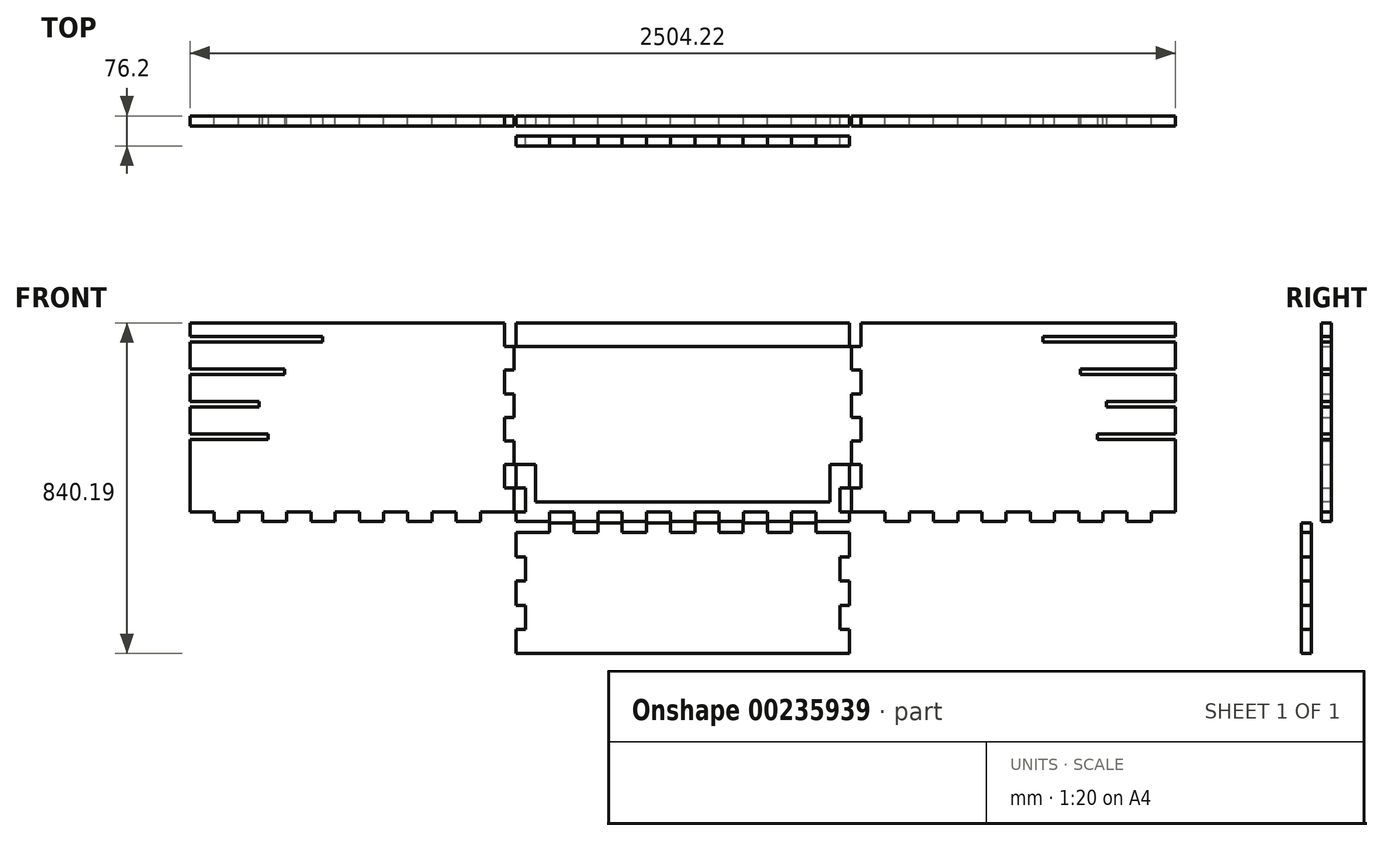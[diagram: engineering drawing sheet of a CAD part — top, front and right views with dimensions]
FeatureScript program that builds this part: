
annotation { "Feature Type Name" : "Feature", "Feature Type Description" : "" }
export const myFeature = defineFeature(function(context is Context, id is Id, definition is map)
    precondition{}
    {
        {
            var Q0;
            Q0=qCreatedBy(makeId("Front.planeOp"),FACE);
            var sketch = newSketch(context, id + "F0", { "sketchPlane" : qUnion([Q0])});
            skLineSegment(sketch, "E0", {"start": v(-454.2, -1273) * mm, "end": v(-454.2, -1334.62) * mm});
            skLineSegment(sketch, "E1", {"start": v(-430.22, -1273) * mm, "end": v(-454.2, -1273) * mm});
            skLineSegment(sketch, "E2", {"start": v(-454.2, -1150.02) * mm, "end": v(-454.2, -1211.63) * mm});
            skLineSegment(sketch, "E3", {"start": v(-454.2, -1211.63) * mm, "end": v(-430.22, -1211.63) * mm});
            skLineSegment(sketch, "E4", {"start": v(-430.22, -1150.02) * mm, "end": v(-454.2, -1150.02) * mm});
            skLineSegment(sketch, "E5", {"start": v(-454.2, -1027.04) * mm, "end": v(-454.2, -1088.65) * mm});
            skLineSegment(sketch, "E6", {"start": v(-454.2, -1088.65) * mm, "end": v(-430.22, -1088.65) * mm});
            skLineSegment(sketch, "E7", {"start": v(-430.22, -1027.04) * mm, "end": v(-454.2, -1027.04) * mm});
            skLineSegment(sketch, "E8", {"start": v(-454.2, -904.06) * mm, "end": v(-454.2, -965.67) * mm});
            skLineSegment(sketch, "E9", {"start": v(-454.2, -965.67) * mm, "end": v(-430.22, -965.67) * mm});
            skLineSegment(sketch, "E10", {"start": v(-430.22, -904.06) * mm, "end": v(-454.2, -904.06) * mm});
            skLineSegment(sketch, "E11", {"start": v(-454.2, -781.07) * mm, "end": v(-454.2, -842.69) * mm});
            skLineSegment(sketch, "E12", {"start": v(-454.2, -842.69) * mm, "end": v(-430.22, -842.69) * mm});
            skLineSegment(sketch, "E13", {"start": v(-430.22, -781.07) * mm, "end": v(-454.2, -781.07) * mm});
            skLineSegment(sketch, "E14", {"start": v(-454.2, -658.1) * mm, "end": v(-454.2, -719.7) * mm});
            skLineSegment(sketch, "E15", {"start": v(-454.2, -719.7) * mm, "end": v(-430.22, -719.7) * mm});
            skLineSegment(sketch, "E16", {"start": v(-430.22, -658.1) * mm, "end": v(-454.2, -658.1) * mm});
            skLineSegment(sketch, "E17", {"start": v(-454.2, -535.1) * mm, "end": v(-454.2, -596.71) * mm});
            skLineSegment(sketch, "E18", {"start": v(-454.2, -596.71) * mm, "end": v(-430.22, -596.71) * mm});
            skLineSegment(sketch, "E19", {"start": v(-454.2, -535.1) * mm, "end": v(-430.22, -535.1) * mm});
            skLineSegment(sketch, "E20", {"start": v(-430.22, -1211.63) * mm, "end": v(-430.22, -1273) * mm});
            skLineSegment(sketch, "E21", {"start": v(-430.22, -1088.65) * mm, "end": v(-430.22, -1150.02) * mm});
            skLineSegment(sketch, "E22", {"start": v(-430.22, -965.67) * mm, "end": v(-430.22, -1027.04) * mm});
            skLineSegment(sketch, "E23", {"start": v(-430.22, -842.69) * mm, "end": v(-430.22, -904.06) * mm});
            skLineSegment(sketch, "E24", {"start": v(-430.22, -719.7) * mm, "end": v(-430.22, -781.07) * mm});
            skLineSegment(sketch, "E25", {"start": v(-430.22, -596.71) * mm, "end": v(-430.22, -658.1) * mm});
            skLineSegment(sketch, "E26", {"start": v(-430.22, -535.1) * mm, "end": v(-368.73, -535.1) * mm});
            skLineSegment(sketch, "E27", {"start": v(-368.73, -511.12) * mm, "end": v(-368.73, -535.1) * mm});
            skLineSegment(sketch, "E28", {"start": v(-307.11, -511.12) * mm, "end": v(-368.73, -511.12) * mm});
            skLineSegment(sketch, "E29", {"start": v(-307.11, -535.1) * mm, "end": v(-307.11, -511.12) * mm});
            skLineSegment(sketch, "E30", {"start": v(-245.74, -535.1) * mm, "end": v(-307.11, -535.1) * mm});
            skLineSegment(sketch, "E31", {"start": v(-245.74, -511.12) * mm, "end": v(-245.74, -535.1) * mm});
            skLineSegment(sketch, "E32", {"start": v(-184.13, -511.12) * mm, "end": v(-245.74, -511.12) * mm});
            skLineSegment(sketch, "E33", {"start": v(-184.13, -535.1) * mm, "end": v(-184.13, -511.12) * mm});
            skLineSegment(sketch, "E34", {"start": v(-122.76, -535.1) * mm, "end": v(-184.13, -535.1) * mm});
            skLineSegment(sketch, "E35", {"start": v(-122.76, -511.12) * mm, "end": v(-122.76, -535.1) * mm});
            skLineSegment(sketch, "E36", {"start": v(-61.15, -511.12) * mm, "end": v(-122.76, -511.12) * mm});
            skLineSegment(sketch, "E37", {"start": v(-61.15, -535.1) * mm, "end": v(-61.15, -511.12) * mm});
            skLineSegment(sketch, "E38", {"start": v(0.22, -535.1) * mm, "end": v(-61.15, -535.1) * mm});
            skLineSegment(sketch, "E39", {"start": v(0.22, -511.12) * mm, "end": v(0.22, -535.1) * mm});
            skLineSegment(sketch, "E40", {"start": v(61.84, -511.12) * mm, "end": v(0.22, -511.12) * mm});
            skLineSegment(sketch, "E41", {"start": v(61.84, -535.1) * mm, "end": v(61.84, -511.12) * mm});
            skLineSegment(sketch, "E42", {"start": v(123.2, -535.1) * mm, "end": v(61.84, -535.1) * mm});
            skLineSegment(sketch, "E43", {"start": v(123.2, -511.12) * mm, "end": v(123.2, -535.1) * mm});
            skLineSegment(sketch, "E44", {"start": v(184.82, -511.12) * mm, "end": v(123.2, -511.12) * mm});
            skLineSegment(sketch, "E45", {"start": v(184.82, -535.1) * mm, "end": v(184.82, -511.12) * mm});
            skLineSegment(sketch, "E46", {"start": v(246.19, -535.1) * mm, "end": v(184.82, -535.1) * mm});
            skLineSegment(sketch, "E47", {"start": v(246.19, -511.12) * mm, "end": v(246.19, -535.1) * mm});
            skLineSegment(sketch, "E48", {"start": v(307.8, -511.12) * mm, "end": v(246.19, -511.12) * mm});
            skLineSegment(sketch, "E49", {"start": v(307.8, -535.1) * mm, "end": v(307.8, -511.12) * mm});
            skLineSegment(sketch, "E50", {"start": v(307.8, -535.1) * mm, "end": v(369.29, -535.1) * mm});
            skLineSegment(sketch, "E51", {"start": v(369.29, -1273) * mm, "end": v(369.29, -1211.63) * mm});
            skLineSegment(sketch, "E52", {"start": v(393.28, -1273) * mm, "end": v(369.29, -1273) * mm});
            skLineSegment(sketch, "E53", {"start": v(369.29, -1211.63) * mm, "end": v(393.28, -1211.63) * mm});
            skLineSegment(sketch, "E54", {"start": v(369.29, -1150.02) * mm, "end": v(369.29, -1088.65) * mm});
            skLineSegment(sketch, "E55", {"start": v(393.28, -1150.02) * mm, "end": v(369.29, -1150.02) * mm});
            skLineSegment(sketch, "E56", {"start": v(369.29, -1088.65) * mm, "end": v(393.28, -1088.65) * mm});
            skLineSegment(sketch, "E57", {"start": v(369.29, -1027.04) * mm, "end": v(369.29, -965.67) * mm});
            skLineSegment(sketch, "E58", {"start": v(393.28, -1027.04) * mm, "end": v(369.29, -1027.04) * mm});
            skLineSegment(sketch, "E59", {"start": v(369.29, -965.67) * mm, "end": v(393.28, -965.67) * mm});
            skLineSegment(sketch, "E60", {"start": v(369.29, -904.06) * mm, "end": v(369.29, -842.69) * mm});
            skLineSegment(sketch, "E61", {"start": v(393.28, -904.06) * mm, "end": v(369.29, -904.06) * mm});
            skLineSegment(sketch, "E62", {"start": v(369.29, -842.69) * mm, "end": v(393.28, -842.69) * mm});
            skLineSegment(sketch, "E63", {"start": v(369.29, -781.07) * mm, "end": v(369.29, -719.7) * mm});
            skLineSegment(sketch, "E64", {"start": v(393.28, -781.07) * mm, "end": v(369.29, -781.07) * mm});
            skLineSegment(sketch, "E65", {"start": v(369.29, -719.7) * mm, "end": v(393.28, -719.7) * mm});
            skLineSegment(sketch, "E66", {"start": v(369.29, -658.1) * mm, "end": v(369.29, -596.71) * mm});
            skLineSegment(sketch, "E67", {"start": v(393.28, -658.1) * mm, "end": v(369.29, -658.1) * mm});
            skLineSegment(sketch, "E68", {"start": v(369.29, -596.71) * mm, "end": v(393.28, -596.71) * mm});
            skLineSegment(sketch, "E69", {"start": v(369.29, -535.1) * mm, "end": v(393.28, -535.1) * mm});
            skLineSegment(sketch, "E70", {"start": v(393.28, -1334.62) * mm, "end": v(393.28, -1273) * mm});
            skLineSegment(sketch, "E71", {"start": v(393.28, -1211.63) * mm, "end": v(393.28, -1150.02) * mm});
            skLineSegment(sketch, "E72", {"start": v(393.28, -1088.65) * mm, "end": v(393.28, -1027.04) * mm});
            skLineSegment(sketch, "E73", {"start": v(393.28, -965.67) * mm, "end": v(393.28, -904.06) * mm});
            skLineSegment(sketch, "E74", {"start": v(393.28, -842.69) * mm, "end": v(393.28, -781.07) * mm});
            skLineSegment(sketch, "E75", {"start": v(393.28, -719.7) * mm, "end": v(393.28, -658.1) * mm});
            skLineSegment(sketch, "E76", {"start": v(393.28, -596.71) * mm, "end": v(393.28, -535.1) * mm});
            skLineSegment(sketch, "E77", {"start": v(-454.2, -506.25) * mm, "end": v(-454.2, -482.26) * mm});
            skLineSegment(sketch, "E78", {"start": v(-454.2, -482.26) * mm, "end": v(-454.2, -482.15) * mm});
            skLineSegment(sketch, "E79", {"start": v(-430.22, -482.15) * mm, "end": v(-454.2, -482.15) * mm});
            skLineSegment(sketch, "E80", {"start": v(-454.2, -362.23) * mm, "end": v(-454.2, -422.3) * mm});
            skLineSegment(sketch, "E81", {"start": v(-454.2, -422.3) * mm, "end": v(-430.22, -422.3) * mm});
            skLineSegment(sketch, "E82", {"start": v(-430.22, -362.23) * mm, "end": v(-454.2, -362.23) * mm});
            skLineSegment(sketch, "E83", {"start": v(-454.2, -242.33) * mm, "end": v(-454.2, -302.4) * mm});
            skLineSegment(sketch, "E84", {"start": v(-454.2, -302.4) * mm, "end": v(-430.22, -302.4) * mm});
            skLineSegment(sketch, "E85", {"start": v(-430.22, -242.33) * mm, "end": v(-454.2, -242.33) * mm});
            skLineSegment(sketch, "E86", {"start": v(-454.2, -122.41) * mm, "end": v(-454.2, -182.5) * mm});
            skLineSegment(sketch, "E87", {"start": v(-454.2, -182.5) * mm, "end": v(-430.22, -182.5) * mm});
            skLineSegment(sketch, "E88", {"start": v(-430.22, -122.41) * mm, "end": v(-454.2, -122.41) * mm});
            skLineSegment(sketch, "E89", {"start": v(-454.2, -2.5) * mm, "end": v(-454.2, -62.59) * mm});
            skLineSegment(sketch, "E90", {"start": v(-454.2, -62.59) * mm, "end": v(-430.22, -62.59) * mm});
            skLineSegment(sketch, "E91", {"start": v(-430.22, -2.5) * mm, "end": v(-454.2, -2.5) * mm});
            skLineSegment(sketch, "E92", {"start": v(-454.2, 117.4) * mm, "end": v(-454.2, 57.32) * mm});
            skLineSegment(sketch, "E93", {"start": v(-454.2, 57.32) * mm, "end": v(-430.22, 57.32) * mm});
            skLineSegment(sketch, "E94", {"start": v(-430.22, 117.4) * mm, "end": v(-454.2, 117.4) * mm});
            skLineSegment(sketch, "E95", {"start": v(-454.2, 237.31) * mm, "end": v(-454.2, 177.24) * mm});
            skLineSegment(sketch, "E96", {"start": v(-454.2, 177.24) * mm, "end": v(-430.22, 177.24) * mm});
            skLineSegment(sketch, "E97", {"start": v(-430.22, 237.31) * mm, "end": v(-454.2, 237.31) * mm});
            skLineSegment(sketch, "E98", {"start": v(-454.2, 357.22) * mm, "end": v(-454.2, 297.14) * mm});
            skLineSegment(sketch, "E99", {"start": v(-454.2, 297.14) * mm, "end": v(-430.22, 297.14) * mm});
            skLineSegment(sketch, "E100", {"start": v(-430.22, 357.22) * mm, "end": v(-454.2, 357.22) * mm});
            skLineSegment(sketch, "E101", {"start": v(-454.2, 417.05) * mm, "end": v(-454.2, 417.17) * mm});
            skLineSegment(sketch, "E102", {"start": v(-430.22, -422.3) * mm, "end": v(-430.22, -482.15) * mm});
            skLineSegment(sketch, "E103", {"start": v(-430.22, -302.4) * mm, "end": v(-430.22, -362.23) * mm});
            skLineSegment(sketch, "E104", {"start": v(-430.22, -182.5) * mm, "end": v(-430.22, -242.33) * mm});
            skLineSegment(sketch, "E105", {"start": v(-430.22, -62.59) * mm, "end": v(-430.22, -122.41) * mm});
            skLineSegment(sketch, "E106", {"start": v(-430.22, 57.32) * mm, "end": v(-430.22, -2.5) * mm});
            skLineSegment(sketch, "E107", {"start": v(-430.22, 177.24) * mm, "end": v(-430.22, 117.4) * mm});
            skLineSegment(sketch, "E108", {"start": v(-430.22, 297.14) * mm, "end": v(-430.22, 237.31) * mm});
            skLineSegment(sketch, "E109", {"start": v(-430.22, 417.05) * mm, "end": v(-430.22, 357.22) * mm});
            skLineSegment(sketch, "E110", {"start": v(-368.61, -506.25) * mm, "end": v(-368.61, -482.26) * mm});
            skLineSegment(sketch, "E111", {"start": v(-307.24, -482.26) * mm, "end": v(-307.24, -506.25) * mm});
            skLineSegment(sketch, "E112", {"start": v(-307.24, -506.25) * mm, "end": v(-245.62, -506.25) * mm});
            skLineSegment(sketch, "E113", {"start": v(-245.62, -506.25) * mm, "end": v(-245.62, -482.26) * mm});
            skLineSegment(sketch, "E114", {"start": v(-245.62, -482.26) * mm, "end": v(-184.26, -482.26) * mm});
            skLineSegment(sketch, "E115", {"start": v(-184.26, -482.26) * mm, "end": v(-184.26, -506.25) * mm});
            skLineSegment(sketch, "E116", {"start": v(-184.26, -506.25) * mm, "end": v(-122.64, -506.25) * mm});
            skLineSegment(sketch, "E117", {"start": v(-122.64, -506.25) * mm, "end": v(-122.64, -482.26) * mm});
            skLineSegment(sketch, "E118", {"start": v(-122.64, -482.26) * mm, "end": v(-61.27, -482.26) * mm});
            skLineSegment(sketch, "E119", {"start": v(-61.27, -482.26) * mm, "end": v(-61.27, -506.25) * mm});
            skLineSegment(sketch, "E120", {"start": v(-61.27, -506.25) * mm, "end": v(0.34, -506.25) * mm});
            skLineSegment(sketch, "E121", {"start": v(0.34, -506.25) * mm, "end": v(0.34, -482.26) * mm});
            skLineSegment(sketch, "E122", {"start": v(0.34, -482.26) * mm, "end": v(61.71, -482.26) * mm});
            skLineSegment(sketch, "E123", {"start": v(61.71, -482.26) * mm, "end": v(61.71, -506.25) * mm});
            skLineSegment(sketch, "E124", {"start": v(61.71, -506.25) * mm, "end": v(123.33, -506.25) * mm});
            skLineSegment(sketch, "E125", {"start": v(123.33, -506.25) * mm, "end": v(123.33, -482.26) * mm});
            skLineSegment(sketch, "E126", {"start": v(123.33, -482.26) * mm, "end": v(184.7, -482.26) * mm});
            skLineSegment(sketch, "E127", {"start": v(184.7, -482.26) * mm, "end": v(184.7, -506.25) * mm});
            skLineSegment(sketch, "E128", {"start": v(184.7, -506.25) * mm, "end": v(246.3, -506.25) * mm});
            skLineSegment(sketch, "E129", {"start": v(246.3, -506.25) * mm, "end": v(246.3, -482.26) * mm});
            skLineSegment(sketch, "E130", {"start": v(246.3, -482.26) * mm, "end": v(307.69, -482.26) * mm});
            skLineSegment(sketch, "E131", {"start": v(307.69, -482.26) * mm, "end": v(307.69, -506.25) * mm});
            skLineSegment(sketch, "E132", {"start": v(307.69, -506.25) * mm, "end": v(369.29, -506.25) * mm});
            skLineSegment(sketch, "E133", {"start": v(369.29, -482.15) * mm, "end": v(369.29, -422.3) * mm});
            skLineSegment(sketch, "E134", {"start": v(369.29, -482.15) * mm, "end": v(393.28, -482.15) * mm});
            skLineSegment(sketch, "E135", {"start": v(369.29, -422.3) * mm, "end": v(393.28, -422.3) * mm});
            skLineSegment(sketch, "E136", {"start": v(369.29, -362.23) * mm, "end": v(369.29, -302.4) * mm});
            skLineSegment(sketch, "E137", {"start": v(393.28, -362.23) * mm, "end": v(369.29, -362.23) * mm});
            skLineSegment(sketch, "E138", {"start": v(369.29, -302.4) * mm, "end": v(393.28, -302.4) * mm});
            skLineSegment(sketch, "E139", {"start": v(369.29, -242.33) * mm, "end": v(369.29, -182.5) * mm});
            skLineSegment(sketch, "E140", {"start": v(393.28, -242.33) * mm, "end": v(369.29, -242.33) * mm});
            skLineSegment(sketch, "E141", {"start": v(369.29, -182.5) * mm, "end": v(393.28, -182.5) * mm});
            skLineSegment(sketch, "E142", {"start": v(369.29, -122.41) * mm, "end": v(369.29, -62.59) * mm});
            skLineSegment(sketch, "E143", {"start": v(393.28, -122.41) * mm, "end": v(369.29, -122.41) * mm});
            skLineSegment(sketch, "E144", {"start": v(369.29, -62.59) * mm, "end": v(393.28, -62.59) * mm});
            skLineSegment(sketch, "E145", {"start": v(369.29, -2.5) * mm, "end": v(369.29, 57.32) * mm});
            skLineSegment(sketch, "E146", {"start": v(393.28, -2.5) * mm, "end": v(369.29, -2.5) * mm});
            skLineSegment(sketch, "E147", {"start": v(369.29, 57.32) * mm, "end": v(393.28, 57.32) * mm});
            skLineSegment(sketch, "E148", {"start": v(369.29, 117.4) * mm, "end": v(369.29, 177.24) * mm});
            skLineSegment(sketch, "E149", {"start": v(393.28, 117.4) * mm, "end": v(369.29, 117.4) * mm});
            skLineSegment(sketch, "E150", {"start": v(369.29, 177.24) * mm, "end": v(393.28, 177.24) * mm});
            skLineSegment(sketch, "E151", {"start": v(369.29, 237.31) * mm, "end": v(369.29, 297.14) * mm});
            skLineSegment(sketch, "E152", {"start": v(393.28, 237.31) * mm, "end": v(369.29, 237.31) * mm});
            skLineSegment(sketch, "E153", {"start": v(369.29, 297.14) * mm, "end": v(393.28, 297.14) * mm});
            skLineSegment(sketch, "E154", {"start": v(369.29, 357.22) * mm, "end": v(369.29, 417.05) * mm});
            skLineSegment(sketch, "E155", {"start": v(393.28, 357.22) * mm, "end": v(369.29, 357.22) * mm});
            skLineSegment(sketch, "E156", {"start": v(369.29, -506.25) * mm, "end": v(393.28, -506.25) * mm});
            skLineSegment(sketch, "E157", {"start": v(393.28, -506.25) * mm, "end": v(393.28, -482.26) * mm});
            skLineSegment(sketch, "E158", {"start": v(393.28, -482.26) * mm, "end": v(393.28, -482.15) * mm});
            skLineSegment(sketch, "E159", {"start": v(393.28, -422.3) * mm, "end": v(393.28, -362.23) * mm});
            skLineSegment(sketch, "E160", {"start": v(393.28, -302.4) * mm, "end": v(393.28, -242.33) * mm});
            skLineSegment(sketch, "E161", {"start": v(393.28, -182.5) * mm, "end": v(393.28, -122.41) * mm});
            skLineSegment(sketch, "E162", {"start": v(393.28, -62.59) * mm, "end": v(393.28, -2.5) * mm});
            skLineSegment(sketch, "E163", {"start": v(393.28, 57.32) * mm, "end": v(393.28, 117.4) * mm});
            skLineSegment(sketch, "E164", {"start": v(393.28, 177.24) * mm, "end": v(393.28, 237.31) * mm});
            skLineSegment(sketch, "E165", {"start": v(393.28, 297.14) * mm, "end": v(393.28, 357.22) * mm});
            skLineSegment(sketch, "E166", {"start": v(393.28, 417.05) * mm, "end": v(393.28, 417.17) * mm});
            skLineSegment(sketch, "E167", {"start": v(-1282.57, -482.26) * mm, "end": v(-1221.08, -482.26) * mm});
            skLineSegment(sketch, "E168", {"start": v(-1221.08, -482.26) * mm, "end": v(-1221.08, -506.25) * mm});
            skLineSegment(sketch, "E169", {"start": v(-1221.08, -506.25) * mm, "end": v(-1159.47, -506.25) * mm});
            skLineSegment(sketch, "E170", {"start": v(-1159.47, -506.25) * mm, "end": v(-1159.47, -482.26) * mm});
            skLineSegment(sketch, "E171", {"start": v(-1159.47, -482.26) * mm, "end": v(-1098.1, -482.26) * mm});
            skLineSegment(sketch, "E172", {"start": v(-1098.1, -482.26) * mm, "end": v(-1098.1, -506.25) * mm});
            skLineSegment(sketch, "E173", {"start": v(-1098.1, -506.25) * mm, "end": v(-1036.48, -506.25) * mm});
            skLineSegment(sketch, "E174", {"start": v(-1036.48, -506.25) * mm, "end": v(-1036.48, -482.26) * mm});
            skLineSegment(sketch, "E175", {"start": v(-1036.48, -482.26) * mm, "end": v(-975.11, -482.26) * mm});
            skLineSegment(sketch, "E176", {"start": v(-975.11, -482.26) * mm, "end": v(-975.11, -506.25) * mm});
            skLineSegment(sketch, "E177", {"start": v(-975.11, -506.25) * mm, "end": v(-913.5, -506.25) * mm});
            skLineSegment(sketch, "E178", {"start": v(-913.5, -506.25) * mm, "end": v(-913.5, -482.26) * mm});
            skLineSegment(sketch, "E179", {"start": v(-913.5, -482.26) * mm, "end": v(-852.13, -482.26) * mm});
            skLineSegment(sketch, "E180", {"start": v(-852.13, -482.26) * mm, "end": v(-852.13, -506.25) * mm});
            skLineSegment(sketch, "E181", {"start": v(-852.13, -506.25) * mm, "end": v(-790.52, -506.25) * mm});
            skLineSegment(sketch, "E182", {"start": v(-790.52, -506.25) * mm, "end": v(-790.52, -482.26) * mm});
            skLineSegment(sketch, "E183", {"start": v(-790.52, -482.26) * mm, "end": v(-729.15, -482.26) * mm});
            skLineSegment(sketch, "E184", {"start": v(-729.15, -482.26) * mm, "end": v(-729.15, -506.25) * mm});
            skLineSegment(sketch, "E185", {"start": v(-729.15, -506.25) * mm, "end": v(-667.53, -506.25) * mm});
            skLineSegment(sketch, "E186", {"start": v(-667.53, -506.25) * mm, "end": v(-667.53, -482.26) * mm});
            skLineSegment(sketch, "E187", {"start": v(-667.53, -482.26) * mm, "end": v(-606.17, -482.26) * mm});
            skLineSegment(sketch, "E188", {"start": v(-606.17, -482.26) * mm, "end": v(-606.17, -506.25) * mm});
            skLineSegment(sketch, "E189", {"start": v(-606.17, -506.25) * mm, "end": v(-544.55, -506.25) * mm});
            skLineSegment(sketch, "E190", {"start": v(-544.55, -506.25) * mm, "end": v(-544.55, -482.26) * mm});
            skLineSegment(sketch, "E191", {"start": v(-544.55, -482.26) * mm, "end": v(-483.06, -482.26) * mm});
            skLineSegment(sketch, "E192", {"start": v(-483.06, -482.26) * mm, "end": v(-459.08, -482.26) * mm});
            skLineSegment(sketch, "E193", {"start": v(-483.06, -422.19) * mm, "end": v(-483.06, -362.36) * mm});
            skLineSegment(sketch, "E194", {"start": v(-459.08, -422.19) * mm, "end": v(-483.06, -422.19) * mm});
            skLineSegment(sketch, "E195", {"start": v(-483.06, -362.36) * mm, "end": v(-459.08, -362.36) * mm});
            skLineSegment(sketch, "E196", {"start": v(-483.06, -302.28) * mm, "end": v(-483.06, -242.45) * mm});
            skLineSegment(sketch, "E197", {"start": v(-459.08, -302.28) * mm, "end": v(-483.06, -302.28) * mm});
            skLineSegment(sketch, "E198", {"start": v(-483.06, -242.45) * mm, "end": v(-459.08, -242.45) * mm});
            skLineSegment(sketch, "E199", {"start": v(-483.06, -182.38) * mm, "end": v(-483.06, -122.53) * mm});
            skLineSegment(sketch, "E200", {"start": v(-459.08, -182.38) * mm, "end": v(-483.06, -182.38) * mm});
            skLineSegment(sketch, "E201", {"start": v(-483.06, -122.53) * mm, "end": v(-459.08, -122.53) * mm});
            skLineSegment(sketch, "E202", {"start": v(-483.06, -62.46) * mm, "end": v(-483.06, -2.63) * mm});
            skLineSegment(sketch, "E203", {"start": v(-459.08, -62.46) * mm, "end": v(-483.06, -62.46) * mm});
            skLineSegment(sketch, "E204", {"start": v(-483.06, -2.63) * mm, "end": v(-459.08, -2.63) * mm});
            skLineSegment(sketch, "E205", {"start": v(-483.06, 57.45) * mm, "end": v(-483.06, 117.28) * mm});
            skLineSegment(sketch, "E206", {"start": v(-459.08, 57.45) * mm, "end": v(-483.06, 57.45) * mm});
            skLineSegment(sketch, "E207", {"start": v(-483.06, 117.28) * mm, "end": v(-459.08, 117.28) * mm});
            skLineSegment(sketch, "E208", {"start": v(-483.06, 177.36) * mm, "end": v(-483.06, 237.19) * mm});
            skLineSegment(sketch, "E209", {"start": v(-459.08, 177.36) * mm, "end": v(-483.06, 177.36) * mm});
            skLineSegment(sketch, "E210", {"start": v(-483.06, 237.19) * mm, "end": v(-459.08, 237.19) * mm});
            skLineSegment(sketch, "E211", {"start": v(-483.06, 297.26) * mm, "end": v(-483.06, 357.1) * mm});
            skLineSegment(sketch, "E212", {"start": v(-459.08, 297.26) * mm, "end": v(-483.06, 297.26) * mm});
            skLineSegment(sketch, "E213", {"start": v(-483.06, 357.1) * mm, "end": v(-459.08, 357.1) * mm});
            skLineSegment(sketch, "E214", {"start": v(-459.08, -482.26) * mm, "end": v(-459.08, -422.19) * mm});
            skLineSegment(sketch, "E215", {"start": v(-459.08, -362.36) * mm, "end": v(-459.08, -302.28) * mm});
            skLineSegment(sketch, "E216", {"start": v(-459.08, -242.45) * mm, "end": v(-459.08, -182.38) * mm});
            skLineSegment(sketch, "E217", {"start": v(-459.08, -122.53) * mm, "end": v(-459.08, -62.46) * mm});
            skLineSegment(sketch, "E218", {"start": v(-459.08, -2.63) * mm, "end": v(-459.08, 57.45) * mm});
            skLineSegment(sketch, "E219", {"start": v(-459.08, 117.28) * mm, "end": v(-459.08, 177.36) * mm});
            skLineSegment(sketch, "E220", {"start": v(-459.08, 237.19) * mm, "end": v(-459.08, 297.26) * mm});
            skLineSegment(sketch, "E221", {"start": v(-459.08, 357.1) * mm, "end": v(-459.08, 417.17) * mm});
            skLineSegment(sketch, "E222", {"start": v(398.15, -422.19) * mm, "end": v(398.15, -482.26) * mm});
            skLineSegment(sketch, "E223", {"start": v(398.15, -482.26) * mm, "end": v(422.13, -482.26) * mm});
            skLineSegment(sketch, "E224", {"start": v(422.13, -422.19) * mm, "end": v(398.15, -422.19) * mm});
            skLineSegment(sketch, "E225", {"start": v(398.15, -302.28) * mm, "end": v(398.15, -362.36) * mm});
            skLineSegment(sketch, "E226", {"start": v(398.15, -362.36) * mm, "end": v(422.13, -362.36) * mm});
            skLineSegment(sketch, "E227", {"start": v(422.13, -302.28) * mm, "end": v(398.15, -302.28) * mm});
            skLineSegment(sketch, "E228", {"start": v(398.15, -182.38) * mm, "end": v(398.15, -242.45) * mm});
            skLineSegment(sketch, "E229", {"start": v(398.15, -242.45) * mm, "end": v(422.13, -242.45) * mm});
            skLineSegment(sketch, "E230", {"start": v(422.13, -182.38) * mm, "end": v(398.15, -182.38) * mm});
            skLineSegment(sketch, "E231", {"start": v(398.15, -62.46) * mm, "end": v(398.15, -122.53) * mm});
            skLineSegment(sketch, "E232", {"start": v(398.15, -122.53) * mm, "end": v(422.13, -122.53) * mm});
            skLineSegment(sketch, "E233", {"start": v(422.13, -62.46) * mm, "end": v(398.15, -62.46) * mm});
            skLineSegment(sketch, "E234", {"start": v(398.15, 57.45) * mm, "end": v(398.15, -2.63) * mm});
            skLineSegment(sketch, "E235", {"start": v(398.15, -2.63) * mm, "end": v(422.13, -2.63) * mm});
            skLineSegment(sketch, "E236", {"start": v(422.13, 57.45) * mm, "end": v(398.15, 57.45) * mm});
            skLineSegment(sketch, "E237", {"start": v(398.15, 177.36) * mm, "end": v(398.15, 117.28) * mm});
            skLineSegment(sketch, "E238", {"start": v(398.15, 117.28) * mm, "end": v(422.13, 117.28) * mm});
            skLineSegment(sketch, "E239", {"start": v(422.13, 177.36) * mm, "end": v(398.15, 177.36) * mm});
            skLineSegment(sketch, "E240", {"start": v(398.15, 297.26) * mm, "end": v(398.15, 237.19) * mm});
            skLineSegment(sketch, "E241", {"start": v(398.15, 237.19) * mm, "end": v(422.13, 237.19) * mm});
            skLineSegment(sketch, "E242", {"start": v(422.13, 297.26) * mm, "end": v(398.15, 297.26) * mm});
            skLineSegment(sketch, "E243", {"start": v(398.15, 417.17) * mm, "end": v(398.15, 357.1) * mm});
            skLineSegment(sketch, "E244", {"start": v(398.15, 357.1) * mm, "end": v(422.13, 357.1) * mm});
            skLineSegment(sketch, "E245", {"start": v(422.13, -482.26) * mm, "end": v(483.63, -482.26) * mm});
            skLineSegment(sketch, "E246", {"start": v(422.13, -362.36) * mm, "end": v(422.13, -422.19) * mm});
            skLineSegment(sketch, "E247", {"start": v(422.13, -242.45) * mm, "end": v(422.13, -302.28) * mm});
            skLineSegment(sketch, "E248", {"start": v(422.13, -122.53) * mm, "end": v(422.13, -182.38) * mm});
            skLineSegment(sketch, "E249", {"start": v(422.13, -2.63) * mm, "end": v(422.13, -62.46) * mm});
            skLineSegment(sketch, "E250", {"start": v(422.13, 117.28) * mm, "end": v(422.13, 57.45) * mm});
            skLineSegment(sketch, "E251", {"start": v(422.13, 237.19) * mm, "end": v(422.13, 177.36) * mm});
            skLineSegment(sketch, "E252", {"start": v(422.13, 357.1) * mm, "end": v(422.13, 297.26) * mm});
            skLineSegment(sketch, "E253", {"start": v(483.63, -482.26) * mm, "end": v(483.63, -506.25) * mm});
            skLineSegment(sketch, "E254", {"start": v(483.63, -506.25) * mm, "end": v(545.24, -506.25) * mm});
            skLineSegment(sketch, "E255", {"start": v(545.24, -506.25) * mm, "end": v(545.24, -482.26) * mm});
            skLineSegment(sketch, "E256", {"start": v(545.24, -482.26) * mm, "end": v(606.6, -482.26) * mm});
            skLineSegment(sketch, "E257", {"start": v(606.6, -482.26) * mm, "end": v(606.6, -506.25) * mm});
            skLineSegment(sketch, "E258", {"start": v(606.6, -506.25) * mm, "end": v(668.22, -506.25) * mm});
            skLineSegment(sketch, "E259", {"start": v(668.22, -506.25) * mm, "end": v(668.22, -482.26) * mm});
            skLineSegment(sketch, "E260", {"start": v(668.22, -482.26) * mm, "end": v(729.59, -482.26) * mm});
            skLineSegment(sketch, "E261", {"start": v(729.59, -482.26) * mm, "end": v(729.59, -506.25) * mm});
            skLineSegment(sketch, "E262", {"start": v(729.59, -506.25) * mm, "end": v(791.2, -506.25) * mm});
            skLineSegment(sketch, "E263", {"start": v(791.2, -506.25) * mm, "end": v(791.2, -482.26) * mm});
            skLineSegment(sketch, "E264", {"start": v(791.2, -482.26) * mm, "end": v(852.58, -482.26) * mm});
            skLineSegment(sketch, "E265", {"start": v(852.58, -482.26) * mm, "end": v(852.58, -506.25) * mm});
            skLineSegment(sketch, "E266", {"start": v(852.58, -506.25) * mm, "end": v(914.19, -506.25) * mm});
            skLineSegment(sketch, "E267", {"start": v(914.19, -506.25) * mm, "end": v(914.19, -482.26) * mm});
            skLineSegment(sketch, "E268", {"start": v(914.19, -482.26) * mm, "end": v(975.56, -482.26) * mm});
            skLineSegment(sketch, "E269", {"start": v(975.56, -482.26) * mm, "end": v(975.56, -506.25) * mm});
            skLineSegment(sketch, "E270", {"start": v(975.56, -506.25) * mm, "end": v(1037.17, -506.25) * mm});
            skLineSegment(sketch, "E271", {"start": v(1037.17, -506.25) * mm, "end": v(1037.17, -482.26) * mm});
            skLineSegment(sketch, "E272", {"start": v(1037.17, -482.26) * mm, "end": v(1098.54, -482.26) * mm});
            skLineSegment(sketch, "E273", {"start": v(1098.54, -482.26) * mm, "end": v(1098.54, -506.25) * mm});
            skLineSegment(sketch, "E274", {"start": v(1098.54, -506.25) * mm, "end": v(1160.15, -506.25) * mm});
            skLineSegment(sketch, "E275", {"start": v(1160.15, -506.25) * mm, "end": v(1160.15, -482.26) * mm});
            skLineSegment(sketch, "E276", {"start": v(1160.15, -482.26) * mm, "end": v(1221.65, -482.26) * mm});
            skLineSegment(sketch, "E277", {"start": v(-1549.7, -928.38) * mm, "end": v(1612.7, -928.38) * mm, "construction": true});
            skLineSegment(sketch, "E278", {"start": v(-1282.57, -482.26) * mm, "end": v(-1282.57, 417.17) * mm});
            skLineSegment(sketch, "E279", {"start": v(-1282.57, 417.17) * mm, "end": v(-454.2, 417.17) * mm});
            skLineSegment(sketch, "E280", {"start": v(-430.22, 417.05) * mm, "end": v(369.29, 417.05) * mm});
            skLineSegment(sketch, "E281", {"start": v(1221.65, -482.26) * mm, "end": v(1221.65, 417.17) * mm});
            skLineSegment(sketch, "E282", {"start": v(1221.65, 417.17) * mm, "end": v(398.15, 417.17) * mm});
            skLineSegment(sketch, "E283", {"start": v(-454.2, -1334.62) * mm, "end": v(393.28, -1334.62) * mm});
            skPoint(sketch, "E284", {"position": v(-404.82, 391.65) * mm});
            skPoint(sketch, "E285", {"position": v(343.89, 391.65) * mm});
            skLineSegment(sketch, "E286", {"start": v(-368.61, -482.26) * mm, "end": v(-307.24, -482.26) * mm});
            skLineSegment(sketch, "E287", {"start": v(-454.2, -506.25) * mm, "end": v(-368.61, -506.25) * mm});
            skSolve(sketch);
        }
        {
            var Q0;
            Q0=makeQuery(id+"F0.imprint","IMPRINT",FACE,{"disambiguationData":[TD([[makeQuery(id+"F0.imprint","IMPRINT",EDGE,{"derivedFrom":sQuery(id+"F0.wireOp",EDGE,"E167")}),1.0]])]});
            var Q1;
            Q1=makeQuery(id+"F0.imprint","IMPRINT",FACE,{"disambiguationData":[TD([[makeQuery(id+"F0.imprint","IMPRINT",EDGE,{"derivedFrom":sQuery(id+"F0.wireOp",EDGE,"E77")}),-1.0]])]});
            var Q2;
            Q2=makeQuery(id+"F0.imprint","IMPRINT",FACE,{"disambiguationData":[TD([[makeQuery(id+"F0.imprint","IMPRINT",EDGE,{"derivedFrom":sQuery(id+"F0.wireOp",EDGE,"E222")}),1.0]])]});
            var Q3;
            Q3=makeQuery(id+"F0.imprint","IMPRINT",FACE,{"disambiguationData":[TD([[makeQuery(id+"F0.imprint","IMPRINT",EDGE,{"derivedFrom":sQuery(id+"F0.wireOp",EDGE,"E0")}),1.0]])]});
            extrude(context, id + "F1", {"entities" : qUnion([Q0, Q1, Q2, Q3]), "depth" : 25.4 * mm});
        }
        {
            var Q0;
            Q0=makeQuery(id+"F1.opExtrude","CAP_FACE",FACE,{"disambiguationData":[OSD([sQuery(id+"F0.wireOp",EDGE,"E77"),sQuery(id+"F0.wireOp",EDGE,"E78"),sQuery(id+"F0.wireOp",EDGE,"E79"),sQuery(id+"F0.wireOp",EDGE,"E80"),sQuery(id+"F0.wireOp",EDGE,"E81"),sQuery(id+"F0.wireOp",EDGE,"E82"),sQuery(id+"F0.wireOp",EDGE,"E83"),sQuery(id+"F0.wireOp",EDGE,"E84"),sQuery(id+"F0.wireOp",EDGE,"E85"),sQuery(id+"F0.wireOp",EDGE,"E86"),sQuery(id+"F0.wireOp",EDGE,"E87"),sQuery(id+"F0.wireOp",EDGE,"E88"),sQuery(id+"F0.wireOp",EDGE,"E89"),sQuery(id+"F0.wireOp",EDGE,"E90"),sQuery(id+"F0.wireOp",EDGE,"E91"),sQuery(id+"F0.wireOp",EDGE,"E92"),sQuery(id+"F0.wireOp",EDGE,"E93"),sQuery(id+"F0.wireOp",EDGE,"E94"),sQuery(id+"F0.wireOp",EDGE,"E95"),sQuery(id+"F0.wireOp",EDGE,"E96"),sQuery(id+"F0.wireOp",EDGE,"E97"),sQuery(id+"F0.wireOp",EDGE,"E98"),sQuery(id+"F0.wireOp",EDGE,"E99"),sQuery(id+"F0.wireOp",EDGE,"E100"),sQuery(id+"F0.wireOp",EDGE,"E102"),sQuery(id+"F0.wireOp",EDGE,"E103"),sQuery(id+"F0.wireOp",EDGE,"E104"),sQuery(id+"F0.wireOp",EDGE,"E105"),sQuery(id+"F0.wireOp",EDGE,"E106"),sQuery(id+"F0.wireOp",EDGE,"E107"),sQuery(id+"F0.wireOp",EDGE,"E108"),sQuery(id+"F0.wireOp",EDGE,"E109"),sQuery(id+"F0.wireOp",EDGE,"E110"),sQuery(id+"F0.wireOp",EDGE,"E111"),sQuery(id+"F0.wireOp",EDGE,"E112"),sQuery(id+"F0.wireOp",EDGE,"E113"),sQuery(id+"F0.wireOp",EDGE,"E114"),sQuery(id+"F0.wireOp",EDGE,"E115"),sQuery(id+"F0.wireOp",EDGE,"E116"),sQuery(id+"F0.wireOp",EDGE,"E117"),sQuery(id+"F0.wireOp",EDGE,"E118"),sQuery(id+"F0.wireOp",EDGE,"E119"),sQuery(id+"F0.wireOp",EDGE,"E120"),sQuery(id+"F0.wireOp",EDGE,"E121"),sQuery(id+"F0.wireOp",EDGE,"E122"),sQuery(id+"F0.wireOp",EDGE,"E123"),sQuery(id+"F0.wireOp",EDGE,"E124"),sQuery(id+"F0.wireOp",EDGE,"E125"),sQuery(id+"F0.wireOp",EDGE,"E126"),sQuery(id+"F0.wireOp",EDGE,"E127"),sQuery(id+"F0.wireOp",EDGE,"E128"),sQuery(id+"F0.wireOp",EDGE,"E129"),sQuery(id+"F0.wireOp",EDGE,"E130"),sQuery(id+"F0.wireOp",EDGE,"E131"),sQuery(id+"F0.wireOp",EDGE,"E132"),sQuery(id+"F0.wireOp",EDGE,"E133"),sQuery(id+"F0.wireOp",EDGE,"E134"),sQuery(id+"F0.wireOp",EDGE,"E135"),sQuery(id+"F0.wireOp",EDGE,"E136"),sQuery(id+"F0.wireOp",EDGE,"E137"),sQuery(id+"F0.wireOp",EDGE,"E138"),sQuery(id+"F0.wireOp",EDGE,"E139"),sQuery(id+"F0.wireOp",EDGE,"E140"),sQuery(id+"F0.wireOp",EDGE,"E141"),sQuery(id+"F0.wireOp",EDGE,"E142"),sQuery(id+"F0.wireOp",EDGE,"E143"),sQuery(id+"F0.wireOp",EDGE,"E144"),sQuery(id+"F0.wireOp",EDGE,"E145"),sQuery(id+"F0.wireOp",EDGE,"E146"),sQuery(id+"F0.wireOp",EDGE,"E147"),sQuery(id+"F0.wireOp",EDGE,"E148"),sQuery(id+"F0.wireOp",EDGE,"E149"),sQuery(id+"F0.wireOp",EDGE,"E150"),sQuery(id+"F0.wireOp",EDGE,"E151"),sQuery(id+"F0.wireOp",EDGE,"E152"),sQuery(id+"F0.wireOp",EDGE,"E153"),sQuery(id+"F0.wireOp",EDGE,"E154"),sQuery(id+"F0.wireOp",EDGE,"E155"),sQuery(id+"F0.wireOp",EDGE,"E156"),sQuery(id+"F0.wireOp",EDGE,"E157"),sQuery(id+"F0.wireOp",EDGE,"E158"),sQuery(id+"F0.wireOp",EDGE,"E159"),sQuery(id+"F0.wireOp",EDGE,"E160"),sQuery(id+"F0.wireOp",EDGE,"E161"),sQuery(id+"F0.wireOp",EDGE,"E162"),sQuery(id+"F0.wireOp",EDGE,"E163"),sQuery(id+"F0.wireOp",EDGE,"E164"),sQuery(id+"F0.wireOp",EDGE,"E165"),sQuery(id+"F0.wireOp",EDGE,"E280"),sQuery(id+"F0.wireOp",EDGE,"E286"),sQuery(id+"F0.wireOp",EDGE,"E287")])],"isStart":false});
            var sketch = newSketch(context, id + "F2", { "sketchPlane" : qUnion([Q0])});
            skLineSegment(sketch, "E288.bottom", {"start": v(-404.82, 391.65) * mm, "end": v(343.89, 391.65) * mm});
            skLineSegment(sketch, "E288.top", {"start": v(-404.82, -456.86) * mm, "end": v(343.89, -456.86) * mm});
            skLineSegment(sketch, "E288.left", {"start": v(-404.82, 391.65) * mm, "end": v(-404.82, -456.86) * mm});
            skLineSegment(sketch, "E288.right", {"start": v(343.89, 391.65) * mm, "end": v(343.89, -456.86) * mm});
            skSolve(sketch);
        }
        {
            var Q0;
            Q0=makeQuery(id+"F2.imprint","IMPRINT",FACE,{"disambiguationData":[TD([[makeQuery(id+"F2.imprint","IMPRINT",EDGE,{"derivedFrom":sQuery(id+"F2.wireOp",EDGE,"E288.bottom")}),-1.0]])]});
            extrude(context, id + "F3", {"entities" : qUnion([Q0]), "operationType" : NewBodyOperationType.REMOVE, "oppositeDirection" : true, "depth" : 25.4 * mm});
        }
        {
            var Q0;
            Q0=makeQuery(id+"F1.opExtrude","CAP_FACE",FACE,{"disambiguationData":[OSD([sQuery(id+"F0.wireOp",EDGE,"E0"),sQuery(id+"F0.wireOp",EDGE,"E1"),sQuery(id+"F0.wireOp",EDGE,"E2"),sQuery(id+"F0.wireOp",EDGE,"E3"),sQuery(id+"F0.wireOp",EDGE,"E4"),sQuery(id+"F0.wireOp",EDGE,"E5"),sQuery(id+"F0.wireOp",EDGE,"E6"),sQuery(id+"F0.wireOp",EDGE,"E7"),sQuery(id+"F0.wireOp",EDGE,"E8"),sQuery(id+"F0.wireOp",EDGE,"E9"),sQuery(id+"F0.wireOp",EDGE,"E10"),sQuery(id+"F0.wireOp",EDGE,"E11"),sQuery(id+"F0.wireOp",EDGE,"E12"),sQuery(id+"F0.wireOp",EDGE,"E13"),sQuery(id+"F0.wireOp",EDGE,"E14"),sQuery(id+"F0.wireOp",EDGE,"E15"),sQuery(id+"F0.wireOp",EDGE,"E16"),sQuery(id+"F0.wireOp",EDGE,"E17"),sQuery(id+"F0.wireOp",EDGE,"E18"),sQuery(id+"F0.wireOp",EDGE,"E19"),sQuery(id+"F0.wireOp",EDGE,"E20"),sQuery(id+"F0.wireOp",EDGE,"E21"),sQuery(id+"F0.wireOp",EDGE,"E22"),sQuery(id+"F0.wireOp",EDGE,"E23"),sQuery(id+"F0.wireOp",EDGE,"E24"),sQuery(id+"F0.wireOp",EDGE,"E25"),sQuery(id+"F0.wireOp",EDGE,"E26"),sQuery(id+"F0.wireOp",EDGE,"E27"),sQuery(id+"F0.wireOp",EDGE,"E28"),sQuery(id+"F0.wireOp",EDGE,"E29"),sQuery(id+"F0.wireOp",EDGE,"E30"),sQuery(id+"F0.wireOp",EDGE,"E31"),sQuery(id+"F0.wireOp",EDGE,"E32"),sQuery(id+"F0.wireOp",EDGE,"E33"),sQuery(id+"F0.wireOp",EDGE,"E34"),sQuery(id+"F0.wireOp",EDGE,"E35"),sQuery(id+"F0.wireOp",EDGE,"E36"),sQuery(id+"F0.wireOp",EDGE,"E37"),sQuery(id+"F0.wireOp",EDGE,"E38"),sQuery(id+"F0.wireOp",EDGE,"E39"),sQuery(id+"F0.wireOp",EDGE,"E40"),sQuery(id+"F0.wireOp",EDGE,"E41"),sQuery(id+"F0.wireOp",EDGE,"E42"),sQuery(id+"F0.wireOp",EDGE,"E43"),sQuery(id+"F0.wireOp",EDGE,"E44"),sQuery(id+"F0.wireOp",EDGE,"E45"),sQuery(id+"F0.wireOp",EDGE,"E46"),sQuery(id+"F0.wireOp",EDGE,"E47"),sQuery(id+"F0.wireOp",EDGE,"E48"),sQuery(id+"F0.wireOp",EDGE,"E49"),sQuery(id+"F0.wireOp",EDGE,"E50"),sQuery(id+"F0.wireOp",EDGE,"E51"),sQuery(id+"F0.wireOp",EDGE,"E52"),sQuery(id+"F0.wireOp",EDGE,"E53"),sQuery(id+"F0.wireOp",EDGE,"E54"),sQuery(id+"F0.wireOp",EDGE,"E55"),sQuery(id+"F0.wireOp",EDGE,"E56"),sQuery(id+"F0.wireOp",EDGE,"E57"),sQuery(id+"F0.wireOp",EDGE,"E58"),sQuery(id+"F0.wireOp",EDGE,"E59"),sQuery(id+"F0.wireOp",EDGE,"E60"),sQuery(id+"F0.wireOp",EDGE,"E61"),sQuery(id+"F0.wireOp",EDGE,"E62"),sQuery(id+"F0.wireOp",EDGE,"E63"),sQuery(id+"F0.wireOp",EDGE,"E64"),sQuery(id+"F0.wireOp",EDGE,"E65"),sQuery(id+"F0.wireOp",EDGE,"E66"),sQuery(id+"F0.wireOp",EDGE,"E67"),sQuery(id+"F0.wireOp",EDGE,"E68"),sQuery(id+"F0.wireOp",EDGE,"E69"),sQuery(id+"F0.wireOp",EDGE,"E70"),sQuery(id+"F0.wireOp",EDGE,"E71"),sQuery(id+"F0.wireOp",EDGE,"E72"),sQuery(id+"F0.wireOp",EDGE,"E73"),sQuery(id+"F0.wireOp",EDGE,"E74"),sQuery(id+"F0.wireOp",EDGE,"E75"),sQuery(id+"F0.wireOp",EDGE,"E76"),sQuery(id+"F0.wireOp",EDGE,"E283")])],"isStart":false});
            extrude(context, id + "F4", {"entities" : qUnion([Q0]), "operationType" : NewBodyOperationType.ADD, "depth" : 50.8 * mm});
        }
        {
            var Q0;
            Q0=makeQuery(id+"F1.opExtrude","CAP_FACE",FACE,{"disambiguationData":[OSD([sQuery(id+"F0.wireOp",EDGE,"E0"),sQuery(id+"F0.wireOp",EDGE,"E1"),sQuery(id+"F0.wireOp",EDGE,"E2"),sQuery(id+"F0.wireOp",EDGE,"E3"),sQuery(id+"F0.wireOp",EDGE,"E4"),sQuery(id+"F0.wireOp",EDGE,"E5"),sQuery(id+"F0.wireOp",EDGE,"E6"),sQuery(id+"F0.wireOp",EDGE,"E7"),sQuery(id+"F0.wireOp",EDGE,"E8"),sQuery(id+"F0.wireOp",EDGE,"E9"),sQuery(id+"F0.wireOp",EDGE,"E10"),sQuery(id+"F0.wireOp",EDGE,"E11"),sQuery(id+"F0.wireOp",EDGE,"E12"),sQuery(id+"F0.wireOp",EDGE,"E13"),sQuery(id+"F0.wireOp",EDGE,"E14"),sQuery(id+"F0.wireOp",EDGE,"E15"),sQuery(id+"F0.wireOp",EDGE,"E16"),sQuery(id+"F0.wireOp",EDGE,"E17"),sQuery(id+"F0.wireOp",EDGE,"E18"),sQuery(id+"F0.wireOp",EDGE,"E19"),sQuery(id+"F0.wireOp",EDGE,"E20"),sQuery(id+"F0.wireOp",EDGE,"E21"),sQuery(id+"F0.wireOp",EDGE,"E22"),sQuery(id+"F0.wireOp",EDGE,"E23"),sQuery(id+"F0.wireOp",EDGE,"E24"),sQuery(id+"F0.wireOp",EDGE,"E25"),sQuery(id+"F0.wireOp",EDGE,"E26"),sQuery(id+"F0.wireOp",EDGE,"E27"),sQuery(id+"F0.wireOp",EDGE,"E28"),sQuery(id+"F0.wireOp",EDGE,"E29"),sQuery(id+"F0.wireOp",EDGE,"E30"),sQuery(id+"F0.wireOp",EDGE,"E31"),sQuery(id+"F0.wireOp",EDGE,"E32"),sQuery(id+"F0.wireOp",EDGE,"E33"),sQuery(id+"F0.wireOp",EDGE,"E34"),sQuery(id+"F0.wireOp",EDGE,"E35"),sQuery(id+"F0.wireOp",EDGE,"E36"),sQuery(id+"F0.wireOp",EDGE,"E37"),sQuery(id+"F0.wireOp",EDGE,"E38"),sQuery(id+"F0.wireOp",EDGE,"E39"),sQuery(id+"F0.wireOp",EDGE,"E40"),sQuery(id+"F0.wireOp",EDGE,"E41"),sQuery(id+"F0.wireOp",EDGE,"E42"),sQuery(id+"F0.wireOp",EDGE,"E43"),sQuery(id+"F0.wireOp",EDGE,"E44"),sQuery(id+"F0.wireOp",EDGE,"E45"),sQuery(id+"F0.wireOp",EDGE,"E46"),sQuery(id+"F0.wireOp",EDGE,"E47"),sQuery(id+"F0.wireOp",EDGE,"E48"),sQuery(id+"F0.wireOp",EDGE,"E49"),sQuery(id+"F0.wireOp",EDGE,"E50"),sQuery(id+"F0.wireOp",EDGE,"E51"),sQuery(id+"F0.wireOp",EDGE,"E52"),sQuery(id+"F0.wireOp",EDGE,"E53"),sQuery(id+"F0.wireOp",EDGE,"E54"),sQuery(id+"F0.wireOp",EDGE,"E55"),sQuery(id+"F0.wireOp",EDGE,"E56"),sQuery(id+"F0.wireOp",EDGE,"E57"),sQuery(id+"F0.wireOp",EDGE,"E58"),sQuery(id+"F0.wireOp",EDGE,"E59"),sQuery(id+"F0.wireOp",EDGE,"E60"),sQuery(id+"F0.wireOp",EDGE,"E61"),sQuery(id+"F0.wireOp",EDGE,"E62"),sQuery(id+"F0.wireOp",EDGE,"E63"),sQuery(id+"F0.wireOp",EDGE,"E64"),sQuery(id+"F0.wireOp",EDGE,"E65"),sQuery(id+"F0.wireOp",EDGE,"E66"),sQuery(id+"F0.wireOp",EDGE,"E67"),sQuery(id+"F0.wireOp",EDGE,"E68"),sQuery(id+"F0.wireOp",EDGE,"E69"),sQuery(id+"F0.wireOp",EDGE,"E70"),sQuery(id+"F0.wireOp",EDGE,"E71"),sQuery(id+"F0.wireOp",EDGE,"E72"),sQuery(id+"F0.wireOp",EDGE,"E73"),sQuery(id+"F0.wireOp",EDGE,"E74"),sQuery(id+"F0.wireOp",EDGE,"E75"),sQuery(id+"F0.wireOp",EDGE,"E76"),sQuery(id+"F0.wireOp",EDGE,"E283")])],"isStart":true});
            extrude(context, id + "F5", {"entities" : qUnion([Q0]), "operationType" : NewBodyOperationType.REMOVE, "oppositeDirection" : true, "depth" : 50.8 * mm});
        }
        {
            var Q0;
            Q0=makeQuery(id+"F1.opExtrude","CAP_FACE",FACE,{"disambiguationData":[OSD([sQuery(id+"F0.wireOp",EDGE,"E77"),sQuery(id+"F0.wireOp",EDGE,"E78"),sQuery(id+"F0.wireOp",EDGE,"E79"),sQuery(id+"F0.wireOp",EDGE,"E80"),sQuery(id+"F0.wireOp",EDGE,"E81"),sQuery(id+"F0.wireOp",EDGE,"E82"),sQuery(id+"F0.wireOp",EDGE,"E83"),sQuery(id+"F0.wireOp",EDGE,"E84"),sQuery(id+"F0.wireOp",EDGE,"E85"),sQuery(id+"F0.wireOp",EDGE,"E86"),sQuery(id+"F0.wireOp",EDGE,"E87"),sQuery(id+"F0.wireOp",EDGE,"E88"),sQuery(id+"F0.wireOp",EDGE,"E89"),sQuery(id+"F0.wireOp",EDGE,"E90"),sQuery(id+"F0.wireOp",EDGE,"E91"),sQuery(id+"F0.wireOp",EDGE,"E92"),sQuery(id+"F0.wireOp",EDGE,"E93"),sQuery(id+"F0.wireOp",EDGE,"E94"),sQuery(id+"F0.wireOp",EDGE,"E95"),sQuery(id+"F0.wireOp",EDGE,"E96"),sQuery(id+"F0.wireOp",EDGE,"E97"),sQuery(id+"F0.wireOp",EDGE,"E98"),sQuery(id+"F0.wireOp",EDGE,"E99"),sQuery(id+"F0.wireOp",EDGE,"E100"),sQuery(id+"F0.wireOp",EDGE,"E102"),sQuery(id+"F0.wireOp",EDGE,"E103"),sQuery(id+"F0.wireOp",EDGE,"E104"),sQuery(id+"F0.wireOp",EDGE,"E105"),sQuery(id+"F0.wireOp",EDGE,"E106"),sQuery(id+"F0.wireOp",EDGE,"E107"),sQuery(id+"F0.wireOp",EDGE,"E108"),sQuery(id+"F0.wireOp",EDGE,"E109"),sQuery(id+"F0.wireOp",EDGE,"E110"),sQuery(id+"F0.wireOp",EDGE,"E111"),sQuery(id+"F0.wireOp",EDGE,"E112"),sQuery(id+"F0.wireOp",EDGE,"E113"),sQuery(id+"F0.wireOp",EDGE,"E114"),sQuery(id+"F0.wireOp",EDGE,"E115"),sQuery(id+"F0.wireOp",EDGE,"E116"),sQuery(id+"F0.wireOp",EDGE,"E117"),sQuery(id+"F0.wireOp",EDGE,"E118"),sQuery(id+"F0.wireOp",EDGE,"E119"),sQuery(id+"F0.wireOp",EDGE,"E120"),sQuery(id+"F0.wireOp",EDGE,"E121"),sQuery(id+"F0.wireOp",EDGE,"E122"),sQuery(id+"F0.wireOp",EDGE,"E123"),sQuery(id+"F0.wireOp",EDGE,"E124"),sQuery(id+"F0.wireOp",EDGE,"E125"),sQuery(id+"F0.wireOp",EDGE,"E126"),sQuery(id+"F0.wireOp",EDGE,"E127"),sQuery(id+"F0.wireOp",EDGE,"E128"),sQuery(id+"F0.wireOp",EDGE,"E129"),sQuery(id+"F0.wireOp",EDGE,"E130"),sQuery(id+"F0.wireOp",EDGE,"E131"),sQuery(id+"F0.wireOp",EDGE,"E132"),sQuery(id+"F0.wireOp",EDGE,"E133"),sQuery(id+"F0.wireOp",EDGE,"E134"),sQuery(id+"F0.wireOp",EDGE,"E135"),sQuery(id+"F0.wireOp",EDGE,"E136"),sQuery(id+"F0.wireOp",EDGE,"E137"),sQuery(id+"F0.wireOp",EDGE,"E138"),sQuery(id+"F0.wireOp",EDGE,"E139"),sQuery(id+"F0.wireOp",EDGE,"E140"),sQuery(id+"F0.wireOp",EDGE,"E141"),sQuery(id+"F0.wireOp",EDGE,"E142"),sQuery(id+"F0.wireOp",EDGE,"E143"),sQuery(id+"F0.wireOp",EDGE,"E144"),sQuery(id+"F0.wireOp",EDGE,"E145"),sQuery(id+"F0.wireOp",EDGE,"E146"),sQuery(id+"F0.wireOp",EDGE,"E147"),sQuery(id+"F0.wireOp",EDGE,"E148"),sQuery(id+"F0.wireOp",EDGE,"E149"),sQuery(id+"F0.wireOp",EDGE,"E150"),sQuery(id+"F0.wireOp",EDGE,"E151"),sQuery(id+"F0.wireOp",EDGE,"E152"),sQuery(id+"F0.wireOp",EDGE,"E153"),sQuery(id+"F0.wireOp",EDGE,"E154"),sQuery(id+"F0.wireOp",EDGE,"E155"),sQuery(id+"F0.wireOp",EDGE,"E156"),sQuery(id+"F0.wireOp",EDGE,"E157"),sQuery(id+"F0.wireOp",EDGE,"E158"),sQuery(id+"F0.wireOp",EDGE,"E159"),sQuery(id+"F0.wireOp",EDGE,"E160"),sQuery(id+"F0.wireOp",EDGE,"E161"),sQuery(id+"F0.wireOp",EDGE,"E162"),sQuery(id+"F0.wireOp",EDGE,"E163"),sQuery(id+"F0.wireOp",EDGE,"E164"),sQuery(id+"F0.wireOp",EDGE,"E165"),sQuery(id+"F0.wireOp",EDGE,"E280"),sQuery(id+"F0.wireOp",EDGE,"E286"),sQuery(id+"F0.wireOp",EDGE,"E287")])],"isStart":false});
            var sketch = newSketch(context, id + "F6", { "sketchPlane" : qUnion([Q0])});
            skPoint(sketch, "E289.0", {"position": v(-483.06, 327.18) * mm});
            skLineSegment(sketch, "E290.0", {"start": v(-1282.57, -482.26) * mm, "end": v(-1282.57, 417.17) * mm, "construction": true});
            skLineSegment(sketch, "E291", {"start": v(258.58, 391.65) * mm, "end": v(-1432.12, 391.65) * mm, "construction": true});
            skLineSegment(sketch, "E292", {"start": v(-1432.12, 391.65) * mm, "end": v(-1432.12, -456.86) * mm, "construction": true});
            skLineSegment(sketch, "E293", {"start": v(-1741.89, -482.26) * mm, "end": v(-454.2, -482.15) * mm, "construction": true});
            skLineSegment(sketch, "E294", {"start": v(393.28, -482.15) * mm, "end": v(1315.4, -482.15) * mm, "construction": true});
            skLineSegment(sketch, "E295", {"start": v(467.25, -412.3) * mm, "end": v(1310.36, -412.3) * mm, "construction": true});
            skLineSegment(sketch, "E296", {"start": v(452.15, -284.28) * mm, "end": v(1322.95, -284.28) * mm, "construction": true});
            skLineSegment(sketch, "E297.0", {"start": v(1221.65, -482.26) * mm, "end": v(1221.65, 417.17) * mm, "construction": true});
            skLineSegment(sketch, "E298.bottom", {"start": v(1221.65, -284.28) * mm, "end": v(1023.6, -284.28) * mm});
            skLineSegment(sketch, "E298.top", {"start": v(1221.65, -298) * mm, "end": v(1023.6, -298) * mm});
            skLineSegment(sketch, "E298.left", {"start": v(1221.65, -284.28) * mm, "end": v(1221.65, -298) * mm});
            skLineSegment(sketch, "E298.right", {"start": v(1023.6, -284.28) * mm, "end": v(1023.6, -298) * mm});
            skLineSegment(sketch, "E299.0", {"start": v(422.13, -362.36) * mm, "end": v(422.13, -422.19) * mm, "construction": true});
            skLineSegment(sketch, "E300", {"start": v(422.13, -543.81) * mm, "end": v(422.13, 940.41) * mm, "construction": true});
            skLineSegment(sketch, "E301", {"start": v(442.93, -201.73) * mm, "end": v(1364.84, -201.73) * mm, "construction": true});
            skLineSegment(sketch, "E302.bottom", {"start": v(1221.65, -201.73) * mm, "end": v(1046.47, -201.73) * mm});
            skLineSegment(sketch, "E302.top", {"start": v(1221.65, -215.45) * mm, "end": v(1046.47, -215.45) * mm});
            skLineSegment(sketch, "E302.left", {"start": v(1221.65, -201.73) * mm, "end": v(1221.65, -215.45) * mm});
            skLineSegment(sketch, "E302.right", {"start": v(1046.47, -201.73) * mm, "end": v(1046.47, -215.45) * mm});
            skLineSegment(sketch, "E303", {"start": v(477.58, -119.18) * mm, "end": v(1255.92, -119.18) * mm, "construction": true});
            skLineSegment(sketch, "E304", {"start": v(468.8, -36.63) * mm, "end": v(1435.65, -36.63) * mm, "construction": true});
            skLineSegment(sketch, "E305", {"start": v(462.03, 45.92) * mm, "end": v(1395.08, 45.92) * mm, "construction": true});
            skLineSegment(sketch, "E306", {"start": v(455.27, 128.47) * mm, "end": v(1408.6, 128.47) * mm, "construction": true});
            skLineSegment(sketch, "E307.bottom", {"start": v(1221.65, -119.18) * mm, "end": v(980.43, -119.18) * mm});
            skLineSegment(sketch, "E307.top", {"start": v(1221.65, -132.9) * mm, "end": v(980.43, -132.9) * mm});
            skLineSegment(sketch, "E307.left", {"start": v(1221.65, -119.18) * mm, "end": v(1221.65, -132.9) * mm});
            skLineSegment(sketch, "E307.right", {"start": v(980.43, -119.18) * mm, "end": v(980.43, -132.9) * mm});
            skLineSegment(sketch, "E308.bottom", {"start": v(1221.65, -36.63) * mm, "end": v(884.67, -36.63) * mm});
            skLineSegment(sketch, "E308.top", {"start": v(1221.65, -50.35) * mm, "end": v(884.67, -50.35) * mm});
            skLineSegment(sketch, "E308.left", {"start": v(1221.65, -36.63) * mm, "end": v(1221.65, -50.35) * mm});
            skLineSegment(sketch, "E308.right", {"start": v(884.67, -36.63) * mm, "end": v(884.67, -50.35) * mm});
            skLineSegment(sketch, "E309.bottom", {"start": v(1221.65, 45.92) * mm, "end": v(809.48, 45.92) * mm});
            skLineSegment(sketch, "E309.top", {"start": v(1221.65, 32.2) * mm, "end": v(809.48, 32.2) * mm});
            skLineSegment(sketch, "E309.left", {"start": v(1221.65, 45.92) * mm, "end": v(1221.65, 32.2) * mm});
            skLineSegment(sketch, "E309.right", {"start": v(809.48, 45.92) * mm, "end": v(809.48, 32.2) * mm});
            skLineSegment(sketch, "E310.bottom", {"start": v(1221.65, 128.47) * mm, "end": v(737.6, 128.47) * mm});
            skLineSegment(sketch, "E310.top", {"start": v(1221.65, 114.75) * mm, "end": v(737.6, 114.75) * mm});
            skLineSegment(sketch, "E310.left", {"start": v(1221.65, 128.47) * mm, "end": v(1221.65, 114.75) * mm});
            skLineSegment(sketch, "E310.right", {"start": v(737.6, 128.47) * mm, "end": v(737.6, 114.75) * mm});
            skSolve(sketch);
        }
        {
            var Q0;
            Q0=makeQuery(id+"F6.imprint","IMPRINT",FACE,{"disambiguationData":[TD([[makeQuery(id+"F6.imprint","IMPRINT",EDGE,{"derivedFrom":sQuery(id+"F6.wireOp",EDGE,"E310.bottom")}),1.0]])]});
            var Q1;
            Q1=makeQuery(id+"F6.imprint","IMPRINT",FACE,{"disambiguationData":[TD([[makeQuery(id+"F6.imprint","IMPRINT",EDGE,{"derivedFrom":sQuery(id+"F6.wireOp",EDGE,"E309.bottom")}),1.0]])]});
            var Q2;
            Q2=makeQuery(id+"F6.imprint","IMPRINT",FACE,{"disambiguationData":[TD([[makeQuery(id+"F6.imprint","IMPRINT",EDGE,{"derivedFrom":sQuery(id+"F6.wireOp",EDGE,"E308.bottom")}),1.0]])]});
            var Q3;
            Q3=makeQuery(id+"F6.imprint","IMPRINT",FACE,{"disambiguationData":[TD([[makeQuery(id+"F6.imprint","IMPRINT",EDGE,{"derivedFrom":sQuery(id+"F6.wireOp",EDGE,"E307.bottom")}),1.0]])]});
            var Q4;
            Q4=makeQuery(id+"F6.imprint","IMPRINT",FACE,{"disambiguationData":[TD([[makeQuery(id+"F6.imprint","IMPRINT",EDGE,{"derivedFrom":sQuery(id+"F6.wireOp",EDGE,"E302.bottom")}),1.0]])]});
            var Q5;
            Q5=makeQuery(id+"F6.imprint","IMPRINT",FACE,{"disambiguationData":[TD([[makeQuery(id+"F6.imprint","IMPRINT",EDGE,{"derivedFrom":sQuery(id+"F6.wireOp",EDGE,"E298.bottom")}),1.0]])]});
            extrude(context, id + "F7", {"entities" : qUnion([Q0, Q1, Q2, Q3, Q4, Q5]), "operationType" : NewBodyOperationType.REMOVE, "oppositeDirection" : true, "depth" : 25.4 * mm});
        }
        {
            var Q0;
            Q0=makeQuery(id+"F1.opExtrude","CAP_FACE",FACE,{"disambiguationData":[OSD([sQuery(id+"F0.wireOp",EDGE,"E167"),sQuery(id+"F0.wireOp",EDGE,"E168"),sQuery(id+"F0.wireOp",EDGE,"E169"),sQuery(id+"F0.wireOp",EDGE,"E170"),sQuery(id+"F0.wireOp",EDGE,"E171"),sQuery(id+"F0.wireOp",EDGE,"E172"),sQuery(id+"F0.wireOp",EDGE,"E173"),sQuery(id+"F0.wireOp",EDGE,"E174"),sQuery(id+"F0.wireOp",EDGE,"E175"),sQuery(id+"F0.wireOp",EDGE,"E176"),sQuery(id+"F0.wireOp",EDGE,"E177"),sQuery(id+"F0.wireOp",EDGE,"E178"),sQuery(id+"F0.wireOp",EDGE,"E179"),sQuery(id+"F0.wireOp",EDGE,"E180"),sQuery(id+"F0.wireOp",EDGE,"E181"),sQuery(id+"F0.wireOp",EDGE,"E182"),sQuery(id+"F0.wireOp",EDGE,"E183"),sQuery(id+"F0.wireOp",EDGE,"E184"),sQuery(id+"F0.wireOp",EDGE,"E185"),sQuery(id+"F0.wireOp",EDGE,"E186"),sQuery(id+"F0.wireOp",EDGE,"E187"),sQuery(id+"F0.wireOp",EDGE,"E188"),sQuery(id+"F0.wireOp",EDGE,"E189"),sQuery(id+"F0.wireOp",EDGE,"E190"),sQuery(id+"F0.wireOp",EDGE,"E191"),sQuery(id+"F0.wireOp",EDGE,"E192"),sQuery(id+"F0.wireOp",EDGE,"E193"),sQuery(id+"F0.wireOp",EDGE,"E194"),sQuery(id+"F0.wireOp",EDGE,"E195"),sQuery(id+"F0.wireOp",EDGE,"E196"),sQuery(id+"F0.wireOp",EDGE,"E197"),sQuery(id+"F0.wireOp",EDGE,"E198"),sQuery(id+"F0.wireOp",EDGE,"E199"),sQuery(id+"F0.wireOp",EDGE,"E200"),sQuery(id+"F0.wireOp",EDGE,"E201"),sQuery(id+"F0.wireOp",EDGE,"E202"),sQuery(id+"F0.wireOp",EDGE,"E203"),sQuery(id+"F0.wireOp",EDGE,"E204"),sQuery(id+"F0.wireOp",EDGE,"E205"),sQuery(id+"F0.wireOp",EDGE,"E206"),sQuery(id+"F0.wireOp",EDGE,"E207"),sQuery(id+"F0.wireOp",EDGE,"E208"),sQuery(id+"F0.wireOp",EDGE,"E209"),sQuery(id+"F0.wireOp",EDGE,"E210"),sQuery(id+"F0.wireOp",EDGE,"E211"),sQuery(id+"F0.wireOp",EDGE,"E212"),sQuery(id+"F0.wireOp",EDGE,"E213"),sQuery(id+"F0.wireOp",EDGE,"E214"),sQuery(id+"F0.wireOp",EDGE,"E215"),sQuery(id+"F0.wireOp",EDGE,"E216"),sQuery(id+"F0.wireOp",EDGE,"E217"),sQuery(id+"F0.wireOp",EDGE,"E218"),sQuery(id+"F0.wireOp",EDGE,"E219"),sQuery(id+"F0.wireOp",EDGE,"E220"),sQuery(id+"F0.wireOp",EDGE,"E221"),sQuery(id+"F0.wireOp",EDGE,"E278"),sQuery(id+"F0.wireOp",EDGE,"E279")])],"isStart":false});
            var sketch = newSketch(context, id + "F8", { "sketchPlane" : qUnion([Q0])});
            skPoint(sketch, "E311.0", {"position": v(-1282.57, 417.17) * mm});
            skPoint(sketch, "E312.0", {"position": v(1221.65, 417.17) * mm});
            skLineSegment(sketch, "E313.bottom", {"start": v(-1282.57, 417.17) * mm, "end": v(1221.65, 417.17) * mm, "construction": true});
            skLineSegment(sketch, "E313.top", {"start": v(-1282.57, -1005.02) * mm, "end": v(1221.65, -1005.02) * mm, "construction": true});
            skLineSegment(sketch, "E313.left", {"start": v(-1282.57, 417.17) * mm, "end": v(-1282.57, -1005.02) * mm, "construction": true});
            skLineSegment(sketch, "E313.right", {"start": v(1221.65, 417.17) * mm, "end": v(1221.65, -1005.02) * mm, "construction": true});
            skLineSegment(sketch, "E314", {"start": v(-30.46, 417.17) * mm, "end": v(-30.46, -1507.86) * mm, "construction": true});
            skPoint(sketch, "E314.endSnap0", {"position": v(-30.46, -1005.02) * mm});
            skLineSegment(sketch, "E315.0", {"start": v(1221.65, 128.47) * mm, "end": v(737.6, 128.47) * mm});
            skLineSegment(sketch, "E316.0", {"start": v(1221.65, 114.75) * mm, "end": v(737.6, 114.75) * mm});
            skLineSegment(sketch, "E317.0", {"start": v(737.6, 128.47) * mm, "end": v(737.6, 114.75) * mm});
            skLineSegment(sketch, "E318.0", {"start": v(1221.65, 45.92) * mm, "end": v(809.48, 45.92) * mm});
            skLineSegment(sketch, "E319.0", {"start": v(809.48, 45.92) * mm, "end": v(809.48, 32.2) * mm});
            skLineSegment(sketch, "E320.0", {"start": v(1221.65, 32.2) * mm, "end": v(809.48, 32.2) * mm});
            skLineSegment(sketch, "E321.0", {"start": v(1221.65, -36.63) * mm, "end": v(884.67, -36.63) * mm});
            skLineSegment(sketch, "E322.0", {"start": v(1221.65, -50.35) * mm, "end": v(884.67, -50.35) * mm});
            skLineSegment(sketch, "E323.0", {"start": v(884.67, -36.63) * mm, "end": v(884.67, -50.35) * mm});
            skLineSegment(sketch, "E324.0", {"start": v(1221.65, -119.18) * mm, "end": v(980.43, -119.18) * mm});
            skLineSegment(sketch, "E325.0", {"start": v(1221.65, -132.9) * mm, "end": v(980.43, -132.9) * mm});
            skLineSegment(sketch, "E326.0", {"start": v(980.43, -119.18) * mm, "end": v(980.43, -132.9) * mm});
            skLineSegment(sketch, "E327.0", {"start": v(1221.65, -201.73) * mm, "end": v(1046.47, -201.73) * mm});
            skLineSegment(sketch, "E328.0", {"start": v(1046.47, -201.73) * mm, "end": v(1046.47, -215.45) * mm});
            skLineSegment(sketch, "E329.0", {"start": v(1221.65, -215.45) * mm, "end": v(1046.47, -215.45) * mm});
            skLineSegment(sketch, "E330.0", {"start": v(1221.65, -298) * mm, "end": v(1023.6, -298) * mm});
            skLineSegment(sketch, "E331.0", {"start": v(1221.65, -284.28) * mm, "end": v(1023.6, -284.28) * mm});
            skLineSegment(sketch, "E332.0", {"start": v(1023.6, -284.28) * mm, "end": v(1023.6, -298) * mm});
            skLineSegment(sketch, "E333.MirrorCS", {"start": v(-1282.57, 128.47) * mm, "end": v(-798.52, 128.47) * mm});
            skLineSegment(sketch, "E334.MirrorCS", {"start": v(-1282.57, 114.75) * mm, "end": v(-798.52, 114.75) * mm});
            skLineSegment(sketch, "E335.MirrorCS", {"start": v(-798.52, 128.47) * mm, "end": v(-798.52, 114.75) * mm});
            skLineSegment(sketch, "E336.MirrorCS", {"start": v(-1282.57, 45.92) * mm, "end": v(-870.4, 45.92) * mm});
            skLineSegment(sketch, "E337.MirrorCS", {"start": v(-870.4, 45.92) * mm, "end": v(-870.4, 32.2) * mm});
            skLineSegment(sketch, "E338.MirrorCS", {"start": v(-1282.57, 32.2) * mm, "end": v(-870.4, 32.2) * mm});
            skLineSegment(sketch, "E339.MirrorCS", {"start": v(-1282.57, -36.63) * mm, "end": v(-945.59, -36.63) * mm});
            skLineSegment(sketch, "E340.MirrorCS", {"start": v(-1282.57, -50.35) * mm, "end": v(-945.59, -50.35) * mm});
            skLineSegment(sketch, "E341.MirrorCS", {"start": v(-945.59, -36.63) * mm, "end": v(-945.59, -50.35) * mm});
            skLineSegment(sketch, "E342.MirrorCS", {"start": v(-1041.35, -119.18) * mm, "end": v(-1041.35, -132.9) * mm});
            skLineSegment(sketch, "E343.MirrorCS", {"start": v(-1282.57, -119.18) * mm, "end": v(-1041.35, -119.18) * mm});
            skLineSegment(sketch, "E344.MirrorCS", {"start": v(-1282.57, -132.9) * mm, "end": v(-1041.35, -132.9) * mm});
            skLineSegment(sketch, "E345.MirrorCS", {"start": v(-1282.57, -201.73) * mm, "end": v(-1107.39, -201.73) * mm});
            skLineSegment(sketch, "E346.MirrorCS", {"start": v(-1282.57, -215.45) * mm, "end": v(-1107.39, -215.45) * mm});
            skLineSegment(sketch, "E347.MirrorCS", {"start": v(-1107.39, -201.73) * mm, "end": v(-1107.39, -215.45) * mm});
            skLineSegment(sketch, "E348.MirrorCS", {"start": v(-1084.53, -284.28) * mm, "end": v(-1084.53, -298) * mm});
            skLineSegment(sketch, "E349.MirrorCS", {"start": v(-1282.57, -298) * mm, "end": v(-1084.53, -298) * mm});
            skLineSegment(sketch, "E350.MirrorCS", {"start": v(-1282.57, -284.28) * mm, "end": v(-1084.53, -284.28) * mm});
            skLineSegment(sketch, "E351", {"start": v(-1282.57, -284.28) * mm, "end": v(-1282.57, -298) * mm});
            skLineSegment(sketch, "E352", {"start": v(-1282.57, -201.73) * mm, "end": v(-1282.57, -215.45) * mm});
            skLineSegment(sketch, "E353", {"start": v(-1282.57, -132.9) * mm, "end": v(-1282.57, -119.18) * mm});
            skLineSegment(sketch, "E354", {"start": v(-1282.57, -50.35) * mm, "end": v(-1282.57, -36.63) * mm});
            skLineSegment(sketch, "E355", {"start": v(-1282.57, 32.2) * mm, "end": v(-1282.57, 45.92) * mm});
            skLineSegment(sketch, "E356", {"start": v(-1282.57, 128.47) * mm, "end": v(-1282.57, 114.75) * mm});
            skSolve(sketch);
        }
        {
            var Q0;
            Q0=makeQuery(id+"F8.imprint","IMPRINT",FACE,{"disambiguationData":[TD([[makeQuery(id+"F8.imprint","IMPRINT",EDGE,{"derivedFrom":sQuery(id+"F8.wireOp",EDGE,"E333.MirrorCS")}),-1.0]])]});
            var Q1;
            Q1=makeQuery(id+"F8.imprint","IMPRINT",FACE,{"disambiguationData":[TD([[makeQuery(id+"F8.imprint","IMPRINT",EDGE,{"derivedFrom":sQuery(id+"F8.wireOp",EDGE,"E336.MirrorCS")}),-1.0]])]});
            var Q2;
            Q2=makeQuery(id+"F8.imprint","IMPRINT",FACE,{"disambiguationData":[TD([[makeQuery(id+"F8.imprint","IMPRINT",EDGE,{"derivedFrom":sQuery(id+"F8.wireOp",EDGE,"E342.MirrorCS")}),-1.0]])]});
            var Q3;
            Q3=makeQuery(id+"F8.imprint","IMPRINT",FACE,{"disambiguationData":[TD([[makeQuery(id+"F8.imprint","IMPRINT",EDGE,{"derivedFrom":sQuery(id+"F8.wireOp",EDGE,"E339.MirrorCS")}),-1.0]])]});
            var Q4;
            Q4=makeQuery(id+"F8.imprint","IMPRINT",FACE,{"disambiguationData":[TD([[makeQuery(id+"F8.imprint","IMPRINT",EDGE,{"derivedFrom":sQuery(id+"F8.wireOp",EDGE,"E345.MirrorCS")}),-1.0]])]});
            var Q5;
            Q5=makeQuery(id+"F8.imprint","IMPRINT",FACE,{"disambiguationData":[TD([[makeQuery(id+"F8.imprint","IMPRINT",EDGE,{"derivedFrom":sQuery(id+"F8.wireOp",EDGE,"E348.MirrorCS")}),-1.0]])]});
            extrude(context, id + "F9", {"entities" : qUnion([Q0, Q1, Q2, Q3, Q4, Q5]), "operationType" : NewBodyOperationType.REMOVE, "oppositeDirection" : true, "depth" : 25.4 * mm});
        }
        {
            var Q0;
            Q0=makeQuery(id+"F1.opExtrude","CAP_FACE",FACE,{"disambiguationData":[OSD([sQuery(id+"F0.wireOp",EDGE,"E77"),sQuery(id+"F0.wireOp",EDGE,"E78"),sQuery(id+"F0.wireOp",EDGE,"E79"),sQuery(id+"F0.wireOp",EDGE,"E80"),sQuery(id+"F0.wireOp",EDGE,"E81"),sQuery(id+"F0.wireOp",EDGE,"E82"),sQuery(id+"F0.wireOp",EDGE,"E83"),sQuery(id+"F0.wireOp",EDGE,"E84"),sQuery(id+"F0.wireOp",EDGE,"E85"),sQuery(id+"F0.wireOp",EDGE,"E86"),sQuery(id+"F0.wireOp",EDGE,"E87"),sQuery(id+"F0.wireOp",EDGE,"E88"),sQuery(id+"F0.wireOp",EDGE,"E89"),sQuery(id+"F0.wireOp",EDGE,"E90"),sQuery(id+"F0.wireOp",EDGE,"E91"),sQuery(id+"F0.wireOp",EDGE,"E92"),sQuery(id+"F0.wireOp",EDGE,"E93"),sQuery(id+"F0.wireOp",EDGE,"E94"),sQuery(id+"F0.wireOp",EDGE,"E95"),sQuery(id+"F0.wireOp",EDGE,"E96"),sQuery(id+"F0.wireOp",EDGE,"E97"),sQuery(id+"F0.wireOp",EDGE,"E98"),sQuery(id+"F0.wireOp",EDGE,"E99"),sQuery(id+"F0.wireOp",EDGE,"E100"),sQuery(id+"F0.wireOp",EDGE,"E102"),sQuery(id+"F0.wireOp",EDGE,"E103"),sQuery(id+"F0.wireOp",EDGE,"E104"),sQuery(id+"F0.wireOp",EDGE,"E105"),sQuery(id+"F0.wireOp",EDGE,"E106"),sQuery(id+"F0.wireOp",EDGE,"E107"),sQuery(id+"F0.wireOp",EDGE,"E108"),sQuery(id+"F0.wireOp",EDGE,"E109"),sQuery(id+"F0.wireOp",EDGE,"E110"),sQuery(id+"F0.wireOp",EDGE,"E111"),sQuery(id+"F0.wireOp",EDGE,"E112"),sQuery(id+"F0.wireOp",EDGE,"E113"),sQuery(id+"F0.wireOp",EDGE,"E114"),sQuery(id+"F0.wireOp",EDGE,"E115"),sQuery(id+"F0.wireOp",EDGE,"E116"),sQuery(id+"F0.wireOp",EDGE,"E117"),sQuery(id+"F0.wireOp",EDGE,"E118"),sQuery(id+"F0.wireOp",EDGE,"E119"),sQuery(id+"F0.wireOp",EDGE,"E120"),sQuery(id+"F0.wireOp",EDGE,"E121"),sQuery(id+"F0.wireOp",EDGE,"E122"),sQuery(id+"F0.wireOp",EDGE,"E123"),sQuery(id+"F0.wireOp",EDGE,"E124"),sQuery(id+"F0.wireOp",EDGE,"E125"),sQuery(id+"F0.wireOp",EDGE,"E126"),sQuery(id+"F0.wireOp",EDGE,"E127"),sQuery(id+"F0.wireOp",EDGE,"E128"),sQuery(id+"F0.wireOp",EDGE,"E129"),sQuery(id+"F0.wireOp",EDGE,"E130"),sQuery(id+"F0.wireOp",EDGE,"E131"),sQuery(id+"F0.wireOp",EDGE,"E132"),sQuery(id+"F0.wireOp",EDGE,"E133"),sQuery(id+"F0.wireOp",EDGE,"E134"),sQuery(id+"F0.wireOp",EDGE,"E135"),sQuery(id+"F0.wireOp",EDGE,"E136"),sQuery(id+"F0.wireOp",EDGE,"E137"),sQuery(id+"F0.wireOp",EDGE,"E138"),sQuery(id+"F0.wireOp",EDGE,"E139"),sQuery(id+"F0.wireOp",EDGE,"E140"),sQuery(id+"F0.wireOp",EDGE,"E141"),sQuery(id+"F0.wireOp",EDGE,"E142"),sQuery(id+"F0.wireOp",EDGE,"E143"),sQuery(id+"F0.wireOp",EDGE,"E144"),sQuery(id+"F0.wireOp",EDGE,"E145"),sQuery(id+"F0.wireOp",EDGE,"E146"),sQuery(id+"F0.wireOp",EDGE,"E147"),sQuery(id+"F0.wireOp",EDGE,"E148"),sQuery(id+"F0.wireOp",EDGE,"E149"),sQuery(id+"F0.wireOp",EDGE,"E150"),sQuery(id+"F0.wireOp",EDGE,"E151"),sQuery(id+"F0.wireOp",EDGE,"E152"),sQuery(id+"F0.wireOp",EDGE,"E153"),sQuery(id+"F0.wireOp",EDGE,"E154"),sQuery(id+"F0.wireOp",EDGE,"E155"),sQuery(id+"F0.wireOp",EDGE,"E156"),sQuery(id+"F0.wireOp",EDGE,"E157"),sQuery(id+"F0.wireOp",EDGE,"E158"),sQuery(id+"F0.wireOp",EDGE,"E159"),sQuery(id+"F0.wireOp",EDGE,"E160"),sQuery(id+"F0.wireOp",EDGE,"E161"),sQuery(id+"F0.wireOp",EDGE,"E162"),sQuery(id+"F0.wireOp",EDGE,"E163"),sQuery(id+"F0.wireOp",EDGE,"E164"),sQuery(id+"F0.wireOp",EDGE,"E165"),sQuery(id+"F0.wireOp",EDGE,"E280"),sQuery(id+"F0.wireOp",EDGE,"E286"),sQuery(id+"F0.wireOp",EDGE,"E287")])],"isStart":false});
            var sketch = newSketch(context, id + "F10", { "sketchPlane" : qUnion([Q0])});
            skLineSegment(sketch, "E357", {"start": v(-357.15, 417.05) * mm, "end": v(-368.61, -482.26) * mm});
            skLineSegment(sketch, "E358", {"start": v(-454.2, 297.14) * mm, "end": v(393.28, 297.14) * mm, "construction": true});
            skLineSegment(sketch, "E359", {"start": v(372.95, -506.25) * mm, "end": v(372.95, -482.15) * mm, "construction": true});
            skLineSegment(sketch, "E360", {"start": v(369.29, -422.3) * mm, "end": v(343.89, -422.3) * mm, "construction": true});
            skSolve(sketch);
        }
        {
            var Q0;
            Q0=makeQuery(id+"F4.opExtrude","CAP_FACE",FACE,{"disambiguationData":[OSD([sQuery(id+"F0.wireOp",EDGE,"E0"),sQuery(id+"F0.wireOp",EDGE,"E1"),sQuery(id+"F0.wireOp",EDGE,"E2"),sQuery(id+"F0.wireOp",EDGE,"E3"),sQuery(id+"F0.wireOp",EDGE,"E4"),sQuery(id+"F0.wireOp",EDGE,"E5"),sQuery(id+"F0.wireOp",EDGE,"E6"),sQuery(id+"F0.wireOp",EDGE,"E7"),sQuery(id+"F0.wireOp",EDGE,"E8"),sQuery(id+"F0.wireOp",EDGE,"E9"),sQuery(id+"F0.wireOp",EDGE,"E10"),sQuery(id+"F0.wireOp",EDGE,"E11"),sQuery(id+"F0.wireOp",EDGE,"E12"),sQuery(id+"F0.wireOp",EDGE,"E13"),sQuery(id+"F0.wireOp",EDGE,"E14"),sQuery(id+"F0.wireOp",EDGE,"E15"),sQuery(id+"F0.wireOp",EDGE,"E16"),sQuery(id+"F0.wireOp",EDGE,"E17"),sQuery(id+"F0.wireOp",EDGE,"E18"),sQuery(id+"F0.wireOp",EDGE,"E19"),sQuery(id+"F0.wireOp",EDGE,"E20"),sQuery(id+"F0.wireOp",EDGE,"E21"),sQuery(id+"F0.wireOp",EDGE,"E22"),sQuery(id+"F0.wireOp",EDGE,"E23"),sQuery(id+"F0.wireOp",EDGE,"E24"),sQuery(id+"F0.wireOp",EDGE,"E25"),sQuery(id+"F0.wireOp",EDGE,"E26"),sQuery(id+"F0.wireOp",EDGE,"E27"),sQuery(id+"F0.wireOp",EDGE,"E28"),sQuery(id+"F0.wireOp",EDGE,"E29"),sQuery(id+"F0.wireOp",EDGE,"E30"),sQuery(id+"F0.wireOp",EDGE,"E31"),sQuery(id+"F0.wireOp",EDGE,"E32"),sQuery(id+"F0.wireOp",EDGE,"E33"),sQuery(id+"F0.wireOp",EDGE,"E34"),sQuery(id+"F0.wireOp",EDGE,"E35"),sQuery(id+"F0.wireOp",EDGE,"E36"),sQuery(id+"F0.wireOp",EDGE,"E37"),sQuery(id+"F0.wireOp",EDGE,"E38"),sQuery(id+"F0.wireOp",EDGE,"E39"),sQuery(id+"F0.wireOp",EDGE,"E40"),sQuery(id+"F0.wireOp",EDGE,"E41"),sQuery(id+"F0.wireOp",EDGE,"E42"),sQuery(id+"F0.wireOp",EDGE,"E43"),sQuery(id+"F0.wireOp",EDGE,"E44"),sQuery(id+"F0.wireOp",EDGE,"E45"),sQuery(id+"F0.wireOp",EDGE,"E46"),sQuery(id+"F0.wireOp",EDGE,"E47"),sQuery(id+"F0.wireOp",EDGE,"E48"),sQuery(id+"F0.wireOp",EDGE,"E49"),sQuery(id+"F0.wireOp",EDGE,"E50"),sQuery(id+"F0.wireOp",EDGE,"E51"),sQuery(id+"F0.wireOp",EDGE,"E52"),sQuery(id+"F0.wireOp",EDGE,"E53"),sQuery(id+"F0.wireOp",EDGE,"E54"),sQuery(id+"F0.wireOp",EDGE,"E55"),sQuery(id+"F0.wireOp",EDGE,"E56"),sQuery(id+"F0.wireOp",EDGE,"E57"),sQuery(id+"F0.wireOp",EDGE,"E58"),sQuery(id+"F0.wireOp",EDGE,"E59"),sQuery(id+"F0.wireOp",EDGE,"E60"),sQuery(id+"F0.wireOp",EDGE,"E61"),sQuery(id+"F0.wireOp",EDGE,"E62"),sQuery(id+"F0.wireOp",EDGE,"E63"),sQuery(id+"F0.wireOp",EDGE,"E64"),sQuery(id+"F0.wireOp",EDGE,"E65"),sQuery(id+"F0.wireOp",EDGE,"E66"),sQuery(id+"F0.wireOp",EDGE,"E67"),sQuery(id+"F0.wireOp",EDGE,"E68"),sQuery(id+"F0.wireOp",EDGE,"E69"),sQuery(id+"F0.wireOp",EDGE,"E70"),sQuery(id+"F0.wireOp",EDGE,"E71"),sQuery(id+"F0.wireOp",EDGE,"E72"),sQuery(id+"F0.wireOp",EDGE,"E73"),sQuery(id+"F0.wireOp",EDGE,"E74"),sQuery(id+"F0.wireOp",EDGE,"E75"),sQuery(id+"F0.wireOp",EDGE,"E76"),sQuery(id+"F0.wireOp",EDGE,"E283")])],"isStart":false});
            var sketch = newSketch(context, id + "F11", { "sketchPlane" : qUnion([Q0])});
            skLineSegment(sketch, "E361", {"start": v(-430.22, -1027.04) * mm, "end": v(369.29, -1027.04) * mm});
            skLineSegment(sketch, "E362.0.0", {"start": v(369.29, -658.1) * mm, "end": v(369.29, -596.71) * mm});
            skLineSegment(sketch, "E362.0.1", {"start": v(369.29, -596.71) * mm, "end": v(393.28, -596.71) * mm});
            skLineSegment(sketch, "E362.0.2", {"start": v(393.28, -596.71) * mm, "end": v(393.28, -535.1) * mm});
            skLineSegment(sketch, "E362.0.3", {"start": v(393.28, -535.1) * mm, "end": v(307.8, -535.1) * mm});
            skLineSegment(sketch, "E362.0.4", {"start": v(307.8, -535.1) * mm, "end": v(307.8, -511.12) * mm});
            skLineSegment(sketch, "E362.0.5", {"start": v(307.8, -511.12) * mm, "end": v(246.19, -511.12) * mm});
            skLineSegment(sketch, "E362.0.6", {"start": v(246.19, -511.12) * mm, "end": v(246.19, -535.1) * mm});
            skLineSegment(sketch, "E362.0.7", {"start": v(246.19, -535.1) * mm, "end": v(184.82, -535.1) * mm});
            skLineSegment(sketch, "E362.0.8", {"start": v(184.82, -535.1) * mm, "end": v(184.82, -511.12) * mm});
            skLineSegment(sketch, "E362.0.9", {"start": v(184.82, -511.12) * mm, "end": v(123.2, -511.12) * mm});
            skLineSegment(sketch, "E362.0.10", {"start": v(123.2, -511.12) * mm, "end": v(123.2, -535.1) * mm});
            skLineSegment(sketch, "E362.0.11", {"start": v(123.2, -535.1) * mm, "end": v(61.84, -535.1) * mm});
            skLineSegment(sketch, "E362.0.12", {"start": v(61.84, -535.1) * mm, "end": v(61.84, -511.12) * mm});
            skLineSegment(sketch, "E362.0.13", {"start": v(61.84, -511.12) * mm, "end": v(0.22, -511.12) * mm});
            skLineSegment(sketch, "E362.0.14", {"start": v(0.22, -511.12) * mm, "end": v(0.22, -535.1) * mm});
            skLineSegment(sketch, "E362.0.15", {"start": v(0.22, -535.1) * mm, "end": v(-61.15, -535.1) * mm});
            skLineSegment(sketch, "E362.0.16", {"start": v(-61.15, -535.1) * mm, "end": v(-61.15, -511.12) * mm});
            skLineSegment(sketch, "E362.0.17", {"start": v(-61.15, -511.12) * mm, "end": v(-122.76, -511.12) * mm});
            skLineSegment(sketch, "E362.0.18", {"start": v(-122.76, -511.12) * mm, "end": v(-122.76, -535.1) * mm});
            skLineSegment(sketch, "E362.0.19", {"start": v(-122.76, -535.1) * mm, "end": v(-184.13, -535.1) * mm});
            skLineSegment(sketch, "E362.0.20", {"start": v(-184.13, -535.1) * mm, "end": v(-184.13, -511.12) * mm});
            skLineSegment(sketch, "E362.0.21", {"start": v(-184.13, -511.12) * mm, "end": v(-245.74, -511.12) * mm});
            skLineSegment(sketch, "E362.0.22", {"start": v(-245.74, -511.12) * mm, "end": v(-245.74, -535.1) * mm});
            skLineSegment(sketch, "E362.0.23", {"start": v(-245.74, -535.1) * mm, "end": v(-307.11, -535.1) * mm});
            skLineSegment(sketch, "E362.0.24", {"start": v(-307.11, -535.1) * mm, "end": v(-307.11, -511.12) * mm});
            skLineSegment(sketch, "E362.0.25", {"start": v(-307.11, -511.12) * mm, "end": v(-368.73, -511.12) * mm});
            skLineSegment(sketch, "E362.0.26", {"start": v(-368.73, -511.12) * mm, "end": v(-368.73, -535.1) * mm});
            skLineSegment(sketch, "E362.0.27", {"start": v(-368.73, -535.1) * mm, "end": v(-454.2, -535.1) * mm});
            skLineSegment(sketch, "E362.0.28", {"start": v(-454.2, -535.1) * mm, "end": v(-454.2, -596.71) * mm});
            skLineSegment(sketch, "E362.0.29", {"start": v(-454.2, -596.71) * mm, "end": v(-430.22, -596.71) * mm});
            skLineSegment(sketch, "E362.0.30", {"start": v(-430.22, -596.71) * mm, "end": v(-430.22, -658.1) * mm});
            skLineSegment(sketch, "E362.0.31", {"start": v(-430.22, -658.1) * mm, "end": v(-454.2, -658.1) * mm});
            skLineSegment(sketch, "E362.0.32", {"start": v(-454.2, -658.1) * mm, "end": v(-454.2, -719.7) * mm});
            skLineSegment(sketch, "E362.0.33", {"start": v(-454.2, -719.7) * mm, "end": v(-430.22, -719.7) * mm});
            skLineSegment(sketch, "E362.0.34", {"start": v(-430.22, -719.7) * mm, "end": v(-430.22, -781.07) * mm});
            skLineSegment(sketch, "E362.0.35", {"start": v(-430.22, -781.07) * mm, "end": v(-454.2, -781.07) * mm});
            skLineSegment(sketch, "E362.0.36", {"start": v(-454.2, -781.07) * mm, "end": v(-454.2, -842.69) * mm});
            skLineSegment(sketch, "E362.0.37", {"start": v(-454.2, -842.69) * mm, "end": v(-430.22, -842.69) * mm});
            skLineSegment(sketch, "E362.0.38", {"start": v(-430.22, -842.69) * mm, "end": v(-430.22, -904.06) * mm});
            skLineSegment(sketch, "E362.0.39", {"start": v(-430.22, -904.06) * mm, "end": v(-454.2, -904.06) * mm});
            skLineSegment(sketch, "E362.0.40", {"start": v(-454.2, -904.06) * mm, "end": v(-454.2, -965.67) * mm});
            skLineSegment(sketch, "E362.0.41", {"start": v(-454.2, -965.67) * mm, "end": v(-430.22, -965.67) * mm});
            skLineSegment(sketch, "E362.0.42", {"start": v(-430.22, -965.67) * mm, "end": v(-430.22, -1027.04) * mm});
            skLineSegment(sketch, "E362.0.43", {"start": v(-430.22, -1027.04) * mm, "end": v(-454.2, -1027.04) * mm});
            skLineSegment(sketch, "E362.0.44", {"start": v(-454.2, -1027.04) * mm, "end": v(-454.2, -1088.65) * mm});
            skLineSegment(sketch, "E362.0.45", {"start": v(-454.2, -1088.65) * mm, "end": v(-430.22, -1088.65) * mm});
            skLineSegment(sketch, "E362.0.46", {"start": v(-430.22, -1088.65) * mm, "end": v(-430.22, -1150.02) * mm});
            skLineSegment(sketch, "E362.0.47", {"start": v(-430.22, -1150.02) * mm, "end": v(-454.2, -1150.02) * mm});
            skLineSegment(sketch, "E362.0.48", {"start": v(-454.2, -1150.02) * mm, "end": v(-454.2, -1211.63) * mm});
            skLineSegment(sketch, "E362.0.49", {"start": v(-454.2, -1211.63) * mm, "end": v(-430.22, -1211.63) * mm});
            skLineSegment(sketch, "E362.0.50", {"start": v(-430.22, -1211.63) * mm, "end": v(-430.22, -1273) * mm});
            skLineSegment(sketch, "E362.0.51", {"start": v(-430.22, -1273) * mm, "end": v(-454.2, -1273) * mm});
            skLineSegment(sketch, "E362.0.52", {"start": v(-454.2, -1273) * mm, "end": v(-454.2, -1334.62) * mm});
            skLineSegment(sketch, "E362.0.53", {"start": v(-454.2, -1334.62) * mm, "end": v(393.28, -1334.62) * mm});
            skLineSegment(sketch, "E362.0.54", {"start": v(393.28, -1334.62) * mm, "end": v(393.28, -1273) * mm});
            skLineSegment(sketch, "E362.0.55", {"start": v(393.28, -1273) * mm, "end": v(369.29, -1273) * mm});
            skLineSegment(sketch, "E362.0.56", {"start": v(369.29, -1273) * mm, "end": v(369.29, -1211.63) * mm});
            skLineSegment(sketch, "E362.0.57", {"start": v(369.29, -1211.63) * mm, "end": v(393.28, -1211.63) * mm});
            skLineSegment(sketch, "E362.0.58", {"start": v(393.28, -1211.63) * mm, "end": v(393.28, -1150.02) * mm});
            skLineSegment(sketch, "E362.0.59", {"start": v(393.28, -1150.02) * mm, "end": v(369.29, -1150.02) * mm});
            skLineSegment(sketch, "E362.0.60", {"start": v(369.29, -1150.02) * mm, "end": v(369.29, -1088.65) * mm});
            skLineSegment(sketch, "E362.0.61", {"start": v(369.29, -1088.65) * mm, "end": v(393.28, -1088.65) * mm});
            skLineSegment(sketch, "E362.0.62", {"start": v(393.28, -1088.65) * mm, "end": v(393.28, -1027.04) * mm});
            skLineSegment(sketch, "E362.0.63", {"start": v(393.28, -1027.04) * mm, "end": v(369.29, -1027.04) * mm});
            skLineSegment(sketch, "E362.0.64", {"start": v(369.29, -1027.04) * mm, "end": v(369.29, -965.67) * mm});
            skLineSegment(sketch, "E362.0.65", {"start": v(369.29, -965.67) * mm, "end": v(393.28, -965.67) * mm});
            skLineSegment(sketch, "E362.0.66", {"start": v(393.28, -965.67) * mm, "end": v(393.28, -904.06) * mm});
            skLineSegment(sketch, "E362.0.67", {"start": v(393.28, -904.06) * mm, "end": v(369.29, -904.06) * mm});
            skLineSegment(sketch, "E362.0.68", {"start": v(369.29, -904.06) * mm, "end": v(369.29, -842.69) * mm});
            skLineSegment(sketch, "E362.0.69", {"start": v(369.29, -842.69) * mm, "end": v(393.28, -842.69) * mm});
            skLineSegment(sketch, "E362.0.70", {"start": v(393.28, -842.69) * mm, "end": v(393.28, -781.07) * mm});
            skLineSegment(sketch, "E362.0.71", {"start": v(393.28, -781.07) * mm, "end": v(369.29, -781.07) * mm});
            skLineSegment(sketch, "E362.0.72", {"start": v(369.29, -781.07) * mm, "end": v(369.29, -719.7) * mm});
            skLineSegment(sketch, "E362.0.73", {"start": v(369.29, -719.7) * mm, "end": v(393.28, -719.7) * mm});
            skLineSegment(sketch, "E362.0.74", {"start": v(393.28, -719.7) * mm, "end": v(393.28, -658.1) * mm});
            skLineSegment(sketch, "E362.0.75", {"start": v(393.28, -658.1) * mm, "end": v(369.29, -658.1) * mm});
            skSolve(sketch);
        }
        {
            var Q0;
            Q0=makeQuery(id+"F11.imprint","IMPRINT",FACE,{"disambiguationData":[TD([[makeQuery(id+"F11.imprint","IMPRINT",EDGE,{"derivedFrom":sQuery(id+"F11.wireOp",EDGE,"E361")}),-1.0]])]});
            extrude(context, id + "F12", {"entities" : qUnion([Q0]), "operationType" : NewBodyOperationType.REMOVE, "oppositeDirection" : true, "depth" : 25.4 * mm});
        }
        {
            var Q0;
            Q0=makeQuery(id+"F4.opExtrude","CAP_FACE",FACE,{"disambiguationData":[OSD([sQuery(id+"F0.wireOp",EDGE,"E0"),sQuery(id+"F0.wireOp",EDGE,"E1"),sQuery(id+"F0.wireOp",EDGE,"E2"),sQuery(id+"F0.wireOp",EDGE,"E3"),sQuery(id+"F0.wireOp",EDGE,"E4"),sQuery(id+"F0.wireOp",EDGE,"E5"),sQuery(id+"F0.wireOp",EDGE,"E6"),sQuery(id+"F0.wireOp",EDGE,"E7"),sQuery(id+"F0.wireOp",EDGE,"E8"),sQuery(id+"F0.wireOp",EDGE,"E9"),sQuery(id+"F0.wireOp",EDGE,"E10"),sQuery(id+"F0.wireOp",EDGE,"E11"),sQuery(id+"F0.wireOp",EDGE,"E12"),sQuery(id+"F0.wireOp",EDGE,"E13"),sQuery(id+"F0.wireOp",EDGE,"E14"),sQuery(id+"F0.wireOp",EDGE,"E15"),sQuery(id+"F0.wireOp",EDGE,"E16"),sQuery(id+"F0.wireOp",EDGE,"E17"),sQuery(id+"F0.wireOp",EDGE,"E18"),sQuery(id+"F0.wireOp",EDGE,"E19"),sQuery(id+"F0.wireOp",EDGE,"E20"),sQuery(id+"F0.wireOp",EDGE,"E21"),sQuery(id+"F0.wireOp",EDGE,"E22"),sQuery(id+"F0.wireOp",EDGE,"E23"),sQuery(id+"F0.wireOp",EDGE,"E24"),sQuery(id+"F0.wireOp",EDGE,"E25"),sQuery(id+"F0.wireOp",EDGE,"E26"),sQuery(id+"F0.wireOp",EDGE,"E27"),sQuery(id+"F0.wireOp",EDGE,"E28"),sQuery(id+"F0.wireOp",EDGE,"E29"),sQuery(id+"F0.wireOp",EDGE,"E30"),sQuery(id+"F0.wireOp",EDGE,"E31"),sQuery(id+"F0.wireOp",EDGE,"E32"),sQuery(id+"F0.wireOp",EDGE,"E33"),sQuery(id+"F0.wireOp",EDGE,"E34"),sQuery(id+"F0.wireOp",EDGE,"E35"),sQuery(id+"F0.wireOp",EDGE,"E36"),sQuery(id+"F0.wireOp",EDGE,"E37"),sQuery(id+"F0.wireOp",EDGE,"E38"),sQuery(id+"F0.wireOp",EDGE,"E39"),sQuery(id+"F0.wireOp",EDGE,"E40"),sQuery(id+"F0.wireOp",EDGE,"E41"),sQuery(id+"F0.wireOp",EDGE,"E42"),sQuery(id+"F0.wireOp",EDGE,"E43"),sQuery(id+"F0.wireOp",EDGE,"E44"),sQuery(id+"F0.wireOp",EDGE,"E45"),sQuery(id+"F0.wireOp",EDGE,"E46"),sQuery(id+"F0.wireOp",EDGE,"E47"),sQuery(id+"F0.wireOp",EDGE,"E48"),sQuery(id+"F0.wireOp",EDGE,"E49"),sQuery(id+"F0.wireOp",EDGE,"E50"),sQuery(id+"F0.wireOp",EDGE,"E51"),sQuery(id+"F0.wireOp",EDGE,"E52"),sQuery(id+"F0.wireOp",EDGE,"E53"),sQuery(id+"F0.wireOp",EDGE,"E54"),sQuery(id+"F0.wireOp",EDGE,"E55"),sQuery(id+"F0.wireOp",EDGE,"E56"),sQuery(id+"F0.wireOp",EDGE,"E57"),sQuery(id+"F0.wireOp",EDGE,"E58"),sQuery(id+"F0.wireOp",EDGE,"E59"),sQuery(id+"F0.wireOp",EDGE,"E60"),sQuery(id+"F0.wireOp",EDGE,"E61"),sQuery(id+"F0.wireOp",EDGE,"E62"),sQuery(id+"F0.wireOp",EDGE,"E63"),sQuery(id+"F0.wireOp",EDGE,"E64"),sQuery(id+"F0.wireOp",EDGE,"E65"),sQuery(id+"F0.wireOp",EDGE,"E66"),sQuery(id+"F0.wireOp",EDGE,"E67"),sQuery(id+"F0.wireOp",EDGE,"E68"),sQuery(id+"F0.wireOp",EDGE,"E69"),sQuery(id+"F0.wireOp",EDGE,"E70"),sQuery(id+"F0.wireOp",EDGE,"E71"),sQuery(id+"F0.wireOp",EDGE,"E72"),sQuery(id+"F0.wireOp",EDGE,"E73"),sQuery(id+"F0.wireOp",EDGE,"E74"),sQuery(id+"F0.wireOp",EDGE,"E75"),sQuery(id+"F0.wireOp",EDGE,"E76"),sQuery(id+"F0.wireOp",EDGE,"E283")])],"isStart":false});
            var sketch = newSketch(context, id + "F13", { "sketchPlane" : qUnion([Q0])});
            skLineSegment(sketch, "E363", {"start": v(-430.22, -842.69) * mm, "end": v(369.29, -842.69) * mm});
            skLineSegment(sketch, "E364.0.0", {"start": v(-430.22, -965.67) * mm, "end": v(-430.22, -1027.04) * mm});
            skLineSegment(sketch, "E364.0.1", {"start": v(-430.22, -1027.04) * mm, "end": v(369.29, -1027.04) * mm});
            skLineSegment(sketch, "E364.0.2", {"start": v(369.29, -1027.04) * mm, "end": v(369.29, -965.67) * mm});
            skLineSegment(sketch, "E364.0.3", {"start": v(369.29, -965.67) * mm, "end": v(393.28, -965.67) * mm});
            skLineSegment(sketch, "E364.0.4", {"start": v(393.28, -965.67) * mm, "end": v(393.28, -904.06) * mm});
            skLineSegment(sketch, "E364.0.5", {"start": v(393.28, -904.06) * mm, "end": v(369.29, -904.06) * mm});
            skLineSegment(sketch, "E364.0.6", {"start": v(369.29, -904.06) * mm, "end": v(369.29, -842.69) * mm});
            skLineSegment(sketch, "E364.0.7", {"start": v(369.29, -842.69) * mm, "end": v(393.28, -842.69) * mm});
            skLineSegment(sketch, "E364.0.8", {"start": v(393.28, -842.69) * mm, "end": v(393.28, -781.07) * mm});
            skLineSegment(sketch, "E364.0.9", {"start": v(393.28, -781.07) * mm, "end": v(369.29, -781.07) * mm});
            skLineSegment(sketch, "E364.0.10", {"start": v(369.29, -781.07) * mm, "end": v(369.29, -719.7) * mm});
            skLineSegment(sketch, "E364.0.11", {"start": v(369.29, -719.7) * mm, "end": v(393.28, -719.7) * mm});
            skLineSegment(sketch, "E364.0.12", {"start": v(393.28, -719.7) * mm, "end": v(393.28, -658.1) * mm});
            skLineSegment(sketch, "E364.0.13", {"start": v(393.28, -658.1) * mm, "end": v(369.29, -658.1) * mm});
            skLineSegment(sketch, "E364.0.14", {"start": v(369.29, -658.1) * mm, "end": v(369.29, -596.71) * mm});
            skLineSegment(sketch, "E364.0.15", {"start": v(369.29, -596.71) * mm, "end": v(393.28, -596.71) * mm});
            skLineSegment(sketch, "E364.0.16", {"start": v(393.28, -596.71) * mm, "end": v(393.28, -535.1) * mm});
            skLineSegment(sketch, "E364.0.17", {"start": v(393.28, -535.1) * mm, "end": v(307.8, -535.1) * mm});
            skLineSegment(sketch, "E364.0.18", {"start": v(307.8, -535.1) * mm, "end": v(307.8, -511.12) * mm});
            skLineSegment(sketch, "E364.0.19", {"start": v(307.8, -511.12) * mm, "end": v(246.19, -511.12) * mm});
            skLineSegment(sketch, "E364.0.20", {"start": v(246.19, -511.12) * mm, "end": v(246.19, -535.1) * mm});
            skLineSegment(sketch, "E364.0.21", {"start": v(246.19, -535.1) * mm, "end": v(184.82, -535.1) * mm});
            skLineSegment(sketch, "E364.0.22", {"start": v(184.82, -535.1) * mm, "end": v(184.82, -511.12) * mm});
            skLineSegment(sketch, "E364.0.23", {"start": v(184.82, -511.12) * mm, "end": v(123.2, -511.12) * mm});
            skLineSegment(sketch, "E364.0.24", {"start": v(123.2, -511.12) * mm, "end": v(123.2, -535.1) * mm});
            skLineSegment(sketch, "E364.0.25", {"start": v(123.2, -535.1) * mm, "end": v(61.84, -535.1) * mm});
            skLineSegment(sketch, "E364.0.26", {"start": v(61.84, -535.1) * mm, "end": v(61.84, -511.12) * mm});
            skLineSegment(sketch, "E364.0.27", {"start": v(61.84, -511.12) * mm, "end": v(0.22, -511.12) * mm});
            skLineSegment(sketch, "E364.0.28", {"start": v(0.22, -511.12) * mm, "end": v(0.22, -535.1) * mm});
            skLineSegment(sketch, "E364.0.29", {"start": v(0.22, -535.1) * mm, "end": v(-61.15, -535.1) * mm});
            skLineSegment(sketch, "E364.0.30", {"start": v(-61.15, -535.1) * mm, "end": v(-61.15, -511.12) * mm});
            skLineSegment(sketch, "E364.0.31", {"start": v(-61.15, -511.12) * mm, "end": v(-122.76, -511.12) * mm});
            skLineSegment(sketch, "E364.0.32", {"start": v(-122.76, -511.12) * mm, "end": v(-122.76, -535.1) * mm});
            skLineSegment(sketch, "E364.0.33", {"start": v(-122.76, -535.1) * mm, "end": v(-184.13, -535.1) * mm});
            skLineSegment(sketch, "E364.0.34", {"start": v(-184.13, -535.1) * mm, "end": v(-184.13, -511.12) * mm});
            skLineSegment(sketch, "E364.0.35", {"start": v(-184.13, -511.12) * mm, "end": v(-245.74, -511.12) * mm});
            skLineSegment(sketch, "E364.0.36", {"start": v(-245.74, -511.12) * mm, "end": v(-245.74, -535.1) * mm});
            skLineSegment(sketch, "E364.0.37", {"start": v(-245.74, -535.1) * mm, "end": v(-307.11, -535.1) * mm});
            skLineSegment(sketch, "E364.0.38", {"start": v(-307.11, -535.1) * mm, "end": v(-307.11, -511.12) * mm});
            skLineSegment(sketch, "E364.0.39", {"start": v(-307.11, -511.12) * mm, "end": v(-368.73, -511.12) * mm});
            skLineSegment(sketch, "E364.0.40", {"start": v(-368.73, -511.12) * mm, "end": v(-368.73, -535.1) * mm});
            skLineSegment(sketch, "E364.0.41", {"start": v(-368.73, -535.1) * mm, "end": v(-454.2, -535.1) * mm});
            skLineSegment(sketch, "E364.0.42", {"start": v(-454.2, -535.1) * mm, "end": v(-454.2, -596.71) * mm});
            skLineSegment(sketch, "E364.0.43", {"start": v(-454.2, -596.71) * mm, "end": v(-430.22, -596.71) * mm});
            skLineSegment(sketch, "E364.0.44", {"start": v(-430.22, -596.71) * mm, "end": v(-430.22, -658.1) * mm});
            skLineSegment(sketch, "E364.0.45", {"start": v(-430.22, -658.1) * mm, "end": v(-454.2, -658.1) * mm});
            skLineSegment(sketch, "E364.0.46", {"start": v(-454.2, -658.1) * mm, "end": v(-454.2, -719.7) * mm});
            skLineSegment(sketch, "E364.0.47", {"start": v(-454.2, -719.7) * mm, "end": v(-430.22, -719.7) * mm});
            skLineSegment(sketch, "E364.0.48", {"start": v(-430.22, -719.7) * mm, "end": v(-430.22, -781.07) * mm});
            skLineSegment(sketch, "E364.0.49", {"start": v(-430.22, -781.07) * mm, "end": v(-454.2, -781.07) * mm});
            skLineSegment(sketch, "E364.0.50", {"start": v(-454.2, -781.07) * mm, "end": v(-454.2, -842.69) * mm});
            skLineSegment(sketch, "E364.0.51", {"start": v(-454.2, -842.69) * mm, "end": v(-430.22, -842.69) * mm});
            skLineSegment(sketch, "E364.0.52", {"start": v(-430.22, -842.69) * mm, "end": v(-430.22, -904.06) * mm});
            skLineSegment(sketch, "E364.0.53", {"start": v(-430.22, -904.06) * mm, "end": v(-454.2, -904.06) * mm});
            skLineSegment(sketch, "E364.0.54", {"start": v(-454.2, -904.06) * mm, "end": v(-454.2, -965.67) * mm});
            skLineSegment(sketch, "E364.0.55", {"start": v(-454.2, -965.67) * mm, "end": v(-430.22, -965.67) * mm});
            skSolve(sketch);
        }
        {
            var Q0;
            Q0=makeQuery(id+"F13.imprint","IMPRINT",FACE,{"disambiguationData":[TD([[makeQuery(id+"F13.imprint","IMPRINT",EDGE,{"derivedFrom":sQuery(id+"F13.wireOp",EDGE,"E363")}),-1.0]])]});
            extrude(context, id + "F14", {"entities" : qUnion([Q0]), "operationType" : NewBodyOperationType.REMOVE, "oppositeDirection" : true, "depth" : 25.4 * mm});
        }
        {
            var Q0;
            Q0=makeQuery(id+"F1.opExtrude","CAP_FACE",FACE,{"disambiguationData":[OSD([sQuery(id+"F0.wireOp",EDGE,"E167"),sQuery(id+"F0.wireOp",EDGE,"E168"),sQuery(id+"F0.wireOp",EDGE,"E169"),sQuery(id+"F0.wireOp",EDGE,"E170"),sQuery(id+"F0.wireOp",EDGE,"E171"),sQuery(id+"F0.wireOp",EDGE,"E172"),sQuery(id+"F0.wireOp",EDGE,"E173"),sQuery(id+"F0.wireOp",EDGE,"E174"),sQuery(id+"F0.wireOp",EDGE,"E175"),sQuery(id+"F0.wireOp",EDGE,"E176"),sQuery(id+"F0.wireOp",EDGE,"E177"),sQuery(id+"F0.wireOp",EDGE,"E178"),sQuery(id+"F0.wireOp",EDGE,"E179"),sQuery(id+"F0.wireOp",EDGE,"E180"),sQuery(id+"F0.wireOp",EDGE,"E181"),sQuery(id+"F0.wireOp",EDGE,"E182"),sQuery(id+"F0.wireOp",EDGE,"E183"),sQuery(id+"F0.wireOp",EDGE,"E184"),sQuery(id+"F0.wireOp",EDGE,"E185"),sQuery(id+"F0.wireOp",EDGE,"E186"),sQuery(id+"F0.wireOp",EDGE,"E187"),sQuery(id+"F0.wireOp",EDGE,"E188"),sQuery(id+"F0.wireOp",EDGE,"E189"),sQuery(id+"F0.wireOp",EDGE,"E190"),sQuery(id+"F0.wireOp",EDGE,"E191"),sQuery(id+"F0.wireOp",EDGE,"E192"),sQuery(id+"F0.wireOp",EDGE,"E193"),sQuery(id+"F0.wireOp",EDGE,"E194"),sQuery(id+"F0.wireOp",EDGE,"E195"),sQuery(id+"F0.wireOp",EDGE,"E196"),sQuery(id+"F0.wireOp",EDGE,"E197"),sQuery(id+"F0.wireOp",EDGE,"E198"),sQuery(id+"F0.wireOp",EDGE,"E199"),sQuery(id+"F0.wireOp",EDGE,"E200"),sQuery(id+"F0.wireOp",EDGE,"E201"),sQuery(id+"F0.wireOp",EDGE,"E202"),sQuery(id+"F0.wireOp",EDGE,"E203"),sQuery(id+"F0.wireOp",EDGE,"E204"),sQuery(id+"F0.wireOp",EDGE,"E205"),sQuery(id+"F0.wireOp",EDGE,"E206"),sQuery(id+"F0.wireOp",EDGE,"E207"),sQuery(id+"F0.wireOp",EDGE,"E208"),sQuery(id+"F0.wireOp",EDGE,"E209"),sQuery(id+"F0.wireOp",EDGE,"E210"),sQuery(id+"F0.wireOp",EDGE,"E211"),sQuery(id+"F0.wireOp",EDGE,"E212"),sQuery(id+"F0.wireOp",EDGE,"E213"),sQuery(id+"F0.wireOp",EDGE,"E214"),sQuery(id+"F0.wireOp",EDGE,"E215"),sQuery(id+"F0.wireOp",EDGE,"E216"),sQuery(id+"F0.wireOp",EDGE,"E217"),sQuery(id+"F0.wireOp",EDGE,"E218"),sQuery(id+"F0.wireOp",EDGE,"E219"),sQuery(id+"F0.wireOp",EDGE,"E220"),sQuery(id+"F0.wireOp",EDGE,"E221"),sQuery(id+"F0.wireOp",EDGE,"E278"),sQuery(id+"F0.wireOp",EDGE,"E279")])],"isStart":false});
            var sketch = newSketch(context, id + "F15", { "sketchPlane" : qUnion([Q0])});
            skLineSegment(sketch, "E365", {"start": v(-483.06, 237.19) * mm, "end": v(-1282.57, 237.19) * mm});
            skLineSegment(sketch, "E366.0.0", {"start": v(-798.52, 114.75) * mm, "end": v(-1282.57, 114.75) * mm});
            skLineSegment(sketch, "E366.0.1", {"start": v(-1282.57, 114.75) * mm, "end": v(-1282.57, 45.92) * mm});
            skLineSegment(sketch, "E366.0.2", {"start": v(-1282.57, 45.92) * mm, "end": v(-870.4, 45.92) * mm});
            skLineSegment(sketch, "E366.0.3", {"start": v(-870.4, 45.92) * mm, "end": v(-870.4, 32.2) * mm});
            skLineSegment(sketch, "E366.0.4", {"start": v(-870.4, 32.2) * mm, "end": v(-1282.57, 32.2) * mm});
            skLineSegment(sketch, "E366.0.5", {"start": v(-1282.57, 32.2) * mm, "end": v(-1282.57, -36.63) * mm});
            skLineSegment(sketch, "E366.0.6", {"start": v(-1282.57, -36.63) * mm, "end": v(-945.59, -36.63) * mm});
            skLineSegment(sketch, "E366.0.7", {"start": v(-945.59, -36.63) * mm, "end": v(-945.59, -50.35) * mm});
            skLineSegment(sketch, "E366.0.8", {"start": v(-945.59, -50.35) * mm, "end": v(-1282.57, -50.35) * mm});
            skLineSegment(sketch, "E366.0.9", {"start": v(-1282.57, -50.35) * mm, "end": v(-1282.57, -119.18) * mm});
            skLineSegment(sketch, "E366.0.10", {"start": v(-1282.57, -119.18) * mm, "end": v(-1041.35, -119.18) * mm});
            skLineSegment(sketch, "E366.0.11", {"start": v(-1041.35, -119.18) * mm, "end": v(-1041.35, -132.9) * mm});
            skLineSegment(sketch, "E366.0.12", {"start": v(-1041.35, -132.9) * mm, "end": v(-1282.57, -132.9) * mm});
            skLineSegment(sketch, "E366.0.13", {"start": v(-1282.57, -132.9) * mm, "end": v(-1282.57, -201.73) * mm});
            skLineSegment(sketch, "E366.0.14", {"start": v(-1282.57, -201.73) * mm, "end": v(-1107.39, -201.73) * mm});
            skLineSegment(sketch, "E366.0.15", {"start": v(-1107.39, -201.73) * mm, "end": v(-1107.39, -215.45) * mm});
            skLineSegment(sketch, "E366.0.16", {"start": v(-1107.39, -215.45) * mm, "end": v(-1282.57, -215.45) * mm});
            skLineSegment(sketch, "E366.0.17", {"start": v(-1282.57, -215.45) * mm, "end": v(-1282.57, -284.28) * mm});
            skLineSegment(sketch, "E366.0.18", {"start": v(-1282.57, -284.28) * mm, "end": v(-1084.53, -284.28) * mm});
            skLineSegment(sketch, "E366.0.19", {"start": v(-1084.53, -284.28) * mm, "end": v(-1084.53, -298) * mm});
            skLineSegment(sketch, "E366.0.20", {"start": v(-1084.53, -298) * mm, "end": v(-1282.57, -298) * mm});
            skLineSegment(sketch, "E366.0.21", {"start": v(-1282.57, -298) * mm, "end": v(-1282.57, -482.26) * mm});
            skLineSegment(sketch, "E366.0.22", {"start": v(-1282.57, -482.26) * mm, "end": v(-1221.08, -482.26) * mm});
            skLineSegment(sketch, "E366.0.23", {"start": v(-1221.08, -482.26) * mm, "end": v(-1221.08, -506.25) * mm});
            skLineSegment(sketch, "E366.0.24", {"start": v(-1221.08, -506.25) * mm, "end": v(-1159.47, -506.25) * mm});
            skLineSegment(sketch, "E366.0.25", {"start": v(-1159.47, -506.25) * mm, "end": v(-1159.47, -482.26) * mm});
            skLineSegment(sketch, "E366.0.26", {"start": v(-1159.47, -482.26) * mm, "end": v(-1098.1, -482.26) * mm});
            skLineSegment(sketch, "E366.0.27", {"start": v(-1098.1, -482.26) * mm, "end": v(-1098.1, -506.25) * mm});
            skLineSegment(sketch, "E366.0.28", {"start": v(-1098.1, -506.25) * mm, "end": v(-1036.48, -506.25) * mm});
            skLineSegment(sketch, "E366.0.29", {"start": v(-1036.48, -506.25) * mm, "end": v(-1036.48, -482.26) * mm});
            skLineSegment(sketch, "E366.0.30", {"start": v(-1036.48, -482.26) * mm, "end": v(-975.11, -482.26) * mm});
            skLineSegment(sketch, "E366.0.31", {"start": v(-975.11, -482.26) * mm, "end": v(-975.11, -506.25) * mm});
            skLineSegment(sketch, "E366.0.32", {"start": v(-975.11, -506.25) * mm, "end": v(-913.5, -506.25) * mm});
            skLineSegment(sketch, "E366.0.33", {"start": v(-913.5, -506.25) * mm, "end": v(-913.5, -482.26) * mm});
            skLineSegment(sketch, "E366.0.34", {"start": v(-913.5, -482.26) * mm, "end": v(-852.13, -482.26) * mm});
            skLineSegment(sketch, "E366.0.35", {"start": v(-852.13, -482.26) * mm, "end": v(-852.13, -506.25) * mm});
            skLineSegment(sketch, "E366.0.36", {"start": v(-852.13, -506.25) * mm, "end": v(-790.52, -506.25) * mm});
            skLineSegment(sketch, "E366.0.37", {"start": v(-790.52, -506.25) * mm, "end": v(-790.52, -482.26) * mm});
            skLineSegment(sketch, "E366.0.38", {"start": v(-790.52, -482.26) * mm, "end": v(-729.15, -482.26) * mm});
            skLineSegment(sketch, "E366.0.39", {"start": v(-729.15, -482.26) * mm, "end": v(-729.15, -506.25) * mm});
            skLineSegment(sketch, "E366.0.40", {"start": v(-729.15, -506.25) * mm, "end": v(-667.53, -506.25) * mm});
            skLineSegment(sketch, "E366.0.41", {"start": v(-667.53, -506.25) * mm, "end": v(-667.53, -482.26) * mm});
            skLineSegment(sketch, "E366.0.42", {"start": v(-667.53, -482.26) * mm, "end": v(-606.17, -482.26) * mm});
            skLineSegment(sketch, "E366.0.43", {"start": v(-606.17, -482.26) * mm, "end": v(-606.17, -506.25) * mm});
            skLineSegment(sketch, "E366.0.44", {"start": v(-606.17, -506.25) * mm, "end": v(-544.55, -506.25) * mm});
            skLineSegment(sketch, "E366.0.45", {"start": v(-544.55, -506.25) * mm, "end": v(-544.55, -482.26) * mm});
            skLineSegment(sketch, "E366.0.46", {"start": v(-544.55, -482.26) * mm, "end": v(-459.08, -482.26) * mm});
            skLineSegment(sketch, "E366.0.47", {"start": v(-459.08, -482.26) * mm, "end": v(-459.08, -422.19) * mm});
            skLineSegment(sketch, "E366.0.48", {"start": v(-459.08, -422.19) * mm, "end": v(-483.06, -422.19) * mm});
            skLineSegment(sketch, "E366.0.49", {"start": v(-483.06, -422.19) * mm, "end": v(-483.06, -362.36) * mm});
            skLineSegment(sketch, "E366.0.50", {"start": v(-483.06, -362.36) * mm, "end": v(-459.08, -362.36) * mm});
            skLineSegment(sketch, "E366.0.51", {"start": v(-459.08, -362.36) * mm, "end": v(-459.08, -302.28) * mm});
            skLineSegment(sketch, "E366.0.52", {"start": v(-459.08, -302.28) * mm, "end": v(-483.06, -302.28) * mm});
            skLineSegment(sketch, "E366.0.53", {"start": v(-483.06, -302.28) * mm, "end": v(-483.06, -242.45) * mm});
            skLineSegment(sketch, "E366.0.54", {"start": v(-483.06, -242.45) * mm, "end": v(-459.08, -242.45) * mm});
            skLineSegment(sketch, "E366.0.55", {"start": v(-459.08, -242.45) * mm, "end": v(-459.08, -182.38) * mm});
            skLineSegment(sketch, "E366.0.56", {"start": v(-459.08, -182.38) * mm, "end": v(-483.06, -182.38) * mm});
            skLineSegment(sketch, "E366.0.57", {"start": v(-483.06, -182.38) * mm, "end": v(-483.06, -122.53) * mm});
            skLineSegment(sketch, "E366.0.58", {"start": v(-483.06, -122.53) * mm, "end": v(-459.08, -122.53) * mm});
            skLineSegment(sketch, "E366.0.59", {"start": v(-459.08, -122.53) * mm, "end": v(-459.08, -62.46) * mm});
            skLineSegment(sketch, "E366.0.60", {"start": v(-459.08, -62.46) * mm, "end": v(-483.06, -62.46) * mm});
            skLineSegment(sketch, "E366.0.61", {"start": v(-483.06, -62.46) * mm, "end": v(-483.06, -2.63) * mm});
            skLineSegment(sketch, "E366.0.62", {"start": v(-483.06, -2.63) * mm, "end": v(-459.08, -2.63) * mm});
            skLineSegment(sketch, "E366.0.63", {"start": v(-459.08, -2.63) * mm, "end": v(-459.08, 57.45) * mm});
            skLineSegment(sketch, "E366.0.64", {"start": v(-459.08, 57.45) * mm, "end": v(-483.06, 57.45) * mm});
            skLineSegment(sketch, "E366.0.65", {"start": v(-483.06, 57.45) * mm, "end": v(-483.06, 117.28) * mm});
            skLineSegment(sketch, "E366.0.66", {"start": v(-483.06, 117.28) * mm, "end": v(-459.08, 117.28) * mm});
            skLineSegment(sketch, "E366.0.67", {"start": v(-459.08, 117.28) * mm, "end": v(-459.08, 177.36) * mm});
            skLineSegment(sketch, "E366.0.68", {"start": v(-459.08, 177.36) * mm, "end": v(-483.06, 177.36) * mm});
            skLineSegment(sketch, "E366.0.69", {"start": v(-483.06, 177.36) * mm, "end": v(-483.06, 237.19) * mm});
            skLineSegment(sketch, "E366.0.70", {"start": v(-483.06, 237.19) * mm, "end": v(-459.08, 237.19) * mm});
            skLineSegment(sketch, "E366.0.71", {"start": v(-459.08, 237.19) * mm, "end": v(-459.08, 297.26) * mm});
            skLineSegment(sketch, "E366.0.72", {"start": v(-459.08, 297.26) * mm, "end": v(-483.06, 297.26) * mm});
            skLineSegment(sketch, "E366.0.73", {"start": v(-483.06, 297.26) * mm, "end": v(-483.06, 357.1) * mm});
            skLineSegment(sketch, "E366.0.74", {"start": v(-483.06, 357.1) * mm, "end": v(-459.08, 357.1) * mm});
            skLineSegment(sketch, "E366.0.75", {"start": v(-459.08, 357.1) * mm, "end": v(-459.08, 417.17) * mm});
            skLineSegment(sketch, "E366.0.76", {"start": v(-459.08, 417.17) * mm, "end": v(-1282.57, 417.17) * mm});
            skLineSegment(sketch, "E366.0.77", {"start": v(-1282.57, 417.17) * mm, "end": v(-1282.57, 128.47) * mm});
            skLineSegment(sketch, "E366.0.78", {"start": v(-1282.57, 128.47) * mm, "end": v(-798.52, 128.47) * mm});
            skLineSegment(sketch, "E366.0.79", {"start": v(-798.52, 128.47) * mm, "end": v(-798.52, 114.75) * mm});
            skLineSegment(sketch, "E367", {"start": v(-483.06, 177.36) * mm, "end": v(-1282.57, 177.36) * mm});
            skSolve(sketch);
        }
        {
            var Q0;
            {var subQ0=sQuery(id+"F15.wireOp",EDGE,"E365");Q0=makeQuery(id+"F15.imprint","IMPRINT",FACE,{"disambiguationData":[TD([[makeQuery(id+"F15.imprint","IMPRINT",EDGE,{"derivedFrom":subQ0}),-1.0]])]});}
            var Q1;
            {var subQ0=sQuery(id+"F15.wireOp",EDGE,"E365");Q1=makeQuery(id+"F15.imprint","IMPRINT",FACE,{"disambiguationData":[TD([[makeQuery(id+"F15.imprint","IMPRINT",EDGE,{"derivedFrom":subQ0}),1.0]])]});}
            extrude(context, id + "F16", {"entities" : qUnion([Q0, Q1]), "operationType" : NewBodyOperationType.REMOVE, "oppositeDirection" : true, "depth" : 25.4 * mm});
        }
        {
            var Q0;
            Q0=makeQuery(id+"F1.opExtrude","CAP_FACE",FACE,{"disambiguationData":[OSD([sQuery(id+"F0.wireOp",EDGE,"E222"),sQuery(id+"F0.wireOp",EDGE,"E223"),sQuery(id+"F0.wireOp",EDGE,"E224"),sQuery(id+"F0.wireOp",EDGE,"E225"),sQuery(id+"F0.wireOp",EDGE,"E226"),sQuery(id+"F0.wireOp",EDGE,"E227"),sQuery(id+"F0.wireOp",EDGE,"E228"),sQuery(id+"F0.wireOp",EDGE,"E229"),sQuery(id+"F0.wireOp",EDGE,"E230"),sQuery(id+"F0.wireOp",EDGE,"E231"),sQuery(id+"F0.wireOp",EDGE,"E232"),sQuery(id+"F0.wireOp",EDGE,"E233"),sQuery(id+"F0.wireOp",EDGE,"E234"),sQuery(id+"F0.wireOp",EDGE,"E235"),sQuery(id+"F0.wireOp",EDGE,"E236"),sQuery(id+"F0.wireOp",EDGE,"E237"),sQuery(id+"F0.wireOp",EDGE,"E238"),sQuery(id+"F0.wireOp",EDGE,"E239"),sQuery(id+"F0.wireOp",EDGE,"E240"),sQuery(id+"F0.wireOp",EDGE,"E241"),sQuery(id+"F0.wireOp",EDGE,"E242"),sQuery(id+"F0.wireOp",EDGE,"E243"),sQuery(id+"F0.wireOp",EDGE,"E244"),sQuery(id+"F0.wireOp",EDGE,"E245"),sQuery(id+"F0.wireOp",EDGE,"E246"),sQuery(id+"F0.wireOp",EDGE,"E247"),sQuery(id+"F0.wireOp",EDGE,"E248"),sQuery(id+"F0.wireOp",EDGE,"E249"),sQuery(id+"F0.wireOp",EDGE,"E250"),sQuery(id+"F0.wireOp",EDGE,"E251"),sQuery(id+"F0.wireOp",EDGE,"E252"),sQuery(id+"F0.wireOp",EDGE,"E253"),sQuery(id+"F0.wireOp",EDGE,"E254"),sQuery(id+"F0.wireOp",EDGE,"E255"),sQuery(id+"F0.wireOp",EDGE,"E256"),sQuery(id+"F0.wireOp",EDGE,"E257"),sQuery(id+"F0.wireOp",EDGE,"E258"),sQuery(id+"F0.wireOp",EDGE,"E259"),sQuery(id+"F0.wireOp",EDGE,"E260"),sQuery(id+"F0.wireOp",EDGE,"E261"),sQuery(id+"F0.wireOp",EDGE,"E262"),sQuery(id+"F0.wireOp",EDGE,"E263"),sQuery(id+"F0.wireOp",EDGE,"E264"),sQuery(id+"F0.wireOp",EDGE,"E265"),sQuery(id+"F0.wireOp",EDGE,"E266"),sQuery(id+"F0.wireOp",EDGE,"E267"),sQuery(id+"F0.wireOp",EDGE,"E268"),sQuery(id+"F0.wireOp",EDGE,"E269"),sQuery(id+"F0.wireOp",EDGE,"E270"),sQuery(id+"F0.wireOp",EDGE,"E271"),sQuery(id+"F0.wireOp",EDGE,"E272"),sQuery(id+"F0.wireOp",EDGE,"E273"),sQuery(id+"F0.wireOp",EDGE,"E274"),sQuery(id+"F0.wireOp",EDGE,"E275"),sQuery(id+"F0.wireOp",EDGE,"E276"),sQuery(id+"F0.wireOp",EDGE,"E281"),sQuery(id+"F0.wireOp",EDGE,"E282")])],"isStart":false});
            var sketch = newSketch(context, id + "F17", { "sketchPlane" : qUnion([Q0])});
            skLineSegment(sketch, "E368", {"start": v(422.13, 177.36) * mm, "end": v(1221.65, 177.36) * mm});
            skLineSegment(sketch, "E369.0.0", {"start": v(1221.65, 45.92) * mm, "end": v(1221.65, 114.75) * mm});
            skLineSegment(sketch, "E369.0.1", {"start": v(1221.65, 114.75) * mm, "end": v(737.6, 114.75) * mm});
            skLineSegment(sketch, "E369.0.2", {"start": v(737.6, 114.75) * mm, "end": v(737.6, 128.47) * mm});
            skLineSegment(sketch, "E369.0.3", {"start": v(737.6, 128.47) * mm, "end": v(1221.65, 128.47) * mm});
            skLineSegment(sketch, "E369.0.4", {"start": v(1221.65, 128.47) * mm, "end": v(1221.65, 417.17) * mm});
            skLineSegment(sketch, "E369.0.5", {"start": v(1221.65, 417.17) * mm, "end": v(398.15, 417.17) * mm});
            skLineSegment(sketch, "E369.0.6", {"start": v(398.15, 417.17) * mm, "end": v(398.15, 357.1) * mm});
            skLineSegment(sketch, "E369.0.7", {"start": v(398.15, 357.1) * mm, "end": v(422.13, 357.1) * mm});
            skLineSegment(sketch, "E369.0.8", {"start": v(422.13, 357.1) * mm, "end": v(422.13, 297.26) * mm});
            skLineSegment(sketch, "E369.0.9", {"start": v(422.13, 297.26) * mm, "end": v(398.15, 297.26) * mm});
            skLineSegment(sketch, "E369.0.10", {"start": v(398.15, 297.26) * mm, "end": v(398.15, 237.19) * mm});
            skLineSegment(sketch, "E369.0.11", {"start": v(398.15, 237.19) * mm, "end": v(422.13, 237.19) * mm});
            skLineSegment(sketch, "E369.0.12", {"start": v(422.13, 237.19) * mm, "end": v(422.13, 177.36) * mm});
            skLineSegment(sketch, "E369.0.13", {"start": v(422.13, 177.36) * mm, "end": v(398.15, 177.36) * mm});
            skLineSegment(sketch, "E369.0.14", {"start": v(398.15, 177.36) * mm, "end": v(398.15, 117.28) * mm});
            skLineSegment(sketch, "E369.0.15", {"start": v(398.15, 117.28) * mm, "end": v(422.13, 117.28) * mm});
            skLineSegment(sketch, "E369.0.16", {"start": v(422.13, 117.28) * mm, "end": v(422.13, 57.45) * mm});
            skLineSegment(sketch, "E369.0.17", {"start": v(422.13, 57.45) * mm, "end": v(398.15, 57.45) * mm});
            skLineSegment(sketch, "E369.0.18", {"start": v(398.15, 57.45) * mm, "end": v(398.15, -2.63) * mm});
            skLineSegment(sketch, "E369.0.19", {"start": v(398.15, -2.63) * mm, "end": v(422.13, -2.63) * mm});
            skLineSegment(sketch, "E369.0.20", {"start": v(422.13, -2.63) * mm, "end": v(422.13, -62.46) * mm});
            skLineSegment(sketch, "E369.0.21", {"start": v(422.13, -62.46) * mm, "end": v(398.15, -62.46) * mm});
            skLineSegment(sketch, "E369.0.22", {"start": v(398.15, -62.46) * mm, "end": v(398.15, -122.53) * mm});
            skLineSegment(sketch, "E369.0.23", {"start": v(398.15, -122.53) * mm, "end": v(422.13, -122.53) * mm});
            skLineSegment(sketch, "E369.0.24", {"start": v(422.13, -122.53) * mm, "end": v(422.13, -182.38) * mm});
            skLineSegment(sketch, "E369.0.25", {"start": v(422.13, -182.38) * mm, "end": v(398.15, -182.38) * mm});
            skLineSegment(sketch, "E369.0.26", {"start": v(398.15, -182.38) * mm, "end": v(398.15, -242.45) * mm});
            skLineSegment(sketch, "E369.0.27", {"start": v(398.15, -242.45) * mm, "end": v(422.13, -242.45) * mm});
            skLineSegment(sketch, "E369.0.28", {"start": v(422.13, -242.45) * mm, "end": v(422.13, -302.28) * mm});
            skLineSegment(sketch, "E369.0.29", {"start": v(422.13, -302.28) * mm, "end": v(398.15, -302.28) * mm});
            skLineSegment(sketch, "E369.0.30", {"start": v(398.15, -302.28) * mm, "end": v(398.15, -362.36) * mm});
            skLineSegment(sketch, "E369.0.31", {"start": v(398.15, -362.36) * mm, "end": v(422.13, -362.36) * mm});
            skLineSegment(sketch, "E369.0.32", {"start": v(422.13, -362.36) * mm, "end": v(422.13, -422.19) * mm});
            skLineSegment(sketch, "E369.0.33", {"start": v(422.13, -422.19) * mm, "end": v(398.15, -422.19) * mm});
            skLineSegment(sketch, "E369.0.34", {"start": v(398.15, -422.19) * mm, "end": v(398.15, -482.26) * mm});
            skLineSegment(sketch, "E369.0.35", {"start": v(398.15, -482.26) * mm, "end": v(483.63, -482.26) * mm});
            skLineSegment(sketch, "E369.0.36", {"start": v(483.63, -482.26) * mm, "end": v(483.63, -506.25) * mm});
            skLineSegment(sketch, "E369.0.37", {"start": v(483.63, -506.25) * mm, "end": v(545.24, -506.25) * mm});
            skLineSegment(sketch, "E369.0.38", {"start": v(545.24, -506.25) * mm, "end": v(545.24, -482.26) * mm});
            skLineSegment(sketch, "E369.0.39", {"start": v(545.24, -482.26) * mm, "end": v(606.6, -482.26) * mm});
            skLineSegment(sketch, "E369.0.40", {"start": v(606.6, -482.26) * mm, "end": v(606.6, -506.25) * mm});
            skLineSegment(sketch, "E369.0.41", {"start": v(606.6, -506.25) * mm, "end": v(668.22, -506.25) * mm});
            skLineSegment(sketch, "E369.0.42", {"start": v(668.22, -506.25) * mm, "end": v(668.22, -482.26) * mm});
            skLineSegment(sketch, "E369.0.43", {"start": v(668.22, -482.26) * mm, "end": v(729.59, -482.26) * mm});
            skLineSegment(sketch, "E369.0.44", {"start": v(729.59, -482.26) * mm, "end": v(729.59, -506.25) * mm});
            skLineSegment(sketch, "E369.0.45", {"start": v(729.59, -506.25) * mm, "end": v(791.2, -506.25) * mm});
            skLineSegment(sketch, "E369.0.46", {"start": v(791.2, -506.25) * mm, "end": v(791.2, -482.26) * mm});
            skLineSegment(sketch, "E369.0.47", {"start": v(791.2, -482.26) * mm, "end": v(852.58, -482.26) * mm});
            skLineSegment(sketch, "E369.0.48", {"start": v(852.58, -482.26) * mm, "end": v(852.58, -506.25) * mm});
            skLineSegment(sketch, "E369.0.49", {"start": v(852.58, -506.25) * mm, "end": v(914.19, -506.25) * mm});
            skLineSegment(sketch, "E369.0.50", {"start": v(914.19, -506.25) * mm, "end": v(914.19, -482.26) * mm});
            skLineSegment(sketch, "E369.0.51", {"start": v(914.19, -482.26) * mm, "end": v(975.56, -482.26) * mm});
            skLineSegment(sketch, "E369.0.52", {"start": v(975.56, -482.26) * mm, "end": v(975.56, -506.25) * mm});
            skLineSegment(sketch, "E369.0.53", {"start": v(975.56, -506.25) * mm, "end": v(1037.17, -506.25) * mm});
            skLineSegment(sketch, "E369.0.54", {"start": v(1037.17, -506.25) * mm, "end": v(1037.17, -482.26) * mm});
            skLineSegment(sketch, "E369.0.55", {"start": v(1037.17, -482.26) * mm, "end": v(1098.54, -482.26) * mm});
            skLineSegment(sketch, "E369.0.56", {"start": v(1098.54, -482.26) * mm, "end": v(1098.54, -506.25) * mm});
            skLineSegment(sketch, "E369.0.57", {"start": v(1098.54, -506.25) * mm, "end": v(1160.15, -506.25) * mm});
            skLineSegment(sketch, "E369.0.58", {"start": v(1160.15, -506.25) * mm, "end": v(1160.15, -482.26) * mm});
            skLineSegment(sketch, "E369.0.59", {"start": v(1160.15, -482.26) * mm, "end": v(1221.65, -482.26) * mm});
            skLineSegment(sketch, "E369.0.60", {"start": v(1221.65, -482.26) * mm, "end": v(1221.65, -298) * mm});
            skLineSegment(sketch, "E369.0.61", {"start": v(1221.65, -298) * mm, "end": v(1023.6, -298) * mm});
            skLineSegment(sketch, "E369.0.62", {"start": v(1023.6, -298) * mm, "end": v(1023.6, -284.28) * mm});
            skLineSegment(sketch, "E369.0.63", {"start": v(1023.6, -284.28) * mm, "end": v(1221.65, -284.28) * mm});
            skLineSegment(sketch, "E369.0.64", {"start": v(1221.65, -284.28) * mm, "end": v(1221.65, -215.45) * mm});
            skLineSegment(sketch, "E369.0.65", {"start": v(1221.65, -215.45) * mm, "end": v(1046.47, -215.45) * mm});
            skLineSegment(sketch, "E369.0.66", {"start": v(1046.47, -215.45) * mm, "end": v(1046.47, -201.73) * mm});
            skLineSegment(sketch, "E369.0.67", {"start": v(1046.47, -201.73) * mm, "end": v(1221.65, -201.73) * mm});
            skLineSegment(sketch, "E369.0.68", {"start": v(1221.65, -201.73) * mm, "end": v(1221.65, -132.9) * mm});
            skLineSegment(sketch, "E369.0.69", {"start": v(1221.65, -132.9) * mm, "end": v(980.43, -132.9) * mm});
            skLineSegment(sketch, "E369.0.70", {"start": v(980.43, -132.9) * mm, "end": v(980.43, -119.18) * mm});
            skLineSegment(sketch, "E369.0.71", {"start": v(980.43, -119.18) * mm, "end": v(1221.65, -119.18) * mm});
            skLineSegment(sketch, "E369.0.72", {"start": v(1221.65, -119.18) * mm, "end": v(1221.65, -50.35) * mm});
            skLineSegment(sketch, "E369.0.73", {"start": v(1221.65, -50.35) * mm, "end": v(884.67, -50.35) * mm});
            skLineSegment(sketch, "E369.0.74", {"start": v(884.67, -50.35) * mm, "end": v(884.67, -36.63) * mm});
            skLineSegment(sketch, "E369.0.75", {"start": v(884.67, -36.63) * mm, "end": v(1221.65, -36.63) * mm});
            skLineSegment(sketch, "E369.0.76", {"start": v(1221.65, -36.63) * mm, "end": v(1221.65, 32.2) * mm});
            skLineSegment(sketch, "E369.0.77", {"start": v(1221.65, 32.2) * mm, "end": v(809.48, 32.2) * mm});
            skLineSegment(sketch, "E369.0.78", {"start": v(809.48, 32.2) * mm, "end": v(809.48, 45.92) * mm});
            skLineSegment(sketch, "E369.0.79", {"start": v(809.48, 45.92) * mm, "end": v(1221.65, 45.92) * mm});
            skSolve(sketch);
        }
        {
            var Q0;
            {var subQ2=sQuery(id+"F17.wireOp",EDGE,"E368");Q0=makeQuery(id+"F17.imprint","IMPRINT",FACE,{"disambiguationData":[TD([[makeQuery(id+"F17.imprint","IMPRINT",EDGE,{"derivedFrom":subQ2}),1.0]])]});}
            var Q1;
            {var subQ2=sQuery(id+"F17.wireOp",EDGE,"E368");Q1=makeQuery(id+"F17.imprint","IMPRINT",FACE,{"disambiguationData":[TD([[makeQuery(id+"F17.imprint","IMPRINT",EDGE,{"derivedFrom":subQ2}),1.0]])]});}
            extrude(context, id + "F18", {"entities" : qUnion([Q0, Q1]), "operationType" : NewBodyOperationType.REMOVE, "oppositeDirection" : true, "depth" : 25.4 * mm});
        }
        {
            var Q0;
            Q0=makeQuery(id+"F10.imprint","IMPRINT",FACE,{"disambiguationData":[TD([[makeQuery(id+"F10.imprint","IMPRINT",EDGE,{"derivedFrom":makeQuery(id+"F1.opExtrude","CAP_EDGE",EDGE,{"disambiguationData":[OSD([sQuery(id+"F0.wireOp",EDGE,"E111")])],"isStart":false})}),1.0]])]});
            var sketch = newSketch(context, id + "F19", { "sketchPlane" : qUnion([Q0])});
            skLineSegment(sketch, "E370.0.0", {"start": v(369.29, 237.31) * mm, "end": v(369.29, 297.14) * mm});
            skLineSegment(sketch, "E370.0.1", {"start": v(369.29, 297.14) * mm, "end": v(393.28, 297.14) * mm});
            skLineSegment(sketch, "E370.0.2", {"start": v(393.28, 297.14) * mm, "end": v(393.28, 357.22) * mm});
            skLineSegment(sketch, "E370.0.3", {"start": v(393.28, 357.22) * mm, "end": v(369.29, 357.22) * mm});
            skLineSegment(sketch, "E370.0.4", {"start": v(369.29, 357.22) * mm, "end": v(369.29, 417.05) * mm});
            skLineSegment(sketch, "E370.0.5", {"start": v(369.29, 417.05) * mm, "end": v(-430.22, 417.05) * mm});
            skLineSegment(sketch, "E370.0.6", {"start": v(-430.22, 417.05) * mm, "end": v(-430.22, 357.22) * mm});
            skLineSegment(sketch, "E370.0.7", {"start": v(-430.22, 357.22) * mm, "end": v(-454.2, 357.22) * mm});
            skLineSegment(sketch, "E370.0.8", {"start": v(-454.2, 357.22) * mm, "end": v(-454.2, 297.14) * mm});
            skLineSegment(sketch, "E370.0.9", {"start": v(-454.2, 297.14) * mm, "end": v(-430.22, 297.14) * mm});
            skLineSegment(sketch, "E370.0.10", {"start": v(-430.22, 297.14) * mm, "end": v(-430.22, 237.31) * mm});
            skLineSegment(sketch, "E370.0.11", {"start": v(-430.22, 237.31) * mm, "end": v(-454.2, 237.31) * mm});
            skLineSegment(sketch, "E370.0.12", {"start": v(-454.2, 237.31) * mm, "end": v(-454.2, 177.24) * mm});
            skLineSegment(sketch, "E370.0.13", {"start": v(-454.2, 177.24) * mm, "end": v(-430.22, 177.24) * mm});
            skLineSegment(sketch, "E370.0.14", {"start": v(-430.22, 177.24) * mm, "end": v(-430.22, 117.4) * mm});
            skLineSegment(sketch, "E370.0.15", {"start": v(-430.22, 117.4) * mm, "end": v(-454.2, 117.4) * mm});
            skLineSegment(sketch, "E370.0.16", {"start": v(-454.2, 117.4) * mm, "end": v(-454.2, 57.32) * mm});
            skLineSegment(sketch, "E370.0.17", {"start": v(-454.2, 57.32) * mm, "end": v(-430.22, 57.32) * mm});
            skLineSegment(sketch, "E370.0.18", {"start": v(-430.22, 57.32) * mm, "end": v(-430.22, -2.5) * mm});
            skLineSegment(sketch, "E370.0.19", {"start": v(-430.22, -2.5) * mm, "end": v(-454.2, -2.5) * mm});
            skLineSegment(sketch, "E370.0.20", {"start": v(-454.2, -2.5) * mm, "end": v(-454.2, -62.59) * mm});
            skLineSegment(sketch, "E370.0.21", {"start": v(-454.2, -62.59) * mm, "end": v(-430.22, -62.59) * mm});
            skLineSegment(sketch, "E370.0.22", {"start": v(-430.22, -62.59) * mm, "end": v(-430.22, -122.41) * mm});
            skLineSegment(sketch, "E370.0.23", {"start": v(-430.22, -122.41) * mm, "end": v(-454.2, -122.41) * mm});
            skLineSegment(sketch, "E370.0.24", {"start": v(-454.2, -122.41) * mm, "end": v(-454.2, -182.5) * mm});
            skLineSegment(sketch, "E370.0.25", {"start": v(-454.2, -182.5) * mm, "end": v(-430.22, -182.5) * mm});
            skLineSegment(sketch, "E370.0.26", {"start": v(-430.22, -182.5) * mm, "end": v(-430.22, -242.33) * mm});
            skLineSegment(sketch, "E370.0.27", {"start": v(-430.22, -242.33) * mm, "end": v(-454.2, -242.33) * mm});
            skLineSegment(sketch, "E370.0.28", {"start": v(-454.2, -242.33) * mm, "end": v(-454.2, -302.4) * mm});
            skLineSegment(sketch, "E370.0.29", {"start": v(-454.2, -302.4) * mm, "end": v(-430.22, -302.4) * mm});
            skLineSegment(sketch, "E370.0.30", {"start": v(-430.22, -302.4) * mm, "end": v(-430.22, -362.23) * mm});
            skLineSegment(sketch, "E370.0.31", {"start": v(-430.22, -362.23) * mm, "end": v(-454.2, -362.23) * mm});
            skLineSegment(sketch, "E370.0.32", {"start": v(-454.2, -362.23) * mm, "end": v(-454.2, -422.3) * mm});
            skLineSegment(sketch, "E370.0.33", {"start": v(-454.2, -422.3) * mm, "end": v(-430.22, -422.3) * mm});
            skLineSegment(sketch, "E370.0.34", {"start": v(-430.22, -422.3) * mm, "end": v(-430.22, -482.15) * mm});
            skLineSegment(sketch, "E370.0.35", {"start": v(-430.22, -482.15) * mm, "end": v(-454.2, -482.15) * mm});
            skLineSegment(sketch, "E370.0.36", {"start": v(-454.2, -482.15) * mm, "end": v(-454.2, -506.25) * mm});
            skLineSegment(sketch, "E370.0.37", {"start": v(-454.2, -506.25) * mm, "end": v(-368.61, -506.25) * mm});
            skLineSegment(sketch, "E370.0.38", {"start": v(-368.61, -506.25) * mm, "end": v(-368.61, -482.26) * mm});
            skLineSegment(sketch, "E370.0.39", {"start": v(-368.61, -482.26) * mm, "end": v(-307.24, -482.26) * mm});
            skLineSegment(sketch, "E370.0.40", {"start": v(-307.24, -482.26) * mm, "end": v(-307.24, -506.25) * mm});
            skLineSegment(sketch, "E370.0.41", {"start": v(-307.24, -506.25) * mm, "end": v(-245.62, -506.25) * mm});
            skLineSegment(sketch, "E370.0.42", {"start": v(-245.62, -506.25) * mm, "end": v(-245.62, -482.26) * mm});
            skLineSegment(sketch, "E370.0.43", {"start": v(-245.62, -482.26) * mm, "end": v(-184.26, -482.26) * mm});
            skLineSegment(sketch, "E370.0.44", {"start": v(-184.26, -482.26) * mm, "end": v(-184.26, -506.25) * mm});
            skLineSegment(sketch, "E370.0.45", {"start": v(-184.26, -506.25) * mm, "end": v(-122.64, -506.25) * mm});
            skLineSegment(sketch, "E370.0.46", {"start": v(-122.64, -506.25) * mm, "end": v(-122.64, -482.26) * mm});
            skLineSegment(sketch, "E370.0.47", {"start": v(-122.64, -482.26) * mm, "end": v(-61.27, -482.26) * mm});
            skLineSegment(sketch, "E370.0.48", {"start": v(-61.27, -482.26) * mm, "end": v(-61.27, -506.25) * mm});
            skLineSegment(sketch, "E370.0.49", {"start": v(-61.27, -506.25) * mm, "end": v(0.34, -506.25) * mm});
            skLineSegment(sketch, "E370.0.50", {"start": v(0.34, -506.25) * mm, "end": v(0.34, -482.26) * mm});
            skLineSegment(sketch, "E370.0.51", {"start": v(0.34, -482.26) * mm, "end": v(61.71, -482.26) * mm});
            skLineSegment(sketch, "E370.0.52", {"start": v(61.71, -482.26) * mm, "end": v(61.71, -506.25) * mm});
            skLineSegment(sketch, "E370.0.53", {"start": v(61.71, -506.25) * mm, "end": v(123.33, -506.25) * mm});
            skLineSegment(sketch, "E370.0.54", {"start": v(123.33, -506.25) * mm, "end": v(123.33, -482.26) * mm});
            skLineSegment(sketch, "E370.0.55", {"start": v(123.33, -482.26) * mm, "end": v(184.7, -482.26) * mm});
            skLineSegment(sketch, "E370.0.56", {"start": v(184.7, -482.26) * mm, "end": v(184.7, -506.25) * mm});
            skLineSegment(sketch, "E370.0.57", {"start": v(184.7, -506.25) * mm, "end": v(246.3, -506.25) * mm});
            skLineSegment(sketch, "E370.0.58", {"start": v(246.3, -506.25) * mm, "end": v(246.3, -482.26) * mm});
            skLineSegment(sketch, "E370.0.59", {"start": v(246.3, -482.26) * mm, "end": v(307.69, -482.26) * mm});
            skLineSegment(sketch, "E370.0.60", {"start": v(307.69, -482.26) * mm, "end": v(307.69, -506.25) * mm});
            skLineSegment(sketch, "E370.0.61", {"start": v(307.69, -506.25) * mm, "end": v(393.28, -506.25) * mm});
            skLineSegment(sketch, "E370.0.62", {"start": v(393.28, -506.25) * mm, "end": v(393.28, -482.15) * mm});
            skLineSegment(sketch, "E370.0.63", {"start": v(393.28, -482.15) * mm, "end": v(369.29, -482.15) * mm});
            skLineSegment(sketch, "E370.0.64", {"start": v(369.29, -482.15) * mm, "end": v(369.29, -422.3) * mm});
            skLineSegment(sketch, "E370.0.65", {"start": v(369.29, -422.3) * mm, "end": v(393.28, -422.3) * mm});
            skLineSegment(sketch, "E370.0.66", {"start": v(393.28, -422.3) * mm, "end": v(393.28, -362.23) * mm});
            skLineSegment(sketch, "E370.0.67", {"start": v(393.28, -362.23) * mm, "end": v(369.29, -362.23) * mm});
            skLineSegment(sketch, "E370.0.68", {"start": v(369.29, -362.23) * mm, "end": v(369.29, -302.4) * mm});
            skLineSegment(sketch, "E370.0.69", {"start": v(369.29, -302.4) * mm, "end": v(393.28, -302.4) * mm});
            skLineSegment(sketch, "E370.0.70", {"start": v(393.28, -302.4) * mm, "end": v(393.28, -242.33) * mm});
            skLineSegment(sketch, "E370.0.71", {"start": v(393.28, -242.33) * mm, "end": v(369.29, -242.33) * mm});
            skLineSegment(sketch, "E370.0.72", {"start": v(369.29, -242.33) * mm, "end": v(369.29, -182.5) * mm});
            skLineSegment(sketch, "E370.0.73", {"start": v(369.29, -182.5) * mm, "end": v(393.28, -182.5) * mm});
            skLineSegment(sketch, "E370.0.74", {"start": v(393.28, -182.5) * mm, "end": v(393.28, -122.41) * mm});
            skLineSegment(sketch, "E370.0.75", {"start": v(393.28, -122.41) * mm, "end": v(369.29, -122.41) * mm});
            skLineSegment(sketch, "E370.0.76", {"start": v(369.29, -122.41) * mm, "end": v(369.29, -62.59) * mm});
            skLineSegment(sketch, "E370.0.77", {"start": v(369.29, -62.59) * mm, "end": v(393.28, -62.59) * mm});
            skLineSegment(sketch, "E370.0.78", {"start": v(393.28, -62.59) * mm, "end": v(393.28, -2.5) * mm});
            skLineSegment(sketch, "E370.0.79", {"start": v(393.28, -2.5) * mm, "end": v(369.29, -2.5) * mm});
            skLineSegment(sketch, "E370.0.80", {"start": v(369.29, -2.5) * mm, "end": v(369.29, 57.32) * mm});
            skLineSegment(sketch, "E370.0.81", {"start": v(369.29, 57.32) * mm, "end": v(393.28, 57.32) * mm});
            skLineSegment(sketch, "E370.0.82", {"start": v(393.28, 57.32) * mm, "end": v(393.28, 117.4) * mm});
            skLineSegment(sketch, "E370.0.83", {"start": v(393.28, 117.4) * mm, "end": v(369.29, 117.4) * mm});
            skLineSegment(sketch, "E370.0.84", {"start": v(369.29, 117.4) * mm, "end": v(369.29, 177.24) * mm});
            skLineSegment(sketch, "E370.0.85", {"start": v(369.29, 177.24) * mm, "end": v(393.28, 177.24) * mm});
            skLineSegment(sketch, "E370.0.86", {"start": v(393.28, 177.24) * mm, "end": v(393.28, 237.31) * mm});
            skLineSegment(sketch, "E370.0.87", {"start": v(393.28, 237.31) * mm, "end": v(369.29, 237.31) * mm});
            skLineSegment(sketch, "E371", {"start": v(-430.22, 177.24) * mm, "end": v(369.29, 177.24) * mm});
            skSolve(sketch);
        }
        {
            var Q0;
            {var subQ10=sQuery(id+"F19.wireOp",EDGE,"E370.0.6");Q0=makeQuery(id+"F19.imprint","IMPRINT",FACE,{"disambiguationData":[TD([[makeQuery(id+"F19.imprint","IMPRINT",EDGE,{"derivedFrom":subQ10}),1.0]])]});}
            var Q1;
            Q1=makeQuery(id+"F19.imprint","IMPRINT",FACE,{"disambiguationData":[TD([[makeQuery(id+"F19.imprint","IMPRINT",EDGE,{"derivedFrom":sQuery(id+"F19.wireOp",EDGE,"E370.0.0")}),1.0]])]});
            extrude(context, id + "F20", {"entities" : qUnion([Q0, Q1]), "operationType" : NewBodyOperationType.REMOVE, "oppositeDirection" : true, "depth" : 25.4 * mm});
        }
        {
            var Q0;
            Q0=makeQuery(id+"F1.opExtrude","CAP_FACE",FACE,{"disambiguationData":[OSD([sQuery(id+"F0.wireOp",EDGE,"E77"),sQuery(id+"F0.wireOp",EDGE,"E78"),sQuery(id+"F0.wireOp",EDGE,"E79"),sQuery(id+"F0.wireOp",EDGE,"E80"),sQuery(id+"F0.wireOp",EDGE,"E81"),sQuery(id+"F0.wireOp",EDGE,"E82"),sQuery(id+"F0.wireOp",EDGE,"E83"),sQuery(id+"F0.wireOp",EDGE,"E84"),sQuery(id+"F0.wireOp",EDGE,"E85"),sQuery(id+"F0.wireOp",EDGE,"E86"),sQuery(id+"F0.wireOp",EDGE,"E87"),sQuery(id+"F0.wireOp",EDGE,"E88"),sQuery(id+"F0.wireOp",EDGE,"E89"),sQuery(id+"F0.wireOp",EDGE,"E90"),sQuery(id+"F0.wireOp",EDGE,"E91"),sQuery(id+"F0.wireOp",EDGE,"E92"),sQuery(id+"F0.wireOp",EDGE,"E93"),sQuery(id+"F0.wireOp",EDGE,"E94"),sQuery(id+"F0.wireOp",EDGE,"E95"),sQuery(id+"F0.wireOp",EDGE,"E96"),sQuery(id+"F0.wireOp",EDGE,"E97"),sQuery(id+"F0.wireOp",EDGE,"E98"),sQuery(id+"F0.wireOp",EDGE,"E99"),sQuery(id+"F0.wireOp",EDGE,"E100"),sQuery(id+"F0.wireOp",EDGE,"E102"),sQuery(id+"F0.wireOp",EDGE,"E103"),sQuery(id+"F0.wireOp",EDGE,"E104"),sQuery(id+"F0.wireOp",EDGE,"E105"),sQuery(id+"F0.wireOp",EDGE,"E106"),sQuery(id+"F0.wireOp",EDGE,"E107"),sQuery(id+"F0.wireOp",EDGE,"E108"),sQuery(id+"F0.wireOp",EDGE,"E109"),sQuery(id+"F0.wireOp",EDGE,"E110"),sQuery(id+"F0.wireOp",EDGE,"E111"),sQuery(id+"F0.wireOp",EDGE,"E112"),sQuery(id+"F0.wireOp",EDGE,"E113"),sQuery(id+"F0.wireOp",EDGE,"E114"),sQuery(id+"F0.wireOp",EDGE,"E115"),sQuery(id+"F0.wireOp",EDGE,"E116"),sQuery(id+"F0.wireOp",EDGE,"E117"),sQuery(id+"F0.wireOp",EDGE,"E118"),sQuery(id+"F0.wireOp",EDGE,"E119"),sQuery(id+"F0.wireOp",EDGE,"E120"),sQuery(id+"F0.wireOp",EDGE,"E121"),sQuery(id+"F0.wireOp",EDGE,"E122"),sQuery(id+"F0.wireOp",EDGE,"E123"),sQuery(id+"F0.wireOp",EDGE,"E124"),sQuery(id+"F0.wireOp",EDGE,"E125"),sQuery(id+"F0.wireOp",EDGE,"E126"),sQuery(id+"F0.wireOp",EDGE,"E127"),sQuery(id+"F0.wireOp",EDGE,"E128"),sQuery(id+"F0.wireOp",EDGE,"E129"),sQuery(id+"F0.wireOp",EDGE,"E130"),sQuery(id+"F0.wireOp",EDGE,"E131"),sQuery(id+"F0.wireOp",EDGE,"E132"),sQuery(id+"F0.wireOp",EDGE,"E133"),sQuery(id+"F0.wireOp",EDGE,"E134"),sQuery(id+"F0.wireOp",EDGE,"E135"),sQuery(id+"F0.wireOp",EDGE,"E136"),sQuery(id+"F0.wireOp",EDGE,"E137"),sQuery(id+"F0.wireOp",EDGE,"E138"),sQuery(id+"F0.wireOp",EDGE,"E139"),sQuery(id+"F0.wireOp",EDGE,"E140"),sQuery(id+"F0.wireOp",EDGE,"E141"),sQuery(id+"F0.wireOp",EDGE,"E142"),sQuery(id+"F0.wireOp",EDGE,"E143"),sQuery(id+"F0.wireOp",EDGE,"E144"),sQuery(id+"F0.wireOp",EDGE,"E145"),sQuery(id+"F0.wireOp",EDGE,"E146"),sQuery(id+"F0.wireOp",EDGE,"E147"),sQuery(id+"F0.wireOp",EDGE,"E148"),sQuery(id+"F0.wireOp",EDGE,"E149"),sQuery(id+"F0.wireOp",EDGE,"E150"),sQuery(id+"F0.wireOp",EDGE,"E151"),sQuery(id+"F0.wireOp",EDGE,"E152"),sQuery(id+"F0.wireOp",EDGE,"E153"),sQuery(id+"F0.wireOp",EDGE,"E154"),sQuery(id+"F0.wireOp",EDGE,"E155"),sQuery(id+"F0.wireOp",EDGE,"E156"),sQuery(id+"F0.wireOp",EDGE,"E157"),sQuery(id+"F0.wireOp",EDGE,"E158"),sQuery(id+"F0.wireOp",EDGE,"E159"),sQuery(id+"F0.wireOp",EDGE,"E160"),sQuery(id+"F0.wireOp",EDGE,"E161"),sQuery(id+"F0.wireOp",EDGE,"E162"),sQuery(id+"F0.wireOp",EDGE,"E163"),sQuery(id+"F0.wireOp",EDGE,"E164"),sQuery(id+"F0.wireOp",EDGE,"E165"),sQuery(id+"F0.wireOp",EDGE,"E280"),sQuery(id+"F0.wireOp",EDGE,"E286"),sQuery(id+"F0.wireOp",EDGE,"E287")])],"isStart":false});
            var sketch = newSketch(context, id + "F21", { "sketchPlane" : qUnion([Q0])});
            skLineSegment(sketch, "E372", {"start": v(343.89, 177.24) * mm, "end": v(-404.82, 177.24) * mm});
            skLineSegment(sketch, "E373", {"start": v(-404.82, 117.4) * mm, "end": v(343.89, 117.4) * mm});
            skLineSegment(sketch, "E374.0", {"start": v(-404.82, 177.24) * mm, "end": v(-404.82, -456.86) * mm});
            skLineSegment(sketch, "E375.0", {"start": v(343.89, 177.24) * mm, "end": v(343.89, -456.86) * mm});
            skSolve(sketch);
        }
        {
            var Q0;
            {var subQ0=sQuery(id+"F21.wireOp",EDGE,"E372");Q0=makeQuery(id+"F21.imprint","IMPRINT",FACE,{"disambiguationData":[TD([[makeQuery(id+"F21.imprint","IMPRINT",EDGE,{"derivedFrom":subQ0}),1.0]])]});}
            extrude(context, id + "F22", {"entities" : qUnion([Q0]), "operationType" : NewBodyOperationType.ADD, "oppositeDirection" : true, "depth" : 25.4 * mm});
        }
        {
            var Q0;
            Q0=makeQuery(id+"F1.opExtrude","CAP_FACE",FACE,{"disambiguationData":[OSD([sQuery(id+"F0.wireOp",EDGE,"E167"),sQuery(id+"F0.wireOp",EDGE,"E168"),sQuery(id+"F0.wireOp",EDGE,"E169"),sQuery(id+"F0.wireOp",EDGE,"E170"),sQuery(id+"F0.wireOp",EDGE,"E171"),sQuery(id+"F0.wireOp",EDGE,"E172"),sQuery(id+"F0.wireOp",EDGE,"E173"),sQuery(id+"F0.wireOp",EDGE,"E174"),sQuery(id+"F0.wireOp",EDGE,"E175"),sQuery(id+"F0.wireOp",EDGE,"E176"),sQuery(id+"F0.wireOp",EDGE,"E177"),sQuery(id+"F0.wireOp",EDGE,"E178"),sQuery(id+"F0.wireOp",EDGE,"E179"),sQuery(id+"F0.wireOp",EDGE,"E180"),sQuery(id+"F0.wireOp",EDGE,"E181"),sQuery(id+"F0.wireOp",EDGE,"E182"),sQuery(id+"F0.wireOp",EDGE,"E183"),sQuery(id+"F0.wireOp",EDGE,"E184"),sQuery(id+"F0.wireOp",EDGE,"E185"),sQuery(id+"F0.wireOp",EDGE,"E186"),sQuery(id+"F0.wireOp",EDGE,"E187"),sQuery(id+"F0.wireOp",EDGE,"E188"),sQuery(id+"F0.wireOp",EDGE,"E189"),sQuery(id+"F0.wireOp",EDGE,"E190"),sQuery(id+"F0.wireOp",EDGE,"E191"),sQuery(id+"F0.wireOp",EDGE,"E192"),sQuery(id+"F0.wireOp",EDGE,"E193"),sQuery(id+"F0.wireOp",EDGE,"E194"),sQuery(id+"F0.wireOp",EDGE,"E195"),sQuery(id+"F0.wireOp",EDGE,"E196"),sQuery(id+"F0.wireOp",EDGE,"E197"),sQuery(id+"F0.wireOp",EDGE,"E198"),sQuery(id+"F0.wireOp",EDGE,"E199"),sQuery(id+"F0.wireOp",EDGE,"E200"),sQuery(id+"F0.wireOp",EDGE,"E201"),sQuery(id+"F0.wireOp",EDGE,"E202"),sQuery(id+"F0.wireOp",EDGE,"E203"),sQuery(id+"F0.wireOp",EDGE,"E204"),sQuery(id+"F0.wireOp",EDGE,"E205"),sQuery(id+"F0.wireOp",EDGE,"E206"),sQuery(id+"F0.wireOp",EDGE,"E207"),sQuery(id+"F0.wireOp",EDGE,"E208"),sQuery(id+"F0.wireOp",EDGE,"E209"),sQuery(id+"F0.wireOp",EDGE,"E210"),sQuery(id+"F0.wireOp",EDGE,"E211"),sQuery(id+"F0.wireOp",EDGE,"E212"),sQuery(id+"F0.wireOp",EDGE,"E213"),sQuery(id+"F0.wireOp",EDGE,"E214"),sQuery(id+"F0.wireOp",EDGE,"E215"),sQuery(id+"F0.wireOp",EDGE,"E216"),sQuery(id+"F0.wireOp",EDGE,"E217"),sQuery(id+"F0.wireOp",EDGE,"E218"),sQuery(id+"F0.wireOp",EDGE,"E219"),sQuery(id+"F0.wireOp",EDGE,"E220"),sQuery(id+"F0.wireOp",EDGE,"E221"),sQuery(id+"F0.wireOp",EDGE,"E278"),sQuery(id+"F0.wireOp",EDGE,"E279")])],"isStart":false});
            var sketch = newSketch(context, id + "F23", { "sketchPlane" : qUnion([Q0])});
            skLineSegment(sketch, "E376", {"start": v(-1282.57, 177.36) * mm, "end": v(-1282.57, 370.9) * mm, "construction": true});
            skLineSegment(sketch, "E377.0.0", {"start": v(1221.65, 128.47) * mm, "end": v(1221.65, 177.36) * mm});
            skLineSegment(sketch, "E377.0.1", {"start": v(1221.65, 177.36) * mm, "end": v(398.15, 177.36) * mm});
            skLineSegment(sketch, "E377.0.2", {"start": v(398.15, 177.36) * mm, "end": v(398.15, 117.28) * mm});
            skLineSegment(sketch, "E377.0.3", {"start": v(398.15, 117.28) * mm, "end": v(422.13, 117.28) * mm});
            skLineSegment(sketch, "E377.0.4", {"start": v(422.13, 117.28) * mm, "end": v(422.13, 57.45) * mm});
            skLineSegment(sketch, "E377.0.5", {"start": v(422.13, 57.45) * mm, "end": v(398.15, 57.45) * mm});
            skLineSegment(sketch, "E377.0.6", {"start": v(398.15, 57.45) * mm, "end": v(398.15, -2.63) * mm});
            skLineSegment(sketch, "E377.0.7", {"start": v(398.15, -2.63) * mm, "end": v(422.13, -2.63) * mm});
            skLineSegment(sketch, "E377.0.8", {"start": v(422.13, -2.63) * mm, "end": v(422.13, -62.46) * mm});
            skLineSegment(sketch, "E377.0.9", {"start": v(422.13, -62.46) * mm, "end": v(398.15, -62.46) * mm});
            skLineSegment(sketch, "E377.0.10", {"start": v(398.15, -62.46) * mm, "end": v(398.15, -122.53) * mm});
            skLineSegment(sketch, "E377.0.11", {"start": v(398.15, -122.53) * mm, "end": v(422.13, -122.53) * mm});
            skLineSegment(sketch, "E377.0.12", {"start": v(422.13, -122.53) * mm, "end": v(422.13, -182.38) * mm});
            skLineSegment(sketch, "E377.0.13", {"start": v(422.13, -182.38) * mm, "end": v(398.15, -182.38) * mm});
            skLineSegment(sketch, "E377.0.14", {"start": v(398.15, -182.38) * mm, "end": v(398.15, -242.45) * mm});
            skLineSegment(sketch, "E377.0.15", {"start": v(398.15, -242.45) * mm, "end": v(422.13, -242.45) * mm});
            skLineSegment(sketch, "E377.0.16", {"start": v(422.13, -242.45) * mm, "end": v(422.13, -302.28) * mm});
            skLineSegment(sketch, "E377.0.17", {"start": v(422.13, -302.28) * mm, "end": v(398.15, -302.28) * mm});
            skLineSegment(sketch, "E377.0.18", {"start": v(398.15, -302.28) * mm, "end": v(398.15, -362.36) * mm});
            skLineSegment(sketch, "E377.0.19", {"start": v(398.15, -362.36) * mm, "end": v(422.13, -362.36) * mm});
            skLineSegment(sketch, "E377.0.20", {"start": v(422.13, -362.36) * mm, "end": v(422.13, -422.19) * mm});
            skLineSegment(sketch, "E377.0.21", {"start": v(422.13, -422.19) * mm, "end": v(398.15, -422.19) * mm});
            skLineSegment(sketch, "E377.0.22", {"start": v(398.15, -422.19) * mm, "end": v(398.15, -482.26) * mm});
            skLineSegment(sketch, "E377.0.23", {"start": v(398.15, -482.26) * mm, "end": v(483.63, -482.26) * mm});
            skLineSegment(sketch, "E377.0.24", {"start": v(483.63, -482.26) * mm, "end": v(483.63, -506.25) * mm});
            skLineSegment(sketch, "E377.0.25", {"start": v(483.63, -506.25) * mm, "end": v(545.24, -506.25) * mm});
            skLineSegment(sketch, "E377.0.26", {"start": v(545.24, -506.25) * mm, "end": v(545.24, -482.26) * mm});
            skLineSegment(sketch, "E377.0.27", {"start": v(545.24, -482.26) * mm, "end": v(606.6, -482.26) * mm});
            skLineSegment(sketch, "E377.0.28", {"start": v(606.6, -482.26) * mm, "end": v(606.6, -506.25) * mm});
            skLineSegment(sketch, "E377.0.29", {"start": v(606.6, -506.25) * mm, "end": v(668.22, -506.25) * mm});
            skLineSegment(sketch, "E377.0.30", {"start": v(668.22, -506.25) * mm, "end": v(668.22, -482.26) * mm});
            skLineSegment(sketch, "E377.0.31", {"start": v(668.22, -482.26) * mm, "end": v(729.59, -482.26) * mm});
            skLineSegment(sketch, "E377.0.32", {"start": v(729.59, -482.26) * mm, "end": v(729.59, -506.25) * mm});
            skLineSegment(sketch, "E377.0.33", {"start": v(729.59, -506.25) * mm, "end": v(791.2, -506.25) * mm});
            skLineSegment(sketch, "E377.0.34", {"start": v(791.2, -506.25) * mm, "end": v(791.2, -482.26) * mm});
            skLineSegment(sketch, "E377.0.35", {"start": v(791.2, -482.26) * mm, "end": v(852.58, -482.26) * mm});
            skLineSegment(sketch, "E377.0.36", {"start": v(852.58, -482.26) * mm, "end": v(852.58, -506.25) * mm});
            skLineSegment(sketch, "E377.0.37", {"start": v(852.58, -506.25) * mm, "end": v(914.19, -506.25) * mm});
            skLineSegment(sketch, "E377.0.38", {"start": v(914.19, -506.25) * mm, "end": v(914.19, -482.26) * mm});
            skLineSegment(sketch, "E377.0.39", {"start": v(914.19, -482.26) * mm, "end": v(975.56, -482.26) * mm});
            skLineSegment(sketch, "E377.0.40", {"start": v(975.56, -482.26) * mm, "end": v(975.56, -506.25) * mm});
            skLineSegment(sketch, "E377.0.41", {"start": v(975.56, -506.25) * mm, "end": v(1037.17, -506.25) * mm});
            skLineSegment(sketch, "E377.0.42", {"start": v(1037.17, -506.25) * mm, "end": v(1037.17, -482.26) * mm});
            skLineSegment(sketch, "E377.0.43", {"start": v(1037.17, -482.26) * mm, "end": v(1098.54, -482.26) * mm});
            skLineSegment(sketch, "E377.0.44", {"start": v(1098.54, -482.26) * mm, "end": v(1098.54, -506.25) * mm});
            skLineSegment(sketch, "E377.0.45", {"start": v(1098.54, -506.25) * mm, "end": v(1160.15, -506.25) * mm});
            skLineSegment(sketch, "E377.0.46", {"start": v(1160.15, -506.25) * mm, "end": v(1160.15, -482.26) * mm});
            skLineSegment(sketch, "E377.0.47", {"start": v(1160.15, -482.26) * mm, "end": v(1221.65, -482.26) * mm});
            skLineSegment(sketch, "E377.0.48", {"start": v(1221.65, -482.26) * mm, "end": v(1221.65, -298) * mm});
            skLineSegment(sketch, "E377.0.49", {"start": v(1221.65, -298) * mm, "end": v(1023.6, -298) * mm});
            skLineSegment(sketch, "E377.0.50", {"start": v(1023.6, -298) * mm, "end": v(1023.6, -284.28) * mm});
            skLineSegment(sketch, "E377.0.51", {"start": v(1023.6, -284.28) * mm, "end": v(1221.65, -284.28) * mm});
            skLineSegment(sketch, "E377.0.52", {"start": v(1221.65, -284.28) * mm, "end": v(1221.65, -215.45) * mm});
            skLineSegment(sketch, "E377.0.53", {"start": v(1221.65, -215.45) * mm, "end": v(1046.47, -215.45) * mm});
            skLineSegment(sketch, "E377.0.54", {"start": v(1046.47, -215.45) * mm, "end": v(1046.47, -201.73) * mm});
            skLineSegment(sketch, "E377.0.55", {"start": v(1046.47, -201.73) * mm, "end": v(1221.65, -201.73) * mm});
            skLineSegment(sketch, "E377.0.56", {"start": v(1221.65, -201.73) * mm, "end": v(1221.65, -132.9) * mm});
            skLineSegment(sketch, "E377.0.57", {"start": v(1221.65, -132.9) * mm, "end": v(980.43, -132.9) * mm});
            skLineSegment(sketch, "E377.0.58", {"start": v(980.43, -132.9) * mm, "end": v(980.43, -119.18) * mm});
            skLineSegment(sketch, "E377.0.59", {"start": v(980.43, -119.18) * mm, "end": v(1221.65, -119.18) * mm});
            skLineSegment(sketch, "E377.0.60", {"start": v(1221.65, -119.18) * mm, "end": v(1221.65, -50.35) * mm});
            skLineSegment(sketch, "E377.0.61", {"start": v(1221.65, -50.35) * mm, "end": v(884.67, -50.35) * mm});
            skLineSegment(sketch, "E377.0.62", {"start": v(884.67, -50.35) * mm, "end": v(884.67, -36.63) * mm});
            skLineSegment(sketch, "E377.0.63", {"start": v(884.67, -36.63) * mm, "end": v(1221.65, -36.63) * mm});
            skLineSegment(sketch, "E377.0.64", {"start": v(1221.65, -36.63) * mm, "end": v(1221.65, 32.2) * mm});
            skLineSegment(sketch, "E377.0.65", {"start": v(1221.65, 32.2) * mm, "end": v(809.48, 32.2) * mm});
            skLineSegment(sketch, "E377.0.66", {"start": v(809.48, 32.2) * mm, "end": v(809.48, 45.92) * mm});
            skLineSegment(sketch, "E377.0.67", {"start": v(809.48, 45.92) * mm, "end": v(1221.65, 45.92) * mm});
            skLineSegment(sketch, "E377.0.68", {"start": v(1221.65, 45.92) * mm, "end": v(1221.65, 114.75) * mm});
            skLineSegment(sketch, "E377.0.69", {"start": v(1221.65, 114.75) * mm, "end": v(737.6, 114.75) * mm});
            skLineSegment(sketch, "E377.0.70", {"start": v(737.6, 114.75) * mm, "end": v(737.6, 128.47) * mm});
            skLineSegment(sketch, "E377.0.71", {"start": v(737.6, 128.47) * mm, "end": v(1221.65, 128.47) * mm});
            skLineSegment(sketch, "E378.0.0", {"start": v(-459.08, 177.36) * mm, "end": v(-1282.57, 177.36) * mm});
            skLineSegment(sketch, "E378.0.1", {"start": v(-1282.57, 177.36) * mm, "end": v(-1282.57, 128.47) * mm});
            skLineSegment(sketch, "E378.0.2", {"start": v(-1282.57, 128.47) * mm, "end": v(-798.52, 128.47) * mm});
            skLineSegment(sketch, "E378.0.3", {"start": v(-798.52, 128.47) * mm, "end": v(-798.52, 114.75) * mm});
            skLineSegment(sketch, "E378.0.4", {"start": v(-798.52, 114.75) * mm, "end": v(-1282.57, 114.75) * mm});
            skLineSegment(sketch, "E378.0.5", {"start": v(-1282.57, 114.75) * mm, "end": v(-1282.57, 45.92) * mm});
            skLineSegment(sketch, "E378.0.6", {"start": v(-1282.57, 45.92) * mm, "end": v(-870.4, 45.92) * mm});
            skLineSegment(sketch, "E378.0.7", {"start": v(-870.4, 45.92) * mm, "end": v(-870.4, 32.2) * mm});
            skLineSegment(sketch, "E378.0.8", {"start": v(-870.4, 32.2) * mm, "end": v(-1282.57, 32.2) * mm});
            skLineSegment(sketch, "E378.0.9", {"start": v(-1282.57, 32.2) * mm, "end": v(-1282.57, -36.63) * mm});
            skLineSegment(sketch, "E378.0.10", {"start": v(-1282.57, -36.63) * mm, "end": v(-945.59, -36.63) * mm});
            skLineSegment(sketch, "E378.0.11", {"start": v(-945.59, -36.63) * mm, "end": v(-945.59, -50.35) * mm});
            skLineSegment(sketch, "E378.0.12", {"start": v(-945.59, -50.35) * mm, "end": v(-1282.57, -50.35) * mm});
            skLineSegment(sketch, "E378.0.13", {"start": v(-1282.57, -50.35) * mm, "end": v(-1282.57, -119.18) * mm});
            skLineSegment(sketch, "E378.0.14", {"start": v(-1282.57, -119.18) * mm, "end": v(-1041.35, -119.18) * mm});
            skLineSegment(sketch, "E378.0.15", {"start": v(-1041.35, -119.18) * mm, "end": v(-1041.35, -132.9) * mm});
            skLineSegment(sketch, "E378.0.16", {"start": v(-1041.35, -132.9) * mm, "end": v(-1282.57, -132.9) * mm});
            skLineSegment(sketch, "E378.0.17", {"start": v(-1282.57, -132.9) * mm, "end": v(-1282.57, -201.73) * mm});
            skLineSegment(sketch, "E378.0.18", {"start": v(-1282.57, -201.73) * mm, "end": v(-1107.39, -201.73) * mm});
            skLineSegment(sketch, "E378.0.19", {"start": v(-1107.39, -201.73) * mm, "end": v(-1107.39, -215.45) * mm});
            skLineSegment(sketch, "E378.0.20", {"start": v(-1107.39, -215.45) * mm, "end": v(-1282.57, -215.45) * mm});
            skLineSegment(sketch, "E378.0.21", {"start": v(-1282.57, -215.45) * mm, "end": v(-1282.57, -284.28) * mm});
            skLineSegment(sketch, "E378.0.22", {"start": v(-1282.57, -284.28) * mm, "end": v(-1084.53, -284.28) * mm});
            skLineSegment(sketch, "E378.0.23", {"start": v(-1084.53, -284.28) * mm, "end": v(-1084.53, -298) * mm});
            skLineSegment(sketch, "E378.0.24", {"start": v(-1084.53, -298) * mm, "end": v(-1282.57, -298) * mm});
            skLineSegment(sketch, "E378.0.25", {"start": v(-1282.57, -298) * mm, "end": v(-1282.57, -482.26) * mm});
            skLineSegment(sketch, "E378.0.26", {"start": v(-1282.57, -482.26) * mm, "end": v(-1221.08, -482.26) * mm});
            skLineSegment(sketch, "E378.0.27", {"start": v(-1221.08, -482.26) * mm, "end": v(-1221.08, -506.25) * mm});
            skLineSegment(sketch, "E378.0.28", {"start": v(-1221.08, -506.25) * mm, "end": v(-1159.47, -506.25) * mm});
            skLineSegment(sketch, "E378.0.29", {"start": v(-1159.47, -506.25) * mm, "end": v(-1159.47, -482.26) * mm});
            skLineSegment(sketch, "E378.0.30", {"start": v(-1159.47, -482.26) * mm, "end": v(-1098.1, -482.26) * mm});
            skLineSegment(sketch, "E378.0.31", {"start": v(-1098.1, -482.26) * mm, "end": v(-1098.1, -506.25) * mm});
            skLineSegment(sketch, "E378.0.32", {"start": v(-1098.1, -506.25) * mm, "end": v(-1036.48, -506.25) * mm});
            skLineSegment(sketch, "E378.0.33", {"start": v(-1036.48, -506.25) * mm, "end": v(-1036.48, -482.26) * mm});
            skLineSegment(sketch, "E378.0.34", {"start": v(-1036.48, -482.26) * mm, "end": v(-975.11, -482.26) * mm});
            skLineSegment(sketch, "E378.0.35", {"start": v(-975.11, -482.26) * mm, "end": v(-975.11, -506.25) * mm});
            skLineSegment(sketch, "E378.0.36", {"start": v(-975.11, -506.25) * mm, "end": v(-913.5, -506.25) * mm});
            skLineSegment(sketch, "E378.0.37", {"start": v(-913.5, -506.25) * mm, "end": v(-913.5, -482.26) * mm});
            skLineSegment(sketch, "E378.0.38", {"start": v(-913.5, -482.26) * mm, "end": v(-852.13, -482.26) * mm});
            skLineSegment(sketch, "E378.0.39", {"start": v(-852.13, -482.26) * mm, "end": v(-852.13, -506.25) * mm});
            skLineSegment(sketch, "E378.0.40", {"start": v(-852.13, -506.25) * mm, "end": v(-790.52, -506.25) * mm});
            skLineSegment(sketch, "E378.0.41", {"start": v(-790.52, -506.25) * mm, "end": v(-790.52, -482.26) * mm});
            skLineSegment(sketch, "E378.0.42", {"start": v(-790.52, -482.26) * mm, "end": v(-729.15, -482.26) * mm});
            skLineSegment(sketch, "E378.0.43", {"start": v(-729.15, -482.26) * mm, "end": v(-729.15, -506.25) * mm});
            skLineSegment(sketch, "E378.0.44", {"start": v(-729.15, -506.25) * mm, "end": v(-667.53, -506.25) * mm});
            skLineSegment(sketch, "E378.0.45", {"start": v(-667.53, -506.25) * mm, "end": v(-667.53, -482.26) * mm});
            skLineSegment(sketch, "E378.0.46", {"start": v(-667.53, -482.26) * mm, "end": v(-606.17, -482.26) * mm});
            skLineSegment(sketch, "E378.0.47", {"start": v(-606.17, -482.26) * mm, "end": v(-606.17, -506.25) * mm});
            skLineSegment(sketch, "E378.0.48", {"start": v(-606.17, -506.25) * mm, "end": v(-544.55, -506.25) * mm});
            skLineSegment(sketch, "E378.0.49", {"start": v(-544.55, -506.25) * mm, "end": v(-544.55, -482.26) * mm});
            skLineSegment(sketch, "E378.0.50", {"start": v(-544.55, -482.26) * mm, "end": v(-459.08, -482.26) * mm});
            skLineSegment(sketch, "E378.0.51", {"start": v(-459.08, -482.26) * mm, "end": v(-459.08, -422.19) * mm});
            skLineSegment(sketch, "E378.0.52", {"start": v(-459.08, -422.19) * mm, "end": v(-483.06, -422.19) * mm});
            skLineSegment(sketch, "E378.0.53", {"start": v(-483.06, -422.19) * mm, "end": v(-483.06, -362.36) * mm});
            skLineSegment(sketch, "E378.0.54", {"start": v(-483.06, -362.36) * mm, "end": v(-459.08, -362.36) * mm});
            skLineSegment(sketch, "E378.0.55", {"start": v(-459.08, -362.36) * mm, "end": v(-459.08, -302.28) * mm});
            skLineSegment(sketch, "E378.0.56", {"start": v(-459.08, -302.28) * mm, "end": v(-483.06, -302.28) * mm});
            skLineSegment(sketch, "E378.0.57", {"start": v(-483.06, -302.28) * mm, "end": v(-483.06, -242.45) * mm});
            skLineSegment(sketch, "E378.0.58", {"start": v(-483.06, -242.45) * mm, "end": v(-459.08, -242.45) * mm});
            skLineSegment(sketch, "E378.0.59", {"start": v(-459.08, -242.45) * mm, "end": v(-459.08, -182.38) * mm});
            skLineSegment(sketch, "E378.0.60", {"start": v(-459.08, -182.38) * mm, "end": v(-483.06, -182.38) * mm});
            skLineSegment(sketch, "E378.0.61", {"start": v(-483.06, -182.38) * mm, "end": v(-483.06, -122.53) * mm});
            skLineSegment(sketch, "E378.0.62", {"start": v(-483.06, -122.53) * mm, "end": v(-459.08, -122.53) * mm});
            skLineSegment(sketch, "E378.0.63", {"start": v(-459.08, -122.53) * mm, "end": v(-459.08, -62.46) * mm});
            skLineSegment(sketch, "E378.0.64", {"start": v(-459.08, -62.46) * mm, "end": v(-483.06, -62.46) * mm});
            skLineSegment(sketch, "E378.0.65", {"start": v(-483.06, -62.46) * mm, "end": v(-483.06, -2.63) * mm});
            skLineSegment(sketch, "E378.0.66", {"start": v(-483.06, -2.63) * mm, "end": v(-459.08, -2.63) * mm});
            skLineSegment(sketch, "E378.0.67", {"start": v(-459.08, -2.63) * mm, "end": v(-459.08, 57.45) * mm});
            skLineSegment(sketch, "E378.0.68", {"start": v(-459.08, 57.45) * mm, "end": v(-483.06, 57.45) * mm});
            skLineSegment(sketch, "E378.0.69", {"start": v(-483.06, 57.45) * mm, "end": v(-483.06, 117.28) * mm});
            skLineSegment(sketch, "E378.0.70", {"start": v(-483.06, 117.28) * mm, "end": v(-459.08, 117.28) * mm});
            skLineSegment(sketch, "E378.0.71", {"start": v(-459.08, 117.28) * mm, "end": v(-459.08, 177.36) * mm});
            skLineSegment(sketch, "E379.0.0", {"start": v(-454.2, -842.69) * mm, "end": v(393.28, -842.69) * mm});
            skLineSegment(sketch, "E379.0.1", {"start": v(393.28, -842.69) * mm, "end": v(393.28, -781.07) * mm});
            skLineSegment(sketch, "E379.0.2", {"start": v(393.28, -781.07) * mm, "end": v(369.29, -781.07) * mm});
            skLineSegment(sketch, "E379.0.3", {"start": v(369.29, -781.07) * mm, "end": v(369.29, -719.7) * mm});
            skLineSegment(sketch, "E379.0.4", {"start": v(369.29, -719.7) * mm, "end": v(393.28, -719.7) * mm});
            skLineSegment(sketch, "E379.0.5", {"start": v(393.28, -719.7) * mm, "end": v(393.28, -658.1) * mm});
            skLineSegment(sketch, "E379.0.6", {"start": v(393.28, -658.1) * mm, "end": v(369.29, -658.1) * mm});
            skLineSegment(sketch, "E379.0.7", {"start": v(369.29, -658.1) * mm, "end": v(369.29, -596.71) * mm});
            skLineSegment(sketch, "E379.0.8", {"start": v(369.29, -596.71) * mm, "end": v(393.28, -596.71) * mm});
            skLineSegment(sketch, "E379.0.9", {"start": v(393.28, -596.71) * mm, "end": v(393.28, -535.1) * mm});
            skLineSegment(sketch, "E379.0.10", {"start": v(393.28, -535.1) * mm, "end": v(307.8, -535.1) * mm});
            skLineSegment(sketch, "E379.0.11", {"start": v(307.8, -535.1) * mm, "end": v(307.8, -511.12) * mm});
            skLineSegment(sketch, "E379.0.12", {"start": v(307.8, -511.12) * mm, "end": v(246.19, -511.12) * mm});
            skLineSegment(sketch, "E379.0.13", {"start": v(246.19, -511.12) * mm, "end": v(246.19, -535.1) * mm});
            skLineSegment(sketch, "E379.0.14", {"start": v(246.19, -535.1) * mm, "end": v(184.82, -535.1) * mm});
            skLineSegment(sketch, "E379.0.15", {"start": v(184.82, -535.1) * mm, "end": v(184.82, -511.12) * mm});
            skLineSegment(sketch, "E379.0.16", {"start": v(184.82, -511.12) * mm, "end": v(123.2, -511.12) * mm});
            skLineSegment(sketch, "E379.0.17", {"start": v(123.2, -511.12) * mm, "end": v(123.2, -535.1) * mm});
            skLineSegment(sketch, "E379.0.18", {"start": v(123.2, -535.1) * mm, "end": v(61.84, -535.1) * mm});
            skLineSegment(sketch, "E379.0.19", {"start": v(61.84, -535.1) * mm, "end": v(61.84, -511.12) * mm});
            skLineSegment(sketch, "E379.0.20", {"start": v(61.84, -511.12) * mm, "end": v(0.22, -511.12) * mm});
            skLineSegment(sketch, "E379.0.21", {"start": v(0.22, -511.12) * mm, "end": v(0.22, -535.1) * mm});
            skLineSegment(sketch, "E379.0.22", {"start": v(0.22, -535.1) * mm, "end": v(-61.15, -535.1) * mm});
            skLineSegment(sketch, "E379.0.23", {"start": v(-61.15, -535.1) * mm, "end": v(-61.15, -511.12) * mm});
            skLineSegment(sketch, "E379.0.24", {"start": v(-61.15, -511.12) * mm, "end": v(-122.76, -511.12) * mm});
            skLineSegment(sketch, "E379.0.25", {"start": v(-122.76, -511.12) * mm, "end": v(-122.76, -535.1) * mm});
            skLineSegment(sketch, "E379.0.26", {"start": v(-122.76, -535.1) * mm, "end": v(-184.13, -535.1) * mm});
            skLineSegment(sketch, "E379.0.27", {"start": v(-184.13, -535.1) * mm, "end": v(-184.13, -511.12) * mm});
            skLineSegment(sketch, "E379.0.28", {"start": v(-184.13, -511.12) * mm, "end": v(-245.74, -511.12) * mm});
            skLineSegment(sketch, "E379.0.29", {"start": v(-245.74, -511.12) * mm, "end": v(-245.74, -535.1) * mm});
            skLineSegment(sketch, "E379.0.30", {"start": v(-245.74, -535.1) * mm, "end": v(-307.11, -535.1) * mm});
            skLineSegment(sketch, "E379.0.31", {"start": v(-307.11, -535.1) * mm, "end": v(-307.11, -511.12) * mm});
            skLineSegment(sketch, "E379.0.32", {"start": v(-307.11, -511.12) * mm, "end": v(-368.73, -511.12) * mm});
            skLineSegment(sketch, "E379.0.33", {"start": v(-368.73, -511.12) * mm, "end": v(-368.73, -535.1) * mm});
            skLineSegment(sketch, "E379.0.34", {"start": v(-368.73, -535.1) * mm, "end": v(-454.2, -535.1) * mm});
            skLineSegment(sketch, "E379.0.35", {"start": v(-454.2, -535.1) * mm, "end": v(-454.2, -596.71) * mm});
            skLineSegment(sketch, "E379.0.36", {"start": v(-454.2, -596.71) * mm, "end": v(-430.22, -596.71) * mm});
            skLineSegment(sketch, "E379.0.37", {"start": v(-430.22, -596.71) * mm, "end": v(-430.22, -658.1) * mm});
            skLineSegment(sketch, "E379.0.38", {"start": v(-430.22, -658.1) * mm, "end": v(-454.2, -658.1) * mm});
            skLineSegment(sketch, "E379.0.39", {"start": v(-454.2, -658.1) * mm, "end": v(-454.2, -719.7) * mm});
            skLineSegment(sketch, "E379.0.40", {"start": v(-454.2, -719.7) * mm, "end": v(-430.22, -719.7) * mm});
            skLineSegment(sketch, "E379.0.41", {"start": v(-430.22, -719.7) * mm, "end": v(-430.22, -781.07) * mm});
            skLineSegment(sketch, "E379.0.42", {"start": v(-430.22, -781.07) * mm, "end": v(-454.2, -781.07) * mm});
            skLineSegment(sketch, "E379.0.43", {"start": v(-454.2, -781.07) * mm, "end": v(-454.2, -842.69) * mm});
            skLineSegment(sketch, "E380.bottom", {"start": v(-1687.54, 1810.9) * mm, "end": v(-773.14, 1810.9) * mm});
            skLineSegment(sketch, "E380.top", {"start": v(-1687.54, 591.7) * mm, "end": v(-773.14, 591.7) * mm});
            skLineSegment(sketch, "E380.left", {"start": v(-1687.54, 1810.9) * mm, "end": v(-1687.54, 591.7) * mm});
            skLineSegment(sketch, "E380.right", {"start": v(-773.14, 1810.9) * mm, "end": v(-773.14, 591.7) * mm});
            skSolve(sketch);
        }
        {
            var Q0;
            Q0=makeQuery(id+"F23.imprint","IMPRINT",FACE,{"disambiguationData":[TD([[makeQuery(id+"F23.imprint","IMPRINT",EDGE,{"derivedFrom":sQuery(id+"F23.wireOp",EDGE,"E377.0.0")}),1.0]])]});
            var sketch = newSketch(context, id + "F24", { "sketchPlane" : qUnion([Q0])});
            skLineSegment(sketch, "E381.0.0", {"start": v(737.6, 114.75) * mm, "end": v(737.6, 128.47) * mm});
            skLineSegment(sketch, "E381.0.1", {"start": v(737.6, 128.47) * mm, "end": v(1221.65, 128.47) * mm});
            skLineSegment(sketch, "E381.0.2", {"start": v(1221.65, 128.47) * mm, "end": v(1221.65, 177.36) * mm});
            skLineSegment(sketch, "E381.0.3", {"start": v(1221.65, 177.36) * mm, "end": v(398.15, 177.36) * mm});
            skLineSegment(sketch, "E381.0.4", {"start": v(398.15, 177.36) * mm, "end": v(398.15, 117.28) * mm});
            skLineSegment(sketch, "E381.0.5", {"start": v(398.15, 117.28) * mm, "end": v(422.13, 117.28) * mm});
            skLineSegment(sketch, "E381.0.6", {"start": v(422.13, 117.28) * mm, "end": v(422.13, 57.45) * mm});
            skLineSegment(sketch, "E381.0.7", {"start": v(422.13, 57.45) * mm, "end": v(398.15, 57.45) * mm});
            skLineSegment(sketch, "E381.0.8", {"start": v(398.15, 57.45) * mm, "end": v(398.15, -2.63) * mm});
            skLineSegment(sketch, "E381.0.9", {"start": v(398.15, -2.63) * mm, "end": v(422.13, -2.63) * mm});
            skLineSegment(sketch, "E381.0.10", {"start": v(422.13, -2.63) * mm, "end": v(422.13, -62.46) * mm});
            skLineSegment(sketch, "E381.0.11", {"start": v(422.13, -62.46) * mm, "end": v(398.15, -62.46) * mm});
            skLineSegment(sketch, "E381.0.12", {"start": v(398.15, -62.46) * mm, "end": v(398.15, -122.53) * mm});
            skLineSegment(sketch, "E381.0.13", {"start": v(398.15, -122.53) * mm, "end": v(422.13, -122.53) * mm});
            skLineSegment(sketch, "E381.0.14", {"start": v(422.13, -122.53) * mm, "end": v(422.13, -182.38) * mm});
            skLineSegment(sketch, "E381.0.15", {"start": v(422.13, -182.38) * mm, "end": v(398.15, -182.38) * mm});
            skLineSegment(sketch, "E381.0.16", {"start": v(398.15, -182.38) * mm, "end": v(398.15, -242.45) * mm});
            skLineSegment(sketch, "E381.0.17", {"start": v(398.15, -242.45) * mm, "end": v(422.13, -242.45) * mm});
            skLineSegment(sketch, "E381.0.18", {"start": v(422.13, -242.45) * mm, "end": v(422.13, -302.28) * mm});
            skLineSegment(sketch, "E381.0.19", {"start": v(422.13, -302.28) * mm, "end": v(398.15, -302.28) * mm});
            skLineSegment(sketch, "E381.0.20", {"start": v(398.15, -302.28) * mm, "end": v(398.15, -362.36) * mm});
            skLineSegment(sketch, "E381.0.21", {"start": v(398.15, -362.36) * mm, "end": v(422.13, -362.36) * mm});
            skLineSegment(sketch, "E381.0.22", {"start": v(422.13, -362.36) * mm, "end": v(422.13, -422.19) * mm});
            skLineSegment(sketch, "E381.0.23", {"start": v(422.13, -422.19) * mm, "end": v(398.15, -422.19) * mm});
            skLineSegment(sketch, "E381.0.24", {"start": v(398.15, -422.19) * mm, "end": v(398.15, -482.26) * mm});
            skLineSegment(sketch, "E381.0.25", {"start": v(398.15, -482.26) * mm, "end": v(483.63, -482.26) * mm});
            skLineSegment(sketch, "E381.0.26", {"start": v(483.63, -482.26) * mm, "end": v(483.63, -506.25) * mm});
            skLineSegment(sketch, "E381.0.27", {"start": v(483.63, -506.25) * mm, "end": v(545.24, -506.25) * mm});
            skLineSegment(sketch, "E381.0.28", {"start": v(545.24, -506.25) * mm, "end": v(545.24, -482.26) * mm});
            skLineSegment(sketch, "E381.0.29", {"start": v(545.24, -482.26) * mm, "end": v(606.6, -482.26) * mm});
            skLineSegment(sketch, "E381.0.30", {"start": v(606.6, -482.26) * mm, "end": v(606.6, -506.25) * mm});
            skLineSegment(sketch, "E381.0.31", {"start": v(606.6, -506.25) * mm, "end": v(668.22, -506.25) * mm});
            skLineSegment(sketch, "E381.0.32", {"start": v(668.22, -506.25) * mm, "end": v(668.22, -482.26) * mm});
            skLineSegment(sketch, "E381.0.33", {"start": v(668.22, -482.26) * mm, "end": v(729.59, -482.26) * mm});
            skLineSegment(sketch, "E381.0.34", {"start": v(729.59, -482.26) * mm, "end": v(729.59, -506.25) * mm});
            skLineSegment(sketch, "E381.0.35", {"start": v(729.59, -506.25) * mm, "end": v(791.2, -506.25) * mm});
            skLineSegment(sketch, "E381.0.36", {"start": v(791.2, -506.25) * mm, "end": v(791.2, -482.26) * mm});
            skLineSegment(sketch, "E381.0.37", {"start": v(791.2, -482.26) * mm, "end": v(852.58, -482.26) * mm});
            skLineSegment(sketch, "E381.0.38", {"start": v(852.58, -482.26) * mm, "end": v(852.58, -506.25) * mm});
            skLineSegment(sketch, "E381.0.39", {"start": v(852.58, -506.25) * mm, "end": v(914.19, -506.25) * mm});
            skLineSegment(sketch, "E381.0.40", {"start": v(914.19, -506.25) * mm, "end": v(914.19, -482.26) * mm});
            skLineSegment(sketch, "E381.0.41", {"start": v(914.19, -482.26) * mm, "end": v(975.56, -482.26) * mm});
            skLineSegment(sketch, "E381.0.42", {"start": v(975.56, -482.26) * mm, "end": v(975.56, -506.25) * mm});
            skLineSegment(sketch, "E381.0.43", {"start": v(975.56, -506.25) * mm, "end": v(1037.17, -506.25) * mm});
            skLineSegment(sketch, "E381.0.44", {"start": v(1037.17, -506.25) * mm, "end": v(1037.17, -482.26) * mm});
            skLineSegment(sketch, "E381.0.45", {"start": v(1037.17, -482.26) * mm, "end": v(1098.54, -482.26) * mm});
            skLineSegment(sketch, "E381.0.46", {"start": v(1098.54, -482.26) * mm, "end": v(1098.54, -506.25) * mm});
            skLineSegment(sketch, "E381.0.47", {"start": v(1098.54, -506.25) * mm, "end": v(1160.15, -506.25) * mm});
            skLineSegment(sketch, "E381.0.48", {"start": v(1160.15, -506.25) * mm, "end": v(1160.15, -482.26) * mm});
            skLineSegment(sketch, "E381.0.49", {"start": v(1160.15, -482.26) * mm, "end": v(1221.65, -482.26) * mm});
            skLineSegment(sketch, "E381.0.50", {"start": v(1221.65, -482.26) * mm, "end": v(1221.65, -298) * mm});
            skLineSegment(sketch, "E381.0.51", {"start": v(1221.65, -298) * mm, "end": v(1023.6, -298) * mm});
            skLineSegment(sketch, "E381.0.52", {"start": v(1023.6, -298) * mm, "end": v(1023.6, -284.28) * mm});
            skLineSegment(sketch, "E381.0.53", {"start": v(1023.6, -284.28) * mm, "end": v(1221.65, -284.28) * mm});
            skLineSegment(sketch, "E381.0.54", {"start": v(1221.65, -284.28) * mm, "end": v(1221.65, -215.45) * mm});
            skLineSegment(sketch, "E381.0.55", {"start": v(1221.65, -215.45) * mm, "end": v(1046.47, -215.45) * mm});
            skLineSegment(sketch, "E381.0.56", {"start": v(1046.47, -215.45) * mm, "end": v(1046.47, -201.73) * mm});
            skLineSegment(sketch, "E381.0.57", {"start": v(1046.47, -201.73) * mm, "end": v(1221.65, -201.73) * mm});
            skLineSegment(sketch, "E381.0.58", {"start": v(1221.65, -201.73) * mm, "end": v(1221.65, -132.9) * mm});
            skLineSegment(sketch, "E381.0.59", {"start": v(1221.65, -132.9) * mm, "end": v(980.43, -132.9) * mm});
            skLineSegment(sketch, "E381.0.60", {"start": v(980.43, -132.9) * mm, "end": v(980.43, -119.18) * mm});
            skLineSegment(sketch, "E381.0.61", {"start": v(980.43, -119.18) * mm, "end": v(1221.65, -119.18) * mm});
            skLineSegment(sketch, "E381.0.62", {"start": v(1221.65, -119.18) * mm, "end": v(1221.65, -50.35) * mm});
            skLineSegment(sketch, "E381.0.63", {"start": v(1221.65, -50.35) * mm, "end": v(884.67, -50.35) * mm});
            skLineSegment(sketch, "E381.0.64", {"start": v(884.67, -50.35) * mm, "end": v(884.67, -36.63) * mm});
            skLineSegment(sketch, "E381.0.65", {"start": v(884.67, -36.63) * mm, "end": v(1221.65, -36.63) * mm});
            skLineSegment(sketch, "E381.0.66", {"start": v(1221.65, -36.63) * mm, "end": v(1221.65, 32.2) * mm});
            skLineSegment(sketch, "E381.0.67", {"start": v(1221.65, 32.2) * mm, "end": v(809.48, 32.2) * mm});
            skLineSegment(sketch, "E381.0.68", {"start": v(809.48, 32.2) * mm, "end": v(809.48, 45.92) * mm});
            skLineSegment(sketch, "E381.0.69", {"start": v(809.48, 45.92) * mm, "end": v(1221.65, 45.92) * mm});
            skLineSegment(sketch, "E381.0.70", {"start": v(1221.65, 45.92) * mm, "end": v(1221.65, 114.75) * mm});
            skLineSegment(sketch, "E381.0.71", {"start": v(1221.65, 114.75) * mm, "end": v(737.6, 114.75) * mm});
            skLineSegment(sketch, "E382", {"start": v(422.13, -2.63) * mm, "end": v(1221.65, -2.63) * mm});
            skSolve(sketch);
        }
        {
            var Q0;
            Q0=makeQuery(id+"F24.imprint","IMPRINT",FACE,{"disambiguationData":[TD([[makeQuery(id+"F24.imprint","IMPRINT",EDGE,{"derivedFrom":sQuery(id+"F24.wireOp",EDGE,"E381.0.0")}),1.0]])]});
            extrude(context, id + "F25", {"entities" : qUnion([Q0]), "operationType" : NewBodyOperationType.REMOVE, "oppositeDirection" : true, "depth" : 25.4 * mm});
        }
        {
            var Q0;
            Q0=makeQuery(id+"F23.imprint","IMPRINT",FACE,{"disambiguationData":[TD([[makeQuery(id+"F23.imprint","IMPRINT",EDGE,{"derivedFrom":sQuery(id+"F23.wireOp",EDGE,"E378.0.0")}),1.0]])]});
            var sketch = newSketch(context, id + "F26", { "sketchPlane" : qUnion([Q0])});
            skLineSegment(sketch, "E383.0.0", {"start": v(-459.08, 117.28) * mm, "end": v(-459.08, 177.36) * mm});
            skLineSegment(sketch, "E383.0.1", {"start": v(-459.08, 177.36) * mm, "end": v(-1282.57, 177.36) * mm});
            skLineSegment(sketch, "E383.0.2", {"start": v(-1282.57, 177.36) * mm, "end": v(-1282.57, 128.47) * mm});
            skLineSegment(sketch, "E383.0.3", {"start": v(-1282.57, 128.47) * mm, "end": v(-798.52, 128.47) * mm});
            skLineSegment(sketch, "E383.0.4", {"start": v(-798.52, 128.47) * mm, "end": v(-798.52, 114.75) * mm});
            skLineSegment(sketch, "E383.0.5", {"start": v(-798.52, 114.75) * mm, "end": v(-1282.57, 114.75) * mm});
            skLineSegment(sketch, "E383.0.6", {"start": v(-1282.57, 114.75) * mm, "end": v(-1282.57, 45.92) * mm});
            skLineSegment(sketch, "E383.0.7", {"start": v(-1282.57, 45.92) * mm, "end": v(-870.4, 45.92) * mm});
            skLineSegment(sketch, "E383.0.8", {"start": v(-870.4, 45.92) * mm, "end": v(-870.4, 32.2) * mm});
            skLineSegment(sketch, "E383.0.9", {"start": v(-870.4, 32.2) * mm, "end": v(-1282.57, 32.2) * mm});
            skLineSegment(sketch, "E383.0.10", {"start": v(-1282.57, 32.2) * mm, "end": v(-1282.57, -36.63) * mm});
            skLineSegment(sketch, "E383.0.11", {"start": v(-1282.57, -36.63) * mm, "end": v(-945.59, -36.63) * mm});
            skLineSegment(sketch, "E383.0.12", {"start": v(-945.59, -36.63) * mm, "end": v(-945.59, -50.35) * mm});
            skLineSegment(sketch, "E383.0.13", {"start": v(-945.59, -50.35) * mm, "end": v(-1282.57, -50.35) * mm});
            skLineSegment(sketch, "E383.0.14", {"start": v(-1282.57, -50.35) * mm, "end": v(-1282.57, -119.18) * mm});
            skLineSegment(sketch, "E383.0.15", {"start": v(-1282.57, -119.18) * mm, "end": v(-1041.35, -119.18) * mm});
            skLineSegment(sketch, "E383.0.16", {"start": v(-1041.35, -119.18) * mm, "end": v(-1041.35, -132.9) * mm});
            skLineSegment(sketch, "E383.0.17", {"start": v(-1041.35, -132.9) * mm, "end": v(-1282.57, -132.9) * mm});
            skLineSegment(sketch, "E383.0.18", {"start": v(-1282.57, -132.9) * mm, "end": v(-1282.57, -201.73) * mm});
            skLineSegment(sketch, "E383.0.19", {"start": v(-1282.57, -201.73) * mm, "end": v(-1107.39, -201.73) * mm});
            skLineSegment(sketch, "E383.0.20", {"start": v(-1107.39, -201.73) * mm, "end": v(-1107.39, -215.45) * mm});
            skLineSegment(sketch, "E383.0.21", {"start": v(-1107.39, -215.45) * mm, "end": v(-1282.57, -215.45) * mm});
            skLineSegment(sketch, "E383.0.22", {"start": v(-1282.57, -215.45) * mm, "end": v(-1282.57, -284.28) * mm});
            skLineSegment(sketch, "E383.0.23", {"start": v(-1282.57, -284.28) * mm, "end": v(-1084.53, -284.28) * mm});
            skLineSegment(sketch, "E383.0.24", {"start": v(-1084.53, -284.28) * mm, "end": v(-1084.53, -298) * mm});
            skLineSegment(sketch, "E383.0.25", {"start": v(-1084.53, -298) * mm, "end": v(-1282.57, -298) * mm});
            skLineSegment(sketch, "E383.0.26", {"start": v(-1282.57, -298) * mm, "end": v(-1282.57, -482.26) * mm});
            skLineSegment(sketch, "E383.0.27", {"start": v(-1282.57, -482.26) * mm, "end": v(-1221.08, -482.26) * mm});
            skLineSegment(sketch, "E383.0.28", {"start": v(-1221.08, -482.26) * mm, "end": v(-1221.08, -506.25) * mm});
            skLineSegment(sketch, "E383.0.29", {"start": v(-1221.08, -506.25) * mm, "end": v(-1159.47, -506.25) * mm});
            skLineSegment(sketch, "E383.0.30", {"start": v(-1159.47, -506.25) * mm, "end": v(-1159.47, -482.26) * mm});
            skLineSegment(sketch, "E383.0.31", {"start": v(-1159.47, -482.26) * mm, "end": v(-1098.1, -482.26) * mm});
            skLineSegment(sketch, "E383.0.32", {"start": v(-1098.1, -482.26) * mm, "end": v(-1098.1, -506.25) * mm});
            skLineSegment(sketch, "E383.0.33", {"start": v(-1098.1, -506.25) * mm, "end": v(-1036.48, -506.25) * mm});
            skLineSegment(sketch, "E383.0.34", {"start": v(-1036.48, -506.25) * mm, "end": v(-1036.48, -482.26) * mm});
            skLineSegment(sketch, "E383.0.35", {"start": v(-1036.48, -482.26) * mm, "end": v(-975.11, -482.26) * mm});
            skLineSegment(sketch, "E383.0.36", {"start": v(-975.11, -482.26) * mm, "end": v(-975.11, -506.25) * mm});
            skLineSegment(sketch, "E383.0.37", {"start": v(-975.11, -506.25) * mm, "end": v(-913.5, -506.25) * mm});
            skLineSegment(sketch, "E383.0.38", {"start": v(-913.5, -506.25) * mm, "end": v(-913.5, -482.26) * mm});
            skLineSegment(sketch, "E383.0.39", {"start": v(-913.5, -482.26) * mm, "end": v(-852.13, -482.26) * mm});
            skLineSegment(sketch, "E383.0.40", {"start": v(-852.13, -482.26) * mm, "end": v(-852.13, -506.25) * mm});
            skLineSegment(sketch, "E383.0.41", {"start": v(-852.13, -506.25) * mm, "end": v(-790.52, -506.25) * mm});
            skLineSegment(sketch, "E383.0.42", {"start": v(-790.52, -506.25) * mm, "end": v(-790.52, -482.26) * mm});
            skLineSegment(sketch, "E383.0.43", {"start": v(-790.52, -482.26) * mm, "end": v(-729.15, -482.26) * mm});
            skLineSegment(sketch, "E383.0.44", {"start": v(-729.15, -482.26) * mm, "end": v(-729.15, -506.25) * mm});
            skLineSegment(sketch, "E383.0.45", {"start": v(-729.15, -506.25) * mm, "end": v(-667.53, -506.25) * mm});
            skLineSegment(sketch, "E383.0.46", {"start": v(-667.53, -506.25) * mm, "end": v(-667.53, -482.26) * mm});
            skLineSegment(sketch, "E383.0.47", {"start": v(-667.53, -482.26) * mm, "end": v(-606.17, -482.26) * mm});
            skLineSegment(sketch, "E383.0.48", {"start": v(-606.17, -482.26) * mm, "end": v(-606.17, -506.25) * mm});
            skLineSegment(sketch, "E383.0.49", {"start": v(-606.17, -506.25) * mm, "end": v(-544.55, -506.25) * mm});
            skLineSegment(sketch, "E383.0.50", {"start": v(-544.55, -506.25) * mm, "end": v(-544.55, -482.26) * mm});
            skLineSegment(sketch, "E383.0.51", {"start": v(-544.55, -482.26) * mm, "end": v(-459.08, -482.26) * mm});
            skLineSegment(sketch, "E383.0.52", {"start": v(-459.08, -482.26) * mm, "end": v(-459.08, -422.19) * mm});
            skLineSegment(sketch, "E383.0.53", {"start": v(-459.08, -422.19) * mm, "end": v(-483.06, -422.19) * mm});
            skLineSegment(sketch, "E383.0.54", {"start": v(-483.06, -422.19) * mm, "end": v(-483.06, -362.36) * mm});
            skLineSegment(sketch, "E383.0.55", {"start": v(-483.06, -362.36) * mm, "end": v(-459.08, -362.36) * mm});
            skLineSegment(sketch, "E383.0.56", {"start": v(-459.08, -362.36) * mm, "end": v(-459.08, -302.28) * mm});
            skLineSegment(sketch, "E383.0.57", {"start": v(-459.08, -302.28) * mm, "end": v(-483.06, -302.28) * mm});
            skLineSegment(sketch, "E383.0.58", {"start": v(-483.06, -302.28) * mm, "end": v(-483.06, -242.45) * mm});
            skLineSegment(sketch, "E383.0.59", {"start": v(-483.06, -242.45) * mm, "end": v(-459.08, -242.45) * mm});
            skLineSegment(sketch, "E383.0.60", {"start": v(-459.08, -242.45) * mm, "end": v(-459.08, -182.38) * mm});
            skLineSegment(sketch, "E383.0.61", {"start": v(-459.08, -182.38) * mm, "end": v(-483.06, -182.38) * mm});
            skLineSegment(sketch, "E383.0.62", {"start": v(-483.06, -182.38) * mm, "end": v(-483.06, -122.53) * mm});
            skLineSegment(sketch, "E383.0.63", {"start": v(-483.06, -122.53) * mm, "end": v(-459.08, -122.53) * mm});
            skLineSegment(sketch, "E383.0.64", {"start": v(-459.08, -122.53) * mm, "end": v(-459.08, -62.46) * mm});
            skLineSegment(sketch, "E383.0.65", {"start": v(-459.08, -62.46) * mm, "end": v(-483.06, -62.46) * mm});
            skLineSegment(sketch, "E383.0.66", {"start": v(-483.06, -62.46) * mm, "end": v(-483.06, -2.63) * mm});
            skLineSegment(sketch, "E383.0.67", {"start": v(-483.06, -2.63) * mm, "end": v(-459.08, -2.63) * mm});
            skLineSegment(sketch, "E383.0.68", {"start": v(-459.08, -2.63) * mm, "end": v(-459.08, 57.45) * mm});
            skLineSegment(sketch, "E383.0.69", {"start": v(-459.08, 57.45) * mm, "end": v(-483.06, 57.45) * mm});
            skLineSegment(sketch, "E383.0.70", {"start": v(-483.06, 57.45) * mm, "end": v(-483.06, 117.28) * mm});
            skLineSegment(sketch, "E383.0.71", {"start": v(-483.06, 117.28) * mm, "end": v(-459.08, 117.28) * mm});
            skLineSegment(sketch, "E384", {"start": v(-483.06, -2.63) * mm, "end": v(-1282.57, -2.63) * mm});
            skSolve(sketch);
        }
        {
            var Q0;
            Q0=makeQuery(id+"F26.imprint","IMPRINT",FACE,{"disambiguationData":[TD([[makeQuery(id+"F26.imprint","IMPRINT",EDGE,{"derivedFrom":sQuery(id+"F26.wireOp",EDGE,"E383.0.0")}),1.0]])]});
            extrude(context, id + "F27", {"entities" : qUnion([Q0]), "operationType" : NewBodyOperationType.REMOVE, "oppositeDirection" : true, "depth" : 25.4 * mm});
        }
        {
            var Q0;
            Q0=makeQuery(id+"F22.boolean.opBoolean","MERGE",FACE,{"derivedFrom":[makeQuery(id+"F1.opExtrude","CAP_FACE",FACE,{"disambiguationData":[OSD([sQuery(id+"F0.wireOp",EDGE,"E77"),sQuery(id+"F0.wireOp",EDGE,"E78"),sQuery(id+"F0.wireOp",EDGE,"E79"),sQuery(id+"F0.wireOp",EDGE,"E80"),sQuery(id+"F0.wireOp",EDGE,"E81"),sQuery(id+"F0.wireOp",EDGE,"E82"),sQuery(id+"F0.wireOp",EDGE,"E83"),sQuery(id+"F0.wireOp",EDGE,"E84"),sQuery(id+"F0.wireOp",EDGE,"E85"),sQuery(id+"F0.wireOp",EDGE,"E86"),sQuery(id+"F0.wireOp",EDGE,"E87"),sQuery(id+"F0.wireOp",EDGE,"E88"),sQuery(id+"F0.wireOp",EDGE,"E89"),sQuery(id+"F0.wireOp",EDGE,"E90"),sQuery(id+"F0.wireOp",EDGE,"E91"),sQuery(id+"F0.wireOp",EDGE,"E92"),sQuery(id+"F0.wireOp",EDGE,"E93"),sQuery(id+"F0.wireOp",EDGE,"E94"),sQuery(id+"F0.wireOp",EDGE,"E95"),sQuery(id+"F0.wireOp",EDGE,"E96"),sQuery(id+"F0.wireOp",EDGE,"E97"),sQuery(id+"F0.wireOp",EDGE,"E98"),sQuery(id+"F0.wireOp",EDGE,"E99"),sQuery(id+"F0.wireOp",EDGE,"E100"),sQuery(id+"F0.wireOp",EDGE,"E102"),sQuery(id+"F0.wireOp",EDGE,"E103"),sQuery(id+"F0.wireOp",EDGE,"E104"),sQuery(id+"F0.wireOp",EDGE,"E105"),sQuery(id+"F0.wireOp",EDGE,"E106"),sQuery(id+"F0.wireOp",EDGE,"E107"),sQuery(id+"F0.wireOp",EDGE,"E108"),sQuery(id+"F0.wireOp",EDGE,"E109"),sQuery(id+"F0.wireOp",EDGE,"E110"),sQuery(id+"F0.wireOp",EDGE,"E111"),sQuery(id+"F0.wireOp",EDGE,"E112"),sQuery(id+"F0.wireOp",EDGE,"E113"),sQuery(id+"F0.wireOp",EDGE,"E114"),sQuery(id+"F0.wireOp",EDGE,"E115"),sQuery(id+"F0.wireOp",EDGE,"E116"),sQuery(id+"F0.wireOp",EDGE,"E117"),sQuery(id+"F0.wireOp",EDGE,"E118"),sQuery(id+"F0.wireOp",EDGE,"E119"),sQuery(id+"F0.wireOp",EDGE,"E120"),sQuery(id+"F0.wireOp",EDGE,"E121"),sQuery(id+"F0.wireOp",EDGE,"E122"),sQuery(id+"F0.wireOp",EDGE,"E123"),sQuery(id+"F0.wireOp",EDGE,"E124"),sQuery(id+"F0.wireOp",EDGE,"E125"),sQuery(id+"F0.wireOp",EDGE,"E126"),sQuery(id+"F0.wireOp",EDGE,"E127"),sQuery(id+"F0.wireOp",EDGE,"E128"),sQuery(id+"F0.wireOp",EDGE,"E129"),sQuery(id+"F0.wireOp",EDGE,"E130"),sQuery(id+"F0.wireOp",EDGE,"E131"),sQuery(id+"F0.wireOp",EDGE,"E132"),sQuery(id+"F0.wireOp",EDGE,"E133"),sQuery(id+"F0.wireOp",EDGE,"E134"),sQuery(id+"F0.wireOp",EDGE,"E135"),sQuery(id+"F0.wireOp",EDGE,"E136"),sQuery(id+"F0.wireOp",EDGE,"E137"),sQuery(id+"F0.wireOp",EDGE,"E138"),sQuery(id+"F0.wireOp",EDGE,"E139"),sQuery(id+"F0.wireOp",EDGE,"E140"),sQuery(id+"F0.wireOp",EDGE,"E141"),sQuery(id+"F0.wireOp",EDGE,"E142"),sQuery(id+"F0.wireOp",EDGE,"E143"),sQuery(id+"F0.wireOp",EDGE,"E144"),sQuery(id+"F0.wireOp",EDGE,"E145"),sQuery(id+"F0.wireOp",EDGE,"E146"),sQuery(id+"F0.wireOp",EDGE,"E147"),sQuery(id+"F0.wireOp",EDGE,"E148"),sQuery(id+"F0.wireOp",EDGE,"E149"),sQuery(id+"F0.wireOp",EDGE,"E150"),sQuery(id+"F0.wireOp",EDGE,"E151"),sQuery(id+"F0.wireOp",EDGE,"E152"),sQuery(id+"F0.wireOp",EDGE,"E153"),sQuery(id+"F0.wireOp",EDGE,"E154"),sQuery(id+"F0.wireOp",EDGE,"E155"),sQuery(id+"F0.wireOp",EDGE,"E156"),sQuery(id+"F0.wireOp",EDGE,"E157"),sQuery(id+"F0.wireOp",EDGE,"E158"),sQuery(id+"F0.wireOp",EDGE,"E159"),sQuery(id+"F0.wireOp",EDGE,"E160"),sQuery(id+"F0.wireOp",EDGE,"E161"),sQuery(id+"F0.wireOp",EDGE,"E162"),sQuery(id+"F0.wireOp",EDGE,"E163"),sQuery(id+"F0.wireOp",EDGE,"E164"),sQuery(id+"F0.wireOp",EDGE,"E165"),sQuery(id+"F0.wireOp",EDGE,"E280"),sQuery(id+"F0.wireOp",EDGE,"E286"),sQuery(id+"F0.wireOp",EDGE,"E287")])],"isStart":false}),makeQuery(id+"F22.opExtrude","CAP_FACE",FACE,{"disambiguationData":[OSD([sQuery(id+"F21.wireOp",EDGE,"E372"),sQuery(id+"F21.wireOp",EDGE,"E373"),sQuery(id+"F21.wireOp",EDGE,"E374.0"),sQuery(id+"F21.wireOp",EDGE,"E375.0")])],"isStart":true})]});
            var sketch = newSketch(context, id + "F28", { "sketchPlane" : qUnion([Q0])});
            skLineSegment(sketch, "E385", {"start": v(-430.22, -2.5) * mm, "end": v(369.29, -2.5) * mm});
            skLineSegment(sketch, "E386.0.0", {"start": v(369.29, 177.24) * mm, "end": v(-430.22, 177.24) * mm});
            skLineSegment(sketch, "E386.0.1", {"start": v(-430.22, 177.24) * mm, "end": v(-430.22, 117.4) * mm});
            skLineSegment(sketch, "E386.0.2", {"start": v(-430.22, 117.4) * mm, "end": v(-454.2, 117.4) * mm});
            skLineSegment(sketch, "E386.0.3", {"start": v(-454.2, 117.4) * mm, "end": v(-454.2, 57.32) * mm});
            skLineSegment(sketch, "E386.0.4", {"start": v(-454.2, 57.32) * mm, "end": v(-430.22, 57.32) * mm});
            skLineSegment(sketch, "E386.0.5", {"start": v(-430.22, 57.32) * mm, "end": v(-430.22, -2.5) * mm});
            skLineSegment(sketch, "E386.0.6", {"start": v(-430.22, -2.5) * mm, "end": v(-454.2, -2.5) * mm});
            skLineSegment(sketch, "E386.0.7", {"start": v(-454.2, -2.5) * mm, "end": v(-454.2, -62.59) * mm});
            skLineSegment(sketch, "E386.0.8", {"start": v(-454.2, -62.59) * mm, "end": v(-430.22, -62.59) * mm});
            skLineSegment(sketch, "E386.0.9", {"start": v(-430.22, -62.59) * mm, "end": v(-430.22, -122.41) * mm});
            skLineSegment(sketch, "E386.0.10", {"start": v(-430.22, -122.41) * mm, "end": v(-454.2, -122.41) * mm});
            skLineSegment(sketch, "E386.0.11", {"start": v(-454.2, -122.41) * mm, "end": v(-454.2, -182.5) * mm});
            skLineSegment(sketch, "E386.0.12", {"start": v(-454.2, -182.5) * mm, "end": v(-430.22, -182.5) * mm});
            skLineSegment(sketch, "E386.0.13", {"start": v(-430.22, -182.5) * mm, "end": v(-430.22, -242.33) * mm});
            skLineSegment(sketch, "E386.0.14", {"start": v(-430.22, -242.33) * mm, "end": v(-454.2, -242.33) * mm});
            skLineSegment(sketch, "E386.0.15", {"start": v(-454.2, -242.33) * mm, "end": v(-454.2, -302.4) * mm});
            skLineSegment(sketch, "E386.0.16", {"start": v(-454.2, -302.4) * mm, "end": v(-430.22, -302.4) * mm});
            skLineSegment(sketch, "E386.0.17", {"start": v(-430.22, -302.4) * mm, "end": v(-430.22, -362.23) * mm});
            skLineSegment(sketch, "E386.0.18", {"start": v(-430.22, -362.23) * mm, "end": v(-454.2, -362.23) * mm});
            skLineSegment(sketch, "E386.0.19", {"start": v(-454.2, -362.23) * mm, "end": v(-454.2, -422.3) * mm});
            skLineSegment(sketch, "E386.0.20", {"start": v(-454.2, -422.3) * mm, "end": v(-430.22, -422.3) * mm});
            skLineSegment(sketch, "E386.0.21", {"start": v(-430.22, -422.3) * mm, "end": v(-430.22, -482.15) * mm});
            skLineSegment(sketch, "E386.0.22", {"start": v(-430.22, -482.15) * mm, "end": v(-454.2, -482.15) * mm});
            skLineSegment(sketch, "E386.0.23", {"start": v(-454.2, -482.15) * mm, "end": v(-454.2, -506.25) * mm});
            skLineSegment(sketch, "E386.0.24", {"start": v(-454.2, -506.25) * mm, "end": v(-368.61, -506.25) * mm});
            skLineSegment(sketch, "E386.0.25", {"start": v(-368.61, -506.25) * mm, "end": v(-368.61, -482.26) * mm});
            skLineSegment(sketch, "E386.0.26", {"start": v(-368.61, -482.26) * mm, "end": v(-307.24, -482.26) * mm});
            skLineSegment(sketch, "E386.0.27", {"start": v(-307.24, -482.26) * mm, "end": v(-307.24, -506.25) * mm});
            skLineSegment(sketch, "E386.0.28", {"start": v(-307.24, -506.25) * mm, "end": v(-245.62, -506.25) * mm});
            skLineSegment(sketch, "E386.0.29", {"start": v(-245.62, -506.25) * mm, "end": v(-245.62, -482.26) * mm});
            skLineSegment(sketch, "E386.0.30", {"start": v(-245.62, -482.26) * mm, "end": v(-184.26, -482.26) * mm});
            skLineSegment(sketch, "E386.0.31", {"start": v(-184.26, -482.26) * mm, "end": v(-184.26, -506.25) * mm});
            skLineSegment(sketch, "E386.0.32", {"start": v(-184.26, -506.25) * mm, "end": v(-122.64, -506.25) * mm});
            skLineSegment(sketch, "E386.0.33", {"start": v(-122.64, -506.25) * mm, "end": v(-122.64, -482.26) * mm});
            skLineSegment(sketch, "E386.0.34", {"start": v(-122.64, -482.26) * mm, "end": v(-61.27, -482.26) * mm});
            skLineSegment(sketch, "E386.0.35", {"start": v(-61.27, -482.26) * mm, "end": v(-61.27, -506.25) * mm});
            skLineSegment(sketch, "E386.0.36", {"start": v(-61.27, -506.25) * mm, "end": v(0.34, -506.25) * mm});
            skLineSegment(sketch, "E386.0.37", {"start": v(0.34, -506.25) * mm, "end": v(0.34, -482.26) * mm});
            skLineSegment(sketch, "E386.0.38", {"start": v(0.34, -482.26) * mm, "end": v(61.71, -482.26) * mm});
            skLineSegment(sketch, "E386.0.39", {"start": v(61.71, -482.26) * mm, "end": v(61.71, -506.25) * mm});
            skLineSegment(sketch, "E386.0.40", {"start": v(61.71, -506.25) * mm, "end": v(123.33, -506.25) * mm});
            skLineSegment(sketch, "E386.0.41", {"start": v(123.33, -506.25) * mm, "end": v(123.33, -482.26) * mm});
            skLineSegment(sketch, "E386.0.42", {"start": v(123.33, -482.26) * mm, "end": v(184.7, -482.26) * mm});
            skLineSegment(sketch, "E386.0.43", {"start": v(184.7, -482.26) * mm, "end": v(184.7, -506.25) * mm});
            skLineSegment(sketch, "E386.0.44", {"start": v(184.7, -506.25) * mm, "end": v(246.3, -506.25) * mm});
            skLineSegment(sketch, "E386.0.45", {"start": v(246.3, -506.25) * mm, "end": v(246.3, -482.26) * mm});
            skLineSegment(sketch, "E386.0.46", {"start": v(246.3, -482.26) * mm, "end": v(307.69, -482.26) * mm});
            skLineSegment(sketch, "E386.0.47", {"start": v(307.69, -482.26) * mm, "end": v(307.69, -506.25) * mm});
            skLineSegment(sketch, "E386.0.48", {"start": v(307.69, -506.25) * mm, "end": v(393.28, -506.25) * mm});
            skLineSegment(sketch, "E386.0.49", {"start": v(393.28, -506.25) * mm, "end": v(393.28, -482.15) * mm});
            skLineSegment(sketch, "E386.0.50", {"start": v(393.28, -482.15) * mm, "end": v(369.29, -482.15) * mm});
            skLineSegment(sketch, "E386.0.51", {"start": v(369.29, -482.15) * mm, "end": v(369.29, -422.3) * mm});
            skLineSegment(sketch, "E386.0.52", {"start": v(369.29, -422.3) * mm, "end": v(393.28, -422.3) * mm});
            skLineSegment(sketch, "E386.0.53", {"start": v(393.28, -422.3) * mm, "end": v(393.28, -362.23) * mm});
            skLineSegment(sketch, "E386.0.54", {"start": v(393.28, -362.23) * mm, "end": v(369.29, -362.23) * mm});
            skLineSegment(sketch, "E386.0.55", {"start": v(369.29, -362.23) * mm, "end": v(369.29, -302.4) * mm});
            skLineSegment(sketch, "E386.0.56", {"start": v(369.29, -302.4) * mm, "end": v(393.28, -302.4) * mm});
            skLineSegment(sketch, "E386.0.57", {"start": v(393.28, -302.4) * mm, "end": v(393.28, -242.33) * mm});
            skLineSegment(sketch, "E386.0.58", {"start": v(393.28, -242.33) * mm, "end": v(369.29, -242.33) * mm});
            skLineSegment(sketch, "E386.0.59", {"start": v(369.29, -242.33) * mm, "end": v(369.29, -182.5) * mm});
            skLineSegment(sketch, "E386.0.60", {"start": v(369.29, -182.5) * mm, "end": v(393.28, -182.5) * mm});
            skLineSegment(sketch, "E386.0.61", {"start": v(393.28, -182.5) * mm, "end": v(393.28, -122.41) * mm});
            skLineSegment(sketch, "E386.0.62", {"start": v(393.28, -122.41) * mm, "end": v(369.29, -122.41) * mm});
            skLineSegment(sketch, "E386.0.63", {"start": v(369.29, -122.41) * mm, "end": v(369.29, -62.59) * mm});
            skLineSegment(sketch, "E386.0.64", {"start": v(369.29, -62.59) * mm, "end": v(393.28, -62.59) * mm});
            skLineSegment(sketch, "E386.0.65", {"start": v(393.28, -62.59) * mm, "end": v(393.28, -2.5) * mm});
            skLineSegment(sketch, "E386.0.66", {"start": v(393.28, -2.5) * mm, "end": v(369.29, -2.5) * mm});
            skLineSegment(sketch, "E386.0.67", {"start": v(369.29, -2.5) * mm, "end": v(369.29, 57.32) * mm});
            skLineSegment(sketch, "E386.0.68", {"start": v(369.29, 57.32) * mm, "end": v(393.28, 57.32) * mm});
            skLineSegment(sketch, "E386.0.69", {"start": v(393.28, 57.32) * mm, "end": v(393.28, 117.4) * mm});
            skLineSegment(sketch, "E386.0.70", {"start": v(393.28, 117.4) * mm, "end": v(369.29, 117.4) * mm});
            skLineSegment(sketch, "E386.0.71", {"start": v(369.29, 117.4) * mm, "end": v(369.29, 177.24) * mm});
            skSolve(sketch);
        }
        {
            var Q0;
            Q0=makeQuery(id+"F28.imprint","IMPRINT",FACE,{"disambiguationData":[TD([[makeQuery(id+"F28.imprint","IMPRINT",EDGE,{"derivedFrom":sQuery(id+"F28.wireOp",EDGE,"E386.0.0")}),-1.0]])]});
            extrude(context, id + "F29", {"entities" : qUnion([Q0]), "operationType" : NewBodyOperationType.REMOVE, "oppositeDirection" : true, "depth" : 25.4 * mm});
        }
        {
            var Q0;
            Q0=makeQuery(id+"F22.boolean.opBoolean","MERGE",FACE,{"derivedFrom":[makeQuery(id+"F1.opExtrude","CAP_FACE",FACE,{"disambiguationData":[OSD([sQuery(id+"F0.wireOp",EDGE,"E77"),sQuery(id+"F0.wireOp",EDGE,"E78"),sQuery(id+"F0.wireOp",EDGE,"E79"),sQuery(id+"F0.wireOp",EDGE,"E80"),sQuery(id+"F0.wireOp",EDGE,"E81"),sQuery(id+"F0.wireOp",EDGE,"E82"),sQuery(id+"F0.wireOp",EDGE,"E83"),sQuery(id+"F0.wireOp",EDGE,"E84"),sQuery(id+"F0.wireOp",EDGE,"E85"),sQuery(id+"F0.wireOp",EDGE,"E86"),sQuery(id+"F0.wireOp",EDGE,"E87"),sQuery(id+"F0.wireOp",EDGE,"E88"),sQuery(id+"F0.wireOp",EDGE,"E89"),sQuery(id+"F0.wireOp",EDGE,"E90"),sQuery(id+"F0.wireOp",EDGE,"E91"),sQuery(id+"F0.wireOp",EDGE,"E92"),sQuery(id+"F0.wireOp",EDGE,"E93"),sQuery(id+"F0.wireOp",EDGE,"E94"),sQuery(id+"F0.wireOp",EDGE,"E95"),sQuery(id+"F0.wireOp",EDGE,"E96"),sQuery(id+"F0.wireOp",EDGE,"E97"),sQuery(id+"F0.wireOp",EDGE,"E98"),sQuery(id+"F0.wireOp",EDGE,"E99"),sQuery(id+"F0.wireOp",EDGE,"E100"),sQuery(id+"F0.wireOp",EDGE,"E102"),sQuery(id+"F0.wireOp",EDGE,"E103"),sQuery(id+"F0.wireOp",EDGE,"E104"),sQuery(id+"F0.wireOp",EDGE,"E105"),sQuery(id+"F0.wireOp",EDGE,"E106"),sQuery(id+"F0.wireOp",EDGE,"E107"),sQuery(id+"F0.wireOp",EDGE,"E108"),sQuery(id+"F0.wireOp",EDGE,"E109"),sQuery(id+"F0.wireOp",EDGE,"E110"),sQuery(id+"F0.wireOp",EDGE,"E111"),sQuery(id+"F0.wireOp",EDGE,"E112"),sQuery(id+"F0.wireOp",EDGE,"E113"),sQuery(id+"F0.wireOp",EDGE,"E114"),sQuery(id+"F0.wireOp",EDGE,"E115"),sQuery(id+"F0.wireOp",EDGE,"E116"),sQuery(id+"F0.wireOp",EDGE,"E117"),sQuery(id+"F0.wireOp",EDGE,"E118"),sQuery(id+"F0.wireOp",EDGE,"E119"),sQuery(id+"F0.wireOp",EDGE,"E120"),sQuery(id+"F0.wireOp",EDGE,"E121"),sQuery(id+"F0.wireOp",EDGE,"E122"),sQuery(id+"F0.wireOp",EDGE,"E123"),sQuery(id+"F0.wireOp",EDGE,"E124"),sQuery(id+"F0.wireOp",EDGE,"E125"),sQuery(id+"F0.wireOp",EDGE,"E126"),sQuery(id+"F0.wireOp",EDGE,"E127"),sQuery(id+"F0.wireOp",EDGE,"E128"),sQuery(id+"F0.wireOp",EDGE,"E129"),sQuery(id+"F0.wireOp",EDGE,"E130"),sQuery(id+"F0.wireOp",EDGE,"E131"),sQuery(id+"F0.wireOp",EDGE,"E132"),sQuery(id+"F0.wireOp",EDGE,"E133"),sQuery(id+"F0.wireOp",EDGE,"E134"),sQuery(id+"F0.wireOp",EDGE,"E135"),sQuery(id+"F0.wireOp",EDGE,"E136"),sQuery(id+"F0.wireOp",EDGE,"E137"),sQuery(id+"F0.wireOp",EDGE,"E138"),sQuery(id+"F0.wireOp",EDGE,"E139"),sQuery(id+"F0.wireOp",EDGE,"E140"),sQuery(id+"F0.wireOp",EDGE,"E141"),sQuery(id+"F0.wireOp",EDGE,"E142"),sQuery(id+"F0.wireOp",EDGE,"E143"),sQuery(id+"F0.wireOp",EDGE,"E144"),sQuery(id+"F0.wireOp",EDGE,"E145"),sQuery(id+"F0.wireOp",EDGE,"E146"),sQuery(id+"F0.wireOp",EDGE,"E147"),sQuery(id+"F0.wireOp",EDGE,"E148"),sQuery(id+"F0.wireOp",EDGE,"E149"),sQuery(id+"F0.wireOp",EDGE,"E150"),sQuery(id+"F0.wireOp",EDGE,"E151"),sQuery(id+"F0.wireOp",EDGE,"E152"),sQuery(id+"F0.wireOp",EDGE,"E153"),sQuery(id+"F0.wireOp",EDGE,"E154"),sQuery(id+"F0.wireOp",EDGE,"E155"),sQuery(id+"F0.wireOp",EDGE,"E156"),sQuery(id+"F0.wireOp",EDGE,"E157"),sQuery(id+"F0.wireOp",EDGE,"E158"),sQuery(id+"F0.wireOp",EDGE,"E159"),sQuery(id+"F0.wireOp",EDGE,"E160"),sQuery(id+"F0.wireOp",EDGE,"E161"),sQuery(id+"F0.wireOp",EDGE,"E162"),sQuery(id+"F0.wireOp",EDGE,"E163"),sQuery(id+"F0.wireOp",EDGE,"E164"),sQuery(id+"F0.wireOp",EDGE,"E165"),sQuery(id+"F0.wireOp",EDGE,"E280"),sQuery(id+"F0.wireOp",EDGE,"E286"),sQuery(id+"F0.wireOp",EDGE,"E287")])],"isStart":false}),makeQuery(id+"F22.opExtrude","CAP_FACE",FACE,{"disambiguationData":[OSD([sQuery(id+"F21.wireOp",EDGE,"E372"),sQuery(id+"F21.wireOp",EDGE,"E373"),sQuery(id+"F21.wireOp",EDGE,"E374.0"),sQuery(id+"F21.wireOp",EDGE,"E375.0")])],"isStart":true})]});
            var sketch = newSketch(context, id + "F30", { "sketchPlane" : qUnion([Q0])});
            skLineSegment(sketch, "E387.bottom", {"start": v(-404.82, -2.5) * mm, "end": v(343.89, -2.5) * mm});
            skLineSegment(sketch, "E387.top", {"start": v(-404.82, -62.59) * mm, "end": v(343.89, -62.59) * mm});
            skLineSegment(sketch, "E387.left", {"start": v(-404.82, -2.5) * mm, "end": v(-404.82, -62.59) * mm});
            skLineSegment(sketch, "E387.right", {"start": v(343.89, -2.5) * mm, "end": v(343.89, -62.59) * mm});
            skSolve(sketch);
        }
        {
            var Q0;
            Q0=makeQuery(id+"F30.imprint","IMPRINT",FACE,{"disambiguationData":[TD([[makeQuery(id+"F30.imprint","IMPRINT",EDGE,{"derivedFrom":sQuery(id+"F30.wireOp",EDGE,"E387.bottom")}),-1.0]])]});
            extrude(context, id + "F31", {"entities" : qUnion([Q0]), "operationType" : NewBodyOperationType.ADD, "oppositeDirection" : true, "depth" : 25.4 * mm});
        }
        {
            var Q0;
            Q0=makeQuery(id+"F23.imprint","IMPRINT",FACE,{"disambiguationData":[TD([[makeQuery(id+"F23.imprint","IMPRINT",EDGE,{"derivedFrom":sQuery(id+"F23.wireOp",EDGE,"E378.0.0")}),1.0]])]});
            var sketch = newSketch(context, id + "F32", { "sketchPlane" : qUnion([Q0])});
            skLineSegment(sketch, "E388", {"start": v(-887.3, 0) * mm, "end": v(-2146.74, 0) * mm, "construction": true});
            skPoint(sketch, "E389.0", {"position": v(-1221.08, -506.25) * mm});
            skPoint(sketch, "E390.0", {"position": v(-1282.57, -390.13) * mm});
            skLineSegment(sketch, "E391.0.0", {"start": v(-459.08, 117.28) * mm, "end": v(-459.08, 177.36) * mm, "construction": true});
            skLineSegment(sketch, "E391.0.1", {"start": v(-459.08, 177.36) * mm, "end": v(-1282.57, 177.36) * mm, "construction": true});
            skLineSegment(sketch, "E391.0.2", {"start": v(-1282.57, 177.36) * mm, "end": v(-1282.57, 128.47) * mm, "construction": true});
            skLineSegment(sketch, "E391.0.3", {"start": v(-1282.57, 128.47) * mm, "end": v(-798.52, 128.47) * mm, "construction": true});
            skLineSegment(sketch, "E391.0.4", {"start": v(-798.52, 128.47) * mm, "end": v(-798.52, 114.75) * mm, "construction": true});
            skLineSegment(sketch, "E391.0.5", {"start": v(-798.52, 114.75) * mm, "end": v(-1282.57, 114.75) * mm, "construction": true});
            skLineSegment(sketch, "E391.0.6", {"start": v(-1282.57, 114.75) * mm, "end": v(-1282.57, 45.92) * mm, "construction": true});
            skLineSegment(sketch, "E391.0.7", {"start": v(-1282.57, 45.92) * mm, "end": v(-870.4, 45.92) * mm, "construction": true});
            skLineSegment(sketch, "E391.0.8", {"start": v(-870.4, 45.92) * mm, "end": v(-870.4, 32.2) * mm, "construction": true});
            skLineSegment(sketch, "E391.0.9", {"start": v(-870.4, 32.2) * mm, "end": v(-1282.57, 32.2) * mm, "construction": true});
            skLineSegment(sketch, "E391.0.10", {"start": v(-1282.57, 32.2) * mm, "end": v(-1282.57, -36.63) * mm, "construction": true});
            skLineSegment(sketch, "E391.0.11", {"start": v(-1282.57, -36.63) * mm, "end": v(-945.59, -36.63) * mm, "construction": true});
            skLineSegment(sketch, "E391.0.12", {"start": v(-945.59, -36.63) * mm, "end": v(-945.59, -50.35) * mm, "construction": true});
            skLineSegment(sketch, "E391.0.13", {"start": v(-945.59, -50.35) * mm, "end": v(-1282.57, -50.35) * mm, "construction": true});
            skLineSegment(sketch, "E391.0.14", {"start": v(-1282.57, -50.35) * mm, "end": v(-1282.57, -119.18) * mm, "construction": true});
            skLineSegment(sketch, "E391.0.15", {"start": v(-1282.57, -119.18) * mm, "end": v(-1041.35, -119.18) * mm, "construction": true});
            skLineSegment(sketch, "E391.0.16", {"start": v(-1041.35, -119.18) * mm, "end": v(-1041.35, -132.9) * mm, "construction": true});
            skLineSegment(sketch, "E391.0.17", {"start": v(-1041.35, -132.9) * mm, "end": v(-1282.57, -132.9) * mm, "construction": true});
            skLineSegment(sketch, "E391.0.18", {"start": v(-1282.57, -132.9) * mm, "end": v(-1282.57, -201.73) * mm, "construction": true});
            skLineSegment(sketch, "E391.0.19", {"start": v(-1282.57, -201.73) * mm, "end": v(-1107.39, -201.73) * mm, "construction": true});
            skLineSegment(sketch, "E391.0.20", {"start": v(-1107.39, -201.73) * mm, "end": v(-1107.39, -215.45) * mm, "construction": true});
            skLineSegment(sketch, "E391.0.21", {"start": v(-1107.39, -215.45) * mm, "end": v(-1282.57, -215.45) * mm, "construction": true});
            skLineSegment(sketch, "E391.0.22", {"start": v(-1282.57, -215.45) * mm, "end": v(-1282.57, -284.28) * mm, "construction": true});
            skLineSegment(sketch, "E391.0.23", {"start": v(-1282.57, -284.28) * mm, "end": v(-1084.53, -284.28) * mm, "construction": true});
            skLineSegment(sketch, "E391.0.24", {"start": v(-1084.53, -284.28) * mm, "end": v(-1084.53, -298) * mm, "construction": true});
            skLineSegment(sketch, "E391.0.25", {"start": v(-1084.53, -298) * mm, "end": v(-1282.57, -298) * mm, "construction": true});
            skLineSegment(sketch, "E391.0.26", {"start": v(-1282.57, -298) * mm, "end": v(-1282.57, -482.26) * mm, "construction": true});
            skLineSegment(sketch, "E391.0.27", {"start": v(-1282.57, -482.26) * mm, "end": v(-1221.08, -482.26) * mm, "construction": true});
            skLineSegment(sketch, "E391.0.28", {"start": v(-1221.08, -482.26) * mm, "end": v(-1221.08, -506.25) * mm, "construction": true});
            skLineSegment(sketch, "E391.0.29", {"start": v(-1221.08, -506.25) * mm, "end": v(-1159.47, -506.25) * mm, "construction": true});
            skLineSegment(sketch, "E391.0.30", {"start": v(-1159.47, -506.25) * mm, "end": v(-1159.47, -482.26) * mm, "construction": true});
            skLineSegment(sketch, "E391.0.31", {"start": v(-1159.47, -482.26) * mm, "end": v(-1098.1, -482.26) * mm, "construction": true});
            skLineSegment(sketch, "E391.0.32", {"start": v(-1098.1, -482.26) * mm, "end": v(-1098.1, -506.25) * mm, "construction": true});
            skLineSegment(sketch, "E391.0.33", {"start": v(-1098.1, -506.25) * mm, "end": v(-1036.48, -506.25) * mm, "construction": true});
            skLineSegment(sketch, "E391.0.34", {"start": v(-1036.48, -506.25) * mm, "end": v(-1036.48, -482.26) * mm, "construction": true});
            skLineSegment(sketch, "E391.0.35", {"start": v(-1036.48, -482.26) * mm, "end": v(-975.11, -482.26) * mm, "construction": true});
            skLineSegment(sketch, "E391.0.36", {"start": v(-975.11, -482.26) * mm, "end": v(-975.11, -506.25) * mm, "construction": true});
            skLineSegment(sketch, "E391.0.37", {"start": v(-975.11, -506.25) * mm, "end": v(-913.5, -506.25) * mm, "construction": true});
            skLineSegment(sketch, "E391.0.38", {"start": v(-913.5, -506.25) * mm, "end": v(-913.5, -482.26) * mm, "construction": true});
            skLineSegment(sketch, "E391.0.39", {"start": v(-913.5, -482.26) * mm, "end": v(-852.13, -482.26) * mm, "construction": true});
            skLineSegment(sketch, "E391.0.40", {"start": v(-852.13, -482.26) * mm, "end": v(-852.13, -506.25) * mm, "construction": true});
            skLineSegment(sketch, "E391.0.41", {"start": v(-852.13, -506.25) * mm, "end": v(-790.52, -506.25) * mm, "construction": true});
            skLineSegment(sketch, "E391.0.42", {"start": v(-790.52, -506.25) * mm, "end": v(-790.52, -482.26) * mm, "construction": true});
            skLineSegment(sketch, "E391.0.43", {"start": v(-790.52, -482.26) * mm, "end": v(-729.15, -482.26) * mm, "construction": true});
            skLineSegment(sketch, "E391.0.44", {"start": v(-729.15, -482.26) * mm, "end": v(-729.15, -506.25) * mm, "construction": true});
            skLineSegment(sketch, "E391.0.45", {"start": v(-729.15, -506.25) * mm, "end": v(-667.53, -506.25) * mm, "construction": true});
            skLineSegment(sketch, "E391.0.46", {"start": v(-667.53, -506.25) * mm, "end": v(-667.53, -482.26) * mm, "construction": true});
            skLineSegment(sketch, "E391.0.47", {"start": v(-667.53, -482.26) * mm, "end": v(-606.17, -482.26) * mm, "construction": true});
            skLineSegment(sketch, "E391.0.48", {"start": v(-606.17, -482.26) * mm, "end": v(-606.17, -506.25) * mm, "construction": true});
            skLineSegment(sketch, "E391.0.49", {"start": v(-606.17, -506.25) * mm, "end": v(-544.55, -506.25) * mm, "construction": true});
            skLineSegment(sketch, "E391.0.50", {"start": v(-544.55, -506.25) * mm, "end": v(-544.55, -482.26) * mm, "construction": true});
            skLineSegment(sketch, "E391.0.51", {"start": v(-544.55, -482.26) * mm, "end": v(-459.08, -482.26) * mm, "construction": true});
            skLineSegment(sketch, "E391.0.52", {"start": v(-459.08, -482.26) * mm, "end": v(-459.08, -422.19) * mm, "construction": true});
            skLineSegment(sketch, "E391.0.53", {"start": v(-459.08, -422.19) * mm, "end": v(-483.06, -422.19) * mm, "construction": true});
            skLineSegment(sketch, "E391.0.54", {"start": v(-483.06, -422.19) * mm, "end": v(-483.06, -362.36) * mm, "construction": true});
            skLineSegment(sketch, "E391.0.55", {"start": v(-483.06, -362.36) * mm, "end": v(-459.08, -362.36) * mm, "construction": true});
            skLineSegment(sketch, "E391.0.56", {"start": v(-459.08, -362.36) * mm, "end": v(-459.08, -302.28) * mm, "construction": true});
            skLineSegment(sketch, "E391.0.57", {"start": v(-459.08, -302.28) * mm, "end": v(-483.06, -302.28) * mm, "construction": true});
            skLineSegment(sketch, "E391.0.58", {"start": v(-483.06, -302.28) * mm, "end": v(-483.06, -242.45) * mm, "construction": true});
            skLineSegment(sketch, "E391.0.59", {"start": v(-483.06, -242.45) * mm, "end": v(-459.08, -242.45) * mm, "construction": true});
            skLineSegment(sketch, "E391.0.60", {"start": v(-459.08, -242.45) * mm, "end": v(-459.08, -182.38) * mm, "construction": true});
            skLineSegment(sketch, "E391.0.61", {"start": v(-459.08, -182.38) * mm, "end": v(-483.06, -182.38) * mm, "construction": true});
            skLineSegment(sketch, "E391.0.62", {"start": v(-483.06, -182.38) * mm, "end": v(-483.06, -122.53) * mm, "construction": true});
            skLineSegment(sketch, "E391.0.63", {"start": v(-483.06, -122.53) * mm, "end": v(-459.08, -122.53) * mm, "construction": true});
            skLineSegment(sketch, "E391.0.64", {"start": v(-459.08, -122.53) * mm, "end": v(-459.08, -62.46) * mm, "construction": true});
            skLineSegment(sketch, "E391.0.65", {"start": v(-459.08, -62.46) * mm, "end": v(-483.06, -62.46) * mm, "construction": true});
            skLineSegment(sketch, "E391.0.66", {"start": v(-483.06, -62.46) * mm, "end": v(-483.06, -2.63) * mm, "construction": true});
            skLineSegment(sketch, "E391.0.67", {"start": v(-483.06, -2.63) * mm, "end": v(-459.08, -2.63) * mm, "construction": true});
            skLineSegment(sketch, "E391.0.68", {"start": v(-459.08, -2.63) * mm, "end": v(-459.08, 57.45) * mm, "construction": true});
            skLineSegment(sketch, "E391.0.69", {"start": v(-459.08, 57.45) * mm, "end": v(-483.06, 57.45) * mm, "construction": true});
            skLineSegment(sketch, "E391.0.70", {"start": v(-483.06, 57.45) * mm, "end": v(-483.06, 117.28) * mm, "construction": true});
            skLineSegment(sketch, "E391.0.71", {"start": v(-483.06, 117.28) * mm, "end": v(-459.08, 117.28) * mm, "construction": true});
            skLineSegment(sketch, "E392.0.0", {"start": v(393.28, -62.59) * mm, "end": v(393.28, -2.5) * mm});
            skLineSegment(sketch, "E392.0.1", {"start": v(393.28, -2.5) * mm, "end": v(-454.2, -2.5) * mm});
            skLineSegment(sketch, "E392.0.2", {"start": v(-454.2, -2.5) * mm, "end": v(-454.2, -62.59) * mm});
            skLineSegment(sketch, "E392.0.3", {"start": v(-454.2, -62.59) * mm, "end": v(-430.22, -62.59) * mm});
            skLineSegment(sketch, "E392.0.4", {"start": v(-430.22, -62.59) * mm, "end": v(-430.22, -122.41) * mm});
            skLineSegment(sketch, "E392.0.5", {"start": v(-430.22, -122.41) * mm, "end": v(-454.2, -122.41) * mm});
            skLineSegment(sketch, "E392.0.6", {"start": v(-454.2, -122.41) * mm, "end": v(-454.2, -182.5) * mm});
            skLineSegment(sketch, "E392.0.7", {"start": v(-454.2, -182.5) * mm, "end": v(-430.22, -182.5) * mm});
            skLineSegment(sketch, "E392.0.8", {"start": v(-430.22, -182.5) * mm, "end": v(-430.22, -242.33) * mm});
            skLineSegment(sketch, "E392.0.9", {"start": v(-430.22, -242.33) * mm, "end": v(-454.2, -242.33) * mm});
            skLineSegment(sketch, "E392.0.10", {"start": v(-454.2, -242.33) * mm, "end": v(-454.2, -302.4) * mm});
            skLineSegment(sketch, "E392.0.11", {"start": v(-454.2, -302.4) * mm, "end": v(-430.22, -302.4) * mm});
            skLineSegment(sketch, "E392.0.12", {"start": v(-430.22, -302.4) * mm, "end": v(-430.22, -362.23) * mm});
            skLineSegment(sketch, "E392.0.13", {"start": v(-430.22, -362.23) * mm, "end": v(-454.2, -362.23) * mm});
            skLineSegment(sketch, "E392.0.14", {"start": v(-454.2, -362.23) * mm, "end": v(-454.2, -422.3) * mm});
            skLineSegment(sketch, "E392.0.15", {"start": v(-454.2, -422.3) * mm, "end": v(-430.22, -422.3) * mm});
            skLineSegment(sketch, "E392.0.16", {"start": v(-430.22, -422.3) * mm, "end": v(-430.22, -482.15) * mm});
            skLineSegment(sketch, "E392.0.17", {"start": v(-430.22, -482.15) * mm, "end": v(-454.2, -482.15) * mm});
            skLineSegment(sketch, "E392.0.18", {"start": v(-454.2, -482.15) * mm, "end": v(-454.2, -506.25) * mm});
            skLineSegment(sketch, "E392.0.19", {"start": v(-454.2, -506.25) * mm, "end": v(-368.61, -506.25) * mm});
            skLineSegment(sketch, "E392.0.20", {"start": v(-368.61, -506.25) * mm, "end": v(-368.61, -482.26) * mm});
            skLineSegment(sketch, "E392.0.21", {"start": v(-368.61, -482.26) * mm, "end": v(-307.24, -482.26) * mm});
            skLineSegment(sketch, "E392.0.22", {"start": v(-307.24, -482.26) * mm, "end": v(-307.24, -506.25) * mm});
            skLineSegment(sketch, "E392.0.23", {"start": v(-307.24, -506.25) * mm, "end": v(-245.62, -506.25) * mm});
            skLineSegment(sketch, "E392.0.24", {"start": v(-245.62, -506.25) * mm, "end": v(-245.62, -482.26) * mm});
            skLineSegment(sketch, "E392.0.25", {"start": v(-245.62, -482.26) * mm, "end": v(-184.26, -482.26) * mm});
            skLineSegment(sketch, "E392.0.26", {"start": v(-184.26, -482.26) * mm, "end": v(-184.26, -506.25) * mm});
            skLineSegment(sketch, "E392.0.27", {"start": v(-184.26, -506.25) * mm, "end": v(-122.64, -506.25) * mm});
            skLineSegment(sketch, "E392.0.28", {"start": v(-122.64, -506.25) * mm, "end": v(-122.64, -482.26) * mm});
            skLineSegment(sketch, "E392.0.29", {"start": v(-122.64, -482.26) * mm, "end": v(-61.27, -482.26) * mm});
            skLineSegment(sketch, "E392.0.30", {"start": v(-61.27, -482.26) * mm, "end": v(-61.27, -506.25) * mm});
            skLineSegment(sketch, "E392.0.31", {"start": v(-61.27, -506.25) * mm, "end": v(0.34, -506.25) * mm});
            skLineSegment(sketch, "E392.0.32", {"start": v(0.34, -506.25) * mm, "end": v(0.34, -482.26) * mm});
            skLineSegment(sketch, "E392.0.33", {"start": v(0.34, -482.26) * mm, "end": v(61.71, -482.26) * mm});
            skLineSegment(sketch, "E392.0.34", {"start": v(61.71, -482.26) * mm, "end": v(61.71, -506.25) * mm});
            skLineSegment(sketch, "E392.0.35", {"start": v(61.71, -506.25) * mm, "end": v(123.33, -506.25) * mm});
            skLineSegment(sketch, "E392.0.36", {"start": v(123.33, -506.25) * mm, "end": v(123.33, -482.26) * mm});
            skLineSegment(sketch, "E392.0.37", {"start": v(123.33, -482.26) * mm, "end": v(184.7, -482.26) * mm});
            skLineSegment(sketch, "E392.0.38", {"start": v(184.7, -482.26) * mm, "end": v(184.7, -506.25) * mm});
            skLineSegment(sketch, "E392.0.39", {"start": v(184.7, -506.25) * mm, "end": v(246.3, -506.25) * mm});
            skLineSegment(sketch, "E392.0.40", {"start": v(246.3, -506.25) * mm, "end": v(246.3, -482.26) * mm});
            skLineSegment(sketch, "E392.0.41", {"start": v(246.3, -482.26) * mm, "end": v(307.69, -482.26) * mm});
            skLineSegment(sketch, "E392.0.42", {"start": v(307.69, -482.26) * mm, "end": v(307.69, -506.25) * mm});
            skLineSegment(sketch, "E392.0.43", {"start": v(307.69, -506.25) * mm, "end": v(393.28, -506.25) * mm});
            skLineSegment(sketch, "E392.0.44", {"start": v(393.28, -506.25) * mm, "end": v(393.28, -482.15) * mm});
            skLineSegment(sketch, "E392.0.45", {"start": v(393.28, -482.15) * mm, "end": v(369.29, -482.15) * mm});
            skLineSegment(sketch, "E392.0.46", {"start": v(369.29, -482.15) * mm, "end": v(369.29, -422.3) * mm});
            skLineSegment(sketch, "E392.0.47", {"start": v(369.29, -422.3) * mm, "end": v(393.28, -422.3) * mm});
            skLineSegment(sketch, "E392.0.48", {"start": v(393.28, -422.3) * mm, "end": v(393.28, -362.23) * mm});
            skLineSegment(sketch, "E392.0.49", {"start": v(393.28, -362.23) * mm, "end": v(369.29, -362.23) * mm});
            skLineSegment(sketch, "E392.0.50", {"start": v(369.29, -362.23) * mm, "end": v(369.29, -302.4) * mm});
            skLineSegment(sketch, "E392.0.51", {"start": v(369.29, -302.4) * mm, "end": v(393.28, -302.4) * mm});
            skLineSegment(sketch, "E392.0.52", {"start": v(393.28, -302.4) * mm, "end": v(393.28, -242.33) * mm});
            skLineSegment(sketch, "E392.0.53", {"start": v(393.28, -242.33) * mm, "end": v(369.29, -242.33) * mm});
            skLineSegment(sketch, "E392.0.54", {"start": v(369.29, -242.33) * mm, "end": v(369.29, -182.5) * mm});
            skLineSegment(sketch, "E392.0.55", {"start": v(369.29, -182.5) * mm, "end": v(393.28, -182.5) * mm});
            skLineSegment(sketch, "E392.0.56", {"start": v(393.28, -182.5) * mm, "end": v(393.28, -122.41) * mm});
            skLineSegment(sketch, "E392.0.57", {"start": v(393.28, -122.41) * mm, "end": v(369.29, -122.41) * mm});
            skLineSegment(sketch, "E392.0.58", {"start": v(369.29, -122.41) * mm, "end": v(369.29, -62.59) * mm});
            skLineSegment(sketch, "E392.0.59", {"start": v(369.29, -62.59) * mm, "end": v(393.28, -62.59) * mm});
            skLineSegment(sketch, "E393", {"start": v(-430.22, -62.59) * mm, "end": v(369.29, -62.59) * mm});
            skLineSegment(sketch, "E394", {"start": v(-430.22, -362.23) * mm, "end": v(369.29, -362.23) * mm});
            skSolve(sketch);
        }
        {
            var Q0;
            Q0=makeQuery(id+"F32.imprint","IMPRINT",FACE,{"disambiguationData":[TD([[makeQuery(id+"F32.imprint","IMPRINT",EDGE,{"derivedFrom":sQuery(id+"F32.wireOp",EDGE,"E392.0.4")}),1.0]])]});
            extrude(context, id + "F33", {"entities" : qUnion([Q0]), "operationType" : NewBodyOperationType.REMOVE, "oppositeDirection" : true, "depth" : 25.4 * mm});
        }
    });
